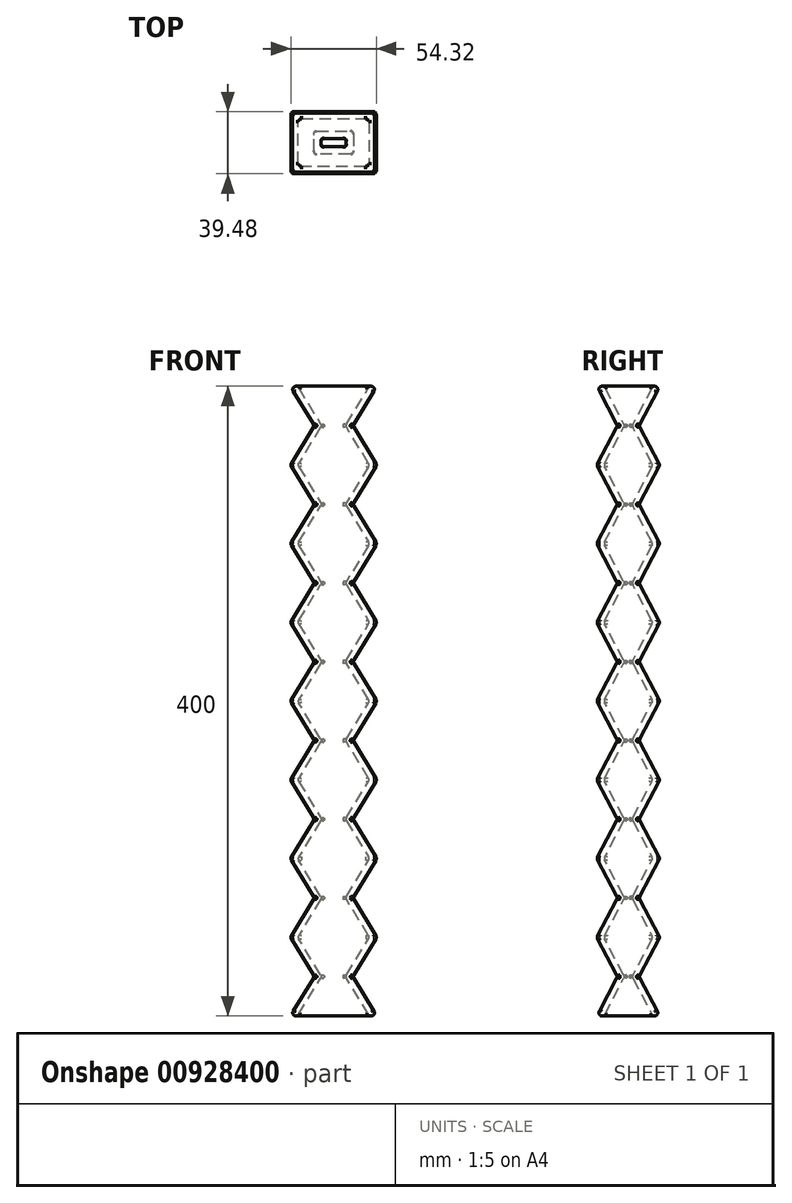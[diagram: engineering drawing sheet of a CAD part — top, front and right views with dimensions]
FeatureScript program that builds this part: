
annotation { "Feature Type Name" : "Feature", "Feature Type Description" : "" }
export const myFeature = defineFeature(function(context is Context, id is Id, definition is map)
    precondition{}
    {
        {
            var Q0;
            Q0=qCreatedBy(makeId("Top.planeOp"),FACE);
            var sketch = newSketch(context, id + "F0", { "sketchPlane" : qUnion([Q0])});
            skLineSegment(sketch, "E0.bottom", {"start": v(0, 0) * mm, "end": v(55, 0) * mm});
            skLineSegment(sketch, "E0.top", {"start": v(0, 40) * mm, "end": v(55, 40) * mm});
            skLineSegment(sketch, "E0.left", {"start": v(0, 0) * mm, "end": v(0, 40) * mm});
            skLineSegment(sketch, "E0.right", {"start": v(55, 0) * mm, "end": v(55, 40) * mm});
            skSolve(sketch);
        }
        {
            var Q0;
            Q0=qCreatedBy(makeId("Top.planeOp"),FACE);
            var sketch = newSketch(context, id + "F1", { "sketchPlane" : qUnion([Q0])});
            skSolve(sketch);
        }
        {
            var Q0;
            Q0 = qBodyType(qCreatedBy(id + "F1" ,EDGE), BodyType.WIRE);
            var Q1;
            Q1=qCreatedBy(makeId("Top.planeOp"),FACE);
            cPlane(context, id + "F2", {"entities" : qUnion([Q0, Q1]), "cplaneType" : CPlaneType.OFFSET, "offset" : 25 * mm, "width" : 150 * mm, "height" : 150 * mm});
        }
        {
            var Q0;
            Q0=qCreatedBy(id+"F2.planeOp",FACE);
            var sketch = newSketch(context, id + "F3", { "sketchPlane" : qUnion([Q0])});
            skLineSegment(sketch, "E1.bottom", {"start": v(39.73, 13.08) * mm, "end": v(15.27, 13.08) * mm});
            skLineSegment(sketch, "E1.top", {"start": v(39.73, 26.92) * mm, "end": v(15.27, 26.92) * mm});
            skLineSegment(sketch, "E1.left", {"start": v(39.73, 13.08) * mm, "end": v(39.73, 26.92) * mm});
            skLineSegment(sketch, "E1.right", {"start": v(15.27, 13.08) * mm, "end": v(15.27, 26.92) * mm});
            skLineSegment(sketch, "E2", {"start": v(27.5, 13.08) * mm, "end": v(27.5, 43.83) * mm, "construction": true});
            skPoint(sketch, "E2.endSnap0", {"position": v(27.5, 26.92) * mm});
            skLineSegment(sketch, "E3", {"start": v(27.5, 13.08) * mm, "end": v(27.5, -11.38) * mm, "construction": true});
            skLineSegment(sketch, "E4", {"start": v(39.73, 20) * mm, "end": v(-10.64, 20) * mm, "construction": true});
            skLineSegment(sketch, "E5", {"start": v(39.73, 20) * mm, "end": v(57.7, 20) * mm, "construction": true});
            skSolve(sketch);
        }
        {
            var Q0;
            Q0=makeQuery(id+"F0.imprint","IMPRINT",FACE,{"disambiguationData":[TD([[makeQuery(id+"F0.imprint","IMPRINT",EDGE,{"derivedFrom":sQuery(id+"F0.wireOp",EDGE,"E0.bottom")}),1.0]])]});
            var Q1;
            Q1=makeQuery(id+"F3.imprint","IMPRINT",FACE,{"disambiguationData":[TD([[makeQuery(id+"F3.imprint","IMPRINT",EDGE,{"derivedFrom":sQuery(id+"F3.wireOp",EDGE,"E1.bottom")}),-1.0]])]});
            loft(context, id + "F4", {"sheetProfilesArray" : [{ "sheetProfileEntities" : qUnion([Q0]) }, { "sheetProfileEntities" : qUnion([Q1]) }]});
        }
        {
            var Q0;
            Q0=makeQuery(id+"F4.opLoft","SWEPT_BODY",BODY,{"disambiguationData":[OSD([makeQuery(id+"F0.imprint","IMPRINT",FACE,{"disambiguationData":[TD([[makeQuery(id+"F0.imprint","IMPRINT",EDGE,{"derivedFrom":sQuery(id+"F0.wireOp",EDGE,"E0.bottom")}),1.0]])]}),makeQuery(id+"F3.imprint","IMPRINT",FACE,{"disambiguationData":[TD([[makeQuery(id+"F3.imprint","IMPRINT",EDGE,{"derivedFrom":sQuery(id+"F3.wireOp",EDGE,"E1.bottom")}),-1.0]])]})])]});
            var Q1;
            Q1=makeQuery(id+"F4.opLoft","CAP_FACE",FACE,{"disambiguationData":[OSD([makeQuery(id+"F3.imprint","IMPRINT",FACE,{"disambiguationData":[TD([[makeQuery(id+"F3.imprint","IMPRINT",EDGE,{"derivedFrom":sQuery(id+"F3.wireOp",EDGE,"E1.bottom")}),-1.0]])]})])],"isStart":true});
            mirror(context, id + "F5", {"operationType" : NewBodyOperationType.ADD, "entities" : qUnion([Q0]), "mirrorPlane" : qUnion([Q1])});
        }
        {
            var Q0;
            Q0=makeQuery(id+"F4.opLoft","SWEPT_BODY",BODY,{"disambiguationData":[OSD([makeQuery(id+"F0.imprint","IMPRINT",FACE,{"disambiguationData":[TD([[makeQuery(id+"F0.imprint","IMPRINT",EDGE,{"derivedFrom":sQuery(id+"F0.wireOp",EDGE,"E0.bottom")}),1.0]])]}),makeQuery(id+"F3.imprint","IMPRINT",FACE,{"disambiguationData":[TD([[makeQuery(id+"F3.imprint","IMPRINT",EDGE,{"derivedFrom":sQuery(id+"F3.wireOp",EDGE,"E1.bottom")}),-1.0]])]})])]});
            var Q1;
            Q1=makeQuery(id+"F5.opPattern","COPY",FACE,{"derivedFrom":makeQuery(id+"F4.opLoft","CAP_FACE",FACE,{"disambiguationData":[OSD([makeQuery(id+"F0.imprint","IMPRINT",FACE,{"disambiguationData":[TD([[makeQuery(id+"F0.imprint","IMPRINT",EDGE,{"derivedFrom":sQuery(id+"F0.wireOp",EDGE,"E0.bottom")}),1.0]])]})])],"isStart":true}),"instanceName":"1"});
            mirror(context, id + "F6", {"operationType" : NewBodyOperationType.ADD, "entities" : qUnion([Q0]), "mirrorPlane" : qUnion([Q1])});
        }
        {
            var Q0;
            Q0=makeQuery(id+"F4.opLoft","SWEPT_BODY",BODY,{"disambiguationData":[OSD([makeQuery(id+"F0.imprint","IMPRINT",FACE,{"disambiguationData":[TD([[makeQuery(id+"F0.imprint","IMPRINT",EDGE,{"derivedFrom":sQuery(id+"F0.wireOp",EDGE,"E0.bottom")}),1.0]])]}),makeQuery(id+"F3.imprint","IMPRINT",FACE,{"disambiguationData":[TD([[makeQuery(id+"F3.imprint","IMPRINT",EDGE,{"derivedFrom":sQuery(id+"F3.wireOp",EDGE,"E1.bottom")}),-1.0]])]})])]});
            var Q1;
            Q1=makeQuery(id+"F4.opLoft","CAP_FACE",FACE,{"disambiguationData":[OSD([makeQuery(id+"F0.imprint","IMPRINT",FACE,{"disambiguationData":[TD([[makeQuery(id+"F0.imprint","IMPRINT",EDGE,{"derivedFrom":sQuery(id+"F0.wireOp",EDGE,"E0.bottom")}),1.0]])]})])],"isStart":true});
            mirror(context, id + "F7", {"operationType" : NewBodyOperationType.ADD, "entities" : qUnion([Q0]), "mirrorPlane" : qUnion([Q1])});
        }
        {
            var Q0;
            Q0=makeQuery(id+"F4.opLoft","SWEPT_BODY",BODY,{"disambiguationData":[OSD([makeQuery(id+"F0.imprint","IMPRINT",FACE,{"disambiguationData":[TD([[makeQuery(id+"F0.imprint","IMPRINT",EDGE,{"derivedFrom":sQuery(id+"F0.wireOp",EDGE,"E0.bottom")}),1.0]])]}),makeQuery(id+"F3.imprint","IMPRINT",FACE,{"disambiguationData":[TD([[makeQuery(id+"F3.imprint","IMPRINT",EDGE,{"derivedFrom":sQuery(id+"F3.wireOp",EDGE,"E1.bottom")}),-1.0]])]})])]});
            var Q1;
            Q1=makeQuery(id+"F7.opPattern","COPY",FACE,{"derivedFrom":makeQuery(id+"F6.opPattern","COPY",FACE,{"derivedFrom":makeQuery(id+"F4.opLoft","CAP_FACE",FACE,{"disambiguationData":[OSD([makeQuery(id+"F0.imprint","IMPRINT",FACE,{"disambiguationData":[TD([[makeQuery(id+"F0.imprint","IMPRINT",EDGE,{"derivedFrom":sQuery(id+"F0.wireOp",EDGE,"E0.bottom")}),1.0]])]})])],"isStart":true}),"instanceName":"1"}),"instanceName":"1"});
            mirror(context, id + "F8", {"operationType" : NewBodyOperationType.ADD, "entities" : qUnion([Q0]), "mirrorPlane" : qUnion([Q1])});
        }
        {
            var Q0;
            Q0=makeQuery(id+"F6.opPattern","COPY",FACE,{"derivedFrom":makeQuery(id+"F4.opLoft","CAP_FACE",FACE,{"disambiguationData":[OSD([makeQuery(id+"F0.imprint","IMPRINT",FACE,{"disambiguationData":[TD([[makeQuery(id+"F0.imprint","IMPRINT",EDGE,{"derivedFrom":sQuery(id+"F0.wireOp",EDGE,"E0.bottom")}),1.0]])]})])],"isStart":true}),"instanceName":"1"});
            var Q1;
            Q1=makeQuery(id+"F8.opPattern","COPY",FACE,{"derivedFrom":makeQuery(id+"F6.opPattern","COPY",FACE,{"derivedFrom":makeQuery(id+"F4.opLoft","CAP_FACE",FACE,{"disambiguationData":[OSD([makeQuery(id+"F0.imprint","IMPRINT",FACE,{"disambiguationData":[TD([[makeQuery(id+"F0.imprint","IMPRINT",EDGE,{"derivedFrom":sQuery(id+"F0.wireOp",EDGE,"E0.bottom")}),1.0]])]})])],"isStart":true}),"instanceName":"1"}),"instanceName":"1"});
            shell(context, id + "F9", {"entities" : qUnion([Q0, Q1]), "thickness" : 4 * mm});
        }
        {
            var Q0;
            Q0=makeQuery(id+"F4.opLoft","SWEPT_BODY",BODY,{"disambiguationData":[OSD([makeQuery(id+"F0.imprint","IMPRINT",FACE,{"disambiguationData":[TD([[makeQuery(id+"F0.imprint","IMPRINT",EDGE,{"derivedFrom":sQuery(id+"F0.wireOp",EDGE,"E0.bottom")}),1.0]])]}),makeQuery(id+"F3.imprint","IMPRINT",FACE,{"disambiguationData":[TD([[makeQuery(id+"F3.imprint","IMPRINT",EDGE,{"derivedFrom":sQuery(id+"F3.wireOp",EDGE,"E1.bottom")}),-1.0]])]})])]});
            var Q1;
            {var subQ0=makeQuery(id+"F5.opPattern","COPY",EDGE,{"derivedFrom":makeQuery(id+"F4.opLoft","MID_CAP_EDGE",EDGE,{"disambiguationData":[OSD([sQuery(id+"F0.wireOp",EDGE,"E0.bottom"),sQuery(id+"F0.wireOp",EDGE,"E0.top"),sQuery(id+"F0.wireOp",EDGE,"E0.left")])],"capPos":0.0}),"instanceName":"1"});Q1=makeQuery(id+"F8.opPattern","COPY",EDGE,{"derivedFrom":makeQuery(id+"F6.boolean.opBoolean","MERGE",EDGE,{"derivedFrom":[subQ0,makeQuery(id+"F6.opPattern","COPY",EDGE,{"derivedFrom":subQ0,"instanceName":"1"})]}),"instanceName":"1"});}
            transform(context, id + "F10", {"entities" : qUnion([Q0]), "transformType" : TransformType.TRANSLATION_ENTITY, "oppositeDirectionEntity" : false, "transformLine" : qUnion([Q1]), "makeCopy" : false});
        }
        {
            var Q0;
            Q0=makeQuery(id+"F5.opPattern","COPY",EDGE,{"derivedFrom":makeQuery(id+"F4.opLoft","SWEPT_EDGE",EDGE,{"disambiguationData":[OSD([sQuery(id+"F0.wireOp",EDGE,"E0.bottom"),sQuery(id+"F0.wireOp",EDGE,"E0.left"),sQuery(id+"F3.wireOp",EDGE,"E1.bottom"),sQuery(id+"F3.wireOp",EDGE,"E1.right")])]}),"instanceName":"1"});
            var Q1;
            {var subQ0=makeQuery(id+"F4.opLoft","MID_CAP_EDGE",EDGE,{"disambiguationData":[OSD([sQuery(id+"F3.wireOp",EDGE,"E1.bottom"),sQuery(id+"F3.wireOp",EDGE,"E1.left"),sQuery(id+"F3.wireOp",EDGE,"E1.right")])],"capPos":1.0});Q1=makeQuery(id+"F5.boolean.opBoolean","MERGE",EDGE,{"derivedFrom":[subQ0,makeQuery(id+"F5.opPattern","COPY",EDGE,{"derivedFrom":subQ0,"instanceName":"1"})]});}
            var Q2;
            Q2=makeQuery(id+"F6.opPattern","COPY",EDGE,{"derivedFrom":makeQuery(id+"F4.opLoft","SWEPT_EDGE",EDGE,{"disambiguationData":[OSD([sQuery(id+"F0.wireOp",EDGE,"E0.bottom"),sQuery(id+"F0.wireOp",EDGE,"E0.left"),sQuery(id+"F3.wireOp",EDGE,"E1.bottom"),sQuery(id+"F3.wireOp",EDGE,"E1.right")])]}),"instanceName":"1"});
            var Q3;
            Q3=makeQuery(id+"F6.opPattern","COPY",EDGE,{"derivedFrom":makeQuery(id+"F5.opPattern","COPY",EDGE,{"derivedFrom":makeQuery(id+"F4.opLoft","SWEPT_EDGE",EDGE,{"disambiguationData":[OSD([sQuery(id+"F0.wireOp",EDGE,"E0.bottom"),sQuery(id+"F0.wireOp",EDGE,"E0.left"),sQuery(id+"F3.wireOp",EDGE,"E1.bottom"),sQuery(id+"F3.wireOp",EDGE,"E1.right")])]}),"instanceName":"1"}),"instanceName":"1"});
            var Q4;
            Q4=makeQuery(id+"F8.opPattern","COPY",EDGE,{"derivedFrom":makeQuery(id+"F6.opPattern","COPY",EDGE,{"derivedFrom":makeQuery(id+"F4.opLoft","MID_CAP_EDGE",EDGE,{"disambiguationData":[OSD([sQuery(id+"F0.wireOp",EDGE,"E0.bottom"),sQuery(id+"F0.wireOp",EDGE,"E0.top"),sQuery(id+"F0.wireOp",EDGE,"E0.right")])],"capPos":0.0}),"instanceName":"1"}),"instanceName":"1"});
            var Q5;
            {var subQ0=sQuery(id+"F3.wireOp",EDGE,"E1.right");var subQ1=sQuery(id+"F3.wireOp",EDGE,"E1.left");var subQ2=sQuery(id+"F3.wireOp",EDGE,"E1.bottom");var subQ3=makeQuery(id+"F4.opLoft","MID_CAP_EDGE",EDGE,{"disambiguationData":[OSD([subQ2,subQ1,subQ0])],"capPos":1.0});Q5=makeQuery(id+"F9.opShell","OFFSET_EDGE",EDGE,{"disambiguationData":[OSD([subQ2,subQ1,subQ0]),TDD([makeQuery(id+"F8.opPattern","COPY",EDGE,{"derivedFrom":makeQuery(id+"F7.opPattern","COPY",EDGE,{"derivedFrom":makeQuery(id+"F6.opPattern","COPY",EDGE,{"derivedFrom":makeQuery(id+"F5.boolean.opBoolean","MERGE",EDGE,{"derivedFrom":[subQ3,makeQuery(id+"F5.opPattern","COPY",EDGE,{"derivedFrom":subQ3,"instanceName":"1"})]}),"instanceName":"1"}),"instanceName":"1"}),"instanceName":"1"})])]});}
            var Q6;
            {var subQ0=sQuery(id+"F0.wireOp",EDGE,"E0.right");var subQ1=sQuery(id+"F0.wireOp",EDGE,"E0.top");var subQ2=sQuery(id+"F0.wireOp",EDGE,"E0.bottom");Q6=makeQuery(id+"F9.opShell","OFFSET_EDGE",EDGE,{"disambiguationData":[OSD([subQ2,subQ1,subQ0]),TDD([makeQuery(id+"F8.opPattern","COPY",EDGE,{"derivedFrom":makeQuery(id+"F6.opPattern","COPY",EDGE,{"derivedFrom":makeQuery(id+"F4.opLoft","MID_CAP_EDGE",EDGE,{"disambiguationData":[OSD([subQ2,subQ1,subQ0])],"capPos":0.0}),"instanceName":"1"}),"instanceName":"1"})])]});}
            var Q7;
            {var subQ0=sQuery(id+"F3.wireOp",EDGE,"E1.left");var subQ1=sQuery(id+"F3.wireOp",EDGE,"E1.top");var subQ2=sQuery(id+"F0.wireOp",EDGE,"E0.right");var subQ3=sQuery(id+"F0.wireOp",EDGE,"E0.top");Q7=makeQuery(id+"F9.opShell","OFFSET_EDGE",EDGE,{"disambiguationData":[OSD([subQ3,subQ2,subQ1,subQ0]),TDD([makeQuery(id+"F8.opPattern","COPY",EDGE,{"derivedFrom":makeQuery(id+"F6.opPattern","COPY",EDGE,{"derivedFrom":makeQuery(id+"F4.opLoft","SWEPT_EDGE",EDGE,{"disambiguationData":[OSD([subQ3,subQ2,subQ1,subQ0])]}),"instanceName":"1"}),"instanceName":"1"})])]});}
            var Q8;
            {var subQ0=sQuery(id+"F0.wireOp",EDGE,"E0.right");var subQ1=sQuery(id+"F0.wireOp",EDGE,"E0.top");var subQ2=sQuery(id+"F0.wireOp",EDGE,"E0.bottom");var subQ3=makeQuery(id+"F7.opPattern","COPY",EDGE,{"derivedFrom":makeQuery(id+"F6.opPattern","COPY",EDGE,{"derivedFrom":makeQuery(id+"F4.opLoft","MID_CAP_EDGE",EDGE,{"disambiguationData":[OSD([subQ2,subQ1,subQ0])],"capPos":0.0}),"instanceName":"1"}),"instanceName":"1"});Q8=makeQuery(id+"F9.opShell","OFFSET_EDGE",EDGE,{"disambiguationData":[OSD([subQ2,subQ1,subQ0]),TDD([makeQuery(id+"F8.boolean.opBoolean","MERGE",EDGE,{"derivedFrom":[subQ3,makeQuery(id+"F8.opPattern","COPY",EDGE,{"derivedFrom":subQ3,"instanceName":"1"})]})])]});}
            var Q9;
            {var subQ0=makeQuery(id+"F5.opPattern","COPY",EDGE,{"derivedFrom":makeQuery(id+"F4.opLoft","MID_CAP_EDGE",EDGE,{"disambiguationData":[OSD([sQuery(id+"F0.wireOp",EDGE,"E0.bottom"),sQuery(id+"F0.wireOp",EDGE,"E0.top"),sQuery(id+"F0.wireOp",EDGE,"E0.right")])],"capPos":0.0}),"instanceName":"1"});Q9=makeQuery(id+"F8.opPattern","COPY",EDGE,{"derivedFrom":makeQuery(id+"F6.boolean.opBoolean","MERGE",EDGE,{"derivedFrom":[subQ0,makeQuery(id+"F6.opPattern","COPY",EDGE,{"derivedFrom":subQ0,"instanceName":"1"})]}),"instanceName":"1"});}
            var Q10;
            {var subQ0=makeQuery(id+"F4.opLoft","MID_CAP_EDGE",EDGE,{"disambiguationData":[OSD([sQuery(id+"F3.wireOp",EDGE,"E1.bottom"),sQuery(id+"F3.wireOp",EDGE,"E1.left"),sQuery(id+"F3.wireOp",EDGE,"E1.right")])],"capPos":1.0});Q10=makeQuery(id+"F7.opPattern","COPY",EDGE,{"derivedFrom":makeQuery(id+"F5.boolean.opBoolean","MERGE",EDGE,{"derivedFrom":[subQ0,makeQuery(id+"F5.opPattern","COPY",EDGE,{"derivedFrom":subQ0,"instanceName":"1"})]}),"instanceName":"1"});}
            var Q11;
            {var subQ0=makeQuery(id+"F4.opLoft","MID_CAP_EDGE",EDGE,{"disambiguationData":[OSD([sQuery(id+"F3.wireOp",EDGE,"E1.bottom"),sQuery(id+"F3.wireOp",EDGE,"E1.top"),sQuery(id+"F3.wireOp",EDGE,"E1.left")])],"capPos":1.0});Q11=makeQuery(id+"F7.opPattern","COPY",EDGE,{"derivedFrom":makeQuery(id+"F6.opPattern","COPY",EDGE,{"derivedFrom":makeQuery(id+"F5.boolean.opBoolean","MERGE",EDGE,{"derivedFrom":[subQ0,makeQuery(id+"F5.opPattern","COPY",EDGE,{"derivedFrom":subQ0,"instanceName":"1"})]}),"instanceName":"1"}),"instanceName":"1"});}
            var Q12;
            {var subQ0=makeQuery(id+"F4.opLoft","MID_CAP_EDGE",EDGE,{"disambiguationData":[OSD([sQuery(id+"F3.wireOp",EDGE,"E1.top"),sQuery(id+"F3.wireOp",EDGE,"E1.left"),sQuery(id+"F3.wireOp",EDGE,"E1.right")])],"capPos":1.0});Q12=makeQuery(id+"F7.opPattern","COPY",EDGE,{"derivedFrom":makeQuery(id+"F6.opPattern","COPY",EDGE,{"derivedFrom":makeQuery(id+"F5.boolean.opBoolean","MERGE",EDGE,{"derivedFrom":[subQ0,makeQuery(id+"F5.opPattern","COPY",EDGE,{"derivedFrom":subQ0,"instanceName":"1"})]}),"instanceName":"1"}),"instanceName":"1"});}
            var Q13;
            {var subQ0=sQuery(id+"F0.wireOp",EDGE,"E0.left");var subQ1=sQuery(id+"F0.wireOp",EDGE,"E0.top");var subQ2=sQuery(id+"F0.wireOp",EDGE,"E0.bottom");var subQ3=makeQuery(id+"F5.opPattern","COPY",EDGE,{"derivedFrom":makeQuery(id+"F4.opLoft","MID_CAP_EDGE",EDGE,{"disambiguationData":[OSD([subQ2,subQ1,subQ0])],"capPos":0.0}),"instanceName":"1"});Q13=makeQuery(id+"F9.opShell","OFFSET_EDGE",EDGE,{"disambiguationData":[OSD([subQ2,subQ1,subQ0]),TDD([makeQuery(id+"F6.boolean.opBoolean","MERGE",EDGE,{"derivedFrom":[subQ3,makeQuery(id+"F6.opPattern","COPY",EDGE,{"derivedFrom":subQ3,"instanceName":"1"})]})])]});}
            var Q14;
            Q14=makeQuery(id+"F8.opPattern","COPY",EDGE,{"derivedFrom":makeQuery(id+"F7.opPattern","COPY",EDGE,{"derivedFrom":makeQuery(id+"F5.opPattern","COPY",EDGE,{"derivedFrom":makeQuery(id+"F4.opLoft","SWEPT_EDGE",EDGE,{"disambiguationData":[OSD([sQuery(id+"F0.wireOp",EDGE,"E0.bottom"),sQuery(id+"F0.wireOp",EDGE,"E0.right"),sQuery(id+"F3.wireOp",EDGE,"E1.bottom"),sQuery(id+"F3.wireOp",EDGE,"E1.left")])]}),"instanceName":"1"}),"instanceName":"1"}),"instanceName":"1"});
            var Q15;
            {var subQ0=sQuery(id+"F3.wireOp",EDGE,"E1.right");var subQ1=sQuery(id+"F3.wireOp",EDGE,"E1.top");var subQ2=sQuery(id+"F0.wireOp",EDGE,"E0.left");var subQ3=sQuery(id+"F0.wireOp",EDGE,"E0.top");Q15=makeQuery(id+"F9.opShell","OFFSET_EDGE",EDGE,{"disambiguationData":[OSD([subQ3,subQ2,subQ1,subQ0]),TDD([makeQuery(id+"F4.opLoft","SWEPT_EDGE",EDGE,{"disambiguationData":[OSD([subQ3,subQ2,subQ1,subQ0])]})])]});}
            var Q16;
            {var subQ0=makeQuery(id+"F4.opLoft","MID_CAP_EDGE",EDGE,{"disambiguationData":[OSD([sQuery(id+"F0.wireOp",EDGE,"E0.bottom"),sQuery(id+"F0.wireOp",EDGE,"E0.top"),sQuery(id+"F0.wireOp",EDGE,"E0.right")])],"capPos":0.0});Q16=makeQuery(id+"F8.opPattern","COPY",EDGE,{"derivedFrom":makeQuery(id+"F7.boolean.opBoolean","MERGE",EDGE,{"derivedFrom":[subQ0,makeQuery(id+"F7.opPattern","COPY",EDGE,{"derivedFrom":subQ0,"instanceName":"1"})]}),"instanceName":"1"});}
            var Q17;
            {var subQ0=makeQuery(id+"F4.opLoft","MID_CAP_EDGE",EDGE,{"disambiguationData":[OSD([sQuery(id+"F3.wireOp",EDGE,"E1.bottom"),sQuery(id+"F3.wireOp",EDGE,"E1.top"),sQuery(id+"F3.wireOp",EDGE,"E1.left")])],"capPos":1.0});Q17=makeQuery(id+"F7.opPattern","COPY",EDGE,{"derivedFrom":makeQuery(id+"F5.boolean.opBoolean","MERGE",EDGE,{"derivedFrom":[subQ0,makeQuery(id+"F5.opPattern","COPY",EDGE,{"derivedFrom":subQ0,"instanceName":"1"})]}),"instanceName":"1"});}
            var Q18;
            {var subQ0=sQuery(id+"F3.wireOp",EDGE,"E1.left");var subQ1=sQuery(id+"F3.wireOp",EDGE,"E1.bottom");var subQ2=sQuery(id+"F0.wireOp",EDGE,"E0.right");var subQ3=sQuery(id+"F0.wireOp",EDGE,"E0.bottom");Q18=makeQuery(id+"F9.opShell","OFFSET_EDGE",EDGE,{"disambiguationData":[OSD([subQ3,subQ2,subQ1,subQ0]),TDD([makeQuery(id+"F8.opPattern","COPY",EDGE,{"derivedFrom":makeQuery(id+"F7.opPattern","COPY",EDGE,{"derivedFrom":makeQuery(id+"F4.opLoft","SWEPT_EDGE",EDGE,{"disambiguationData":[OSD([subQ3,subQ2,subQ1,subQ0])]}),"instanceName":"1"}),"instanceName":"1"})])]});}
            var Q19;
            {var subQ0=sQuery(id+"F3.wireOp",EDGE,"E1.right");var subQ1=sQuery(id+"F3.wireOp",EDGE,"E1.top");var subQ2=sQuery(id+"F0.wireOp",EDGE,"E0.left");var subQ3=sQuery(id+"F0.wireOp",EDGE,"E0.top");Q19=makeQuery(id+"F9.opShell","OFFSET_EDGE",EDGE,{"disambiguationData":[OSD([subQ3,subQ2,subQ1,subQ0]),TDD([makeQuery(id+"F6.opPattern","COPY",EDGE,{"derivedFrom":makeQuery(id+"F4.opLoft","SWEPT_EDGE",EDGE,{"disambiguationData":[OSD([subQ3,subQ2,subQ1,subQ0])]}),"instanceName":"1"})])]});}
            var Q20;
            {var subQ0=sQuery(id+"F3.wireOp",EDGE,"E1.left");var subQ1=sQuery(id+"F3.wireOp",EDGE,"E1.bottom");var subQ2=sQuery(id+"F0.wireOp",EDGE,"E0.right");var subQ3=sQuery(id+"F0.wireOp",EDGE,"E0.bottom");Q20=makeQuery(id+"F9.opShell","OFFSET_EDGE",EDGE,{"disambiguationData":[OSD([subQ3,subQ2,subQ1,subQ0]),TDD([makeQuery(id+"F7.opPattern","COPY",EDGE,{"derivedFrom":makeQuery(id+"F6.opPattern","COPY",EDGE,{"derivedFrom":makeQuery(id+"F5.opPattern","COPY",EDGE,{"derivedFrom":makeQuery(id+"F4.opLoft","SWEPT_EDGE",EDGE,{"disambiguationData":[OSD([subQ3,subQ2,subQ1,subQ0])]}),"instanceName":"1"}),"instanceName":"1"}),"instanceName":"1"})])]});}
            var Q21;
            {var subQ0=sQuery(id+"F3.wireOp",EDGE,"E1.left");var subQ1=sQuery(id+"F3.wireOp",EDGE,"E1.top");var subQ2=sQuery(id+"F0.wireOp",EDGE,"E0.right");var subQ3=sQuery(id+"F0.wireOp",EDGE,"E0.top");Q21=makeQuery(id+"F9.opShell","OFFSET_EDGE",EDGE,{"disambiguationData":[OSD([subQ3,subQ2,subQ1,subQ0]),TDD([makeQuery(id+"F8.opPattern","COPY",EDGE,{"derivedFrom":makeQuery(id+"F7.opPattern","COPY",EDGE,{"derivedFrom":makeQuery(id+"F6.opPattern","COPY",EDGE,{"derivedFrom":makeQuery(id+"F4.opLoft","SWEPT_EDGE",EDGE,{"disambiguationData":[OSD([subQ3,subQ2,subQ1,subQ0])]}),"instanceName":"1"}),"instanceName":"1"}),"instanceName":"1"})])]});}
            var Q22;
            Q22=makeQuery(id+"F8.opPattern","COPY",EDGE,{"derivedFrom":makeQuery(id+"F6.opPattern","COPY",EDGE,{"derivedFrom":makeQuery(id+"F5.opPattern","COPY",EDGE,{"derivedFrom":makeQuery(id+"F4.opLoft","SWEPT_EDGE",EDGE,{"disambiguationData":[OSD([sQuery(id+"F0.wireOp",EDGE,"E0.top"),sQuery(id+"F0.wireOp",EDGE,"E0.right"),sQuery(id+"F3.wireOp",EDGE,"E1.top"),sQuery(id+"F3.wireOp",EDGE,"E1.left")])]}),"instanceName":"1"}),"instanceName":"1"}),"instanceName":"1"});
            var Q23;
            Q23=makeQuery(id+"F8.opPattern","COPY",EDGE,{"derivedFrom":makeQuery(id+"F7.opPattern","COPY",EDGE,{"derivedFrom":makeQuery(id+"F5.opPattern","COPY",EDGE,{"derivedFrom":makeQuery(id+"F4.opLoft","SWEPT_EDGE",EDGE,{"disambiguationData":[OSD([sQuery(id+"F0.wireOp",EDGE,"E0.top"),sQuery(id+"F0.wireOp",EDGE,"E0.right"),sQuery(id+"F3.wireOp",EDGE,"E1.top"),sQuery(id+"F3.wireOp",EDGE,"E1.left")])]}),"instanceName":"1"}),"instanceName":"1"}),"instanceName":"1"});
            var Q24;
            {var subQ0=sQuery(id+"F3.wireOp",EDGE,"E1.right");var subQ1=sQuery(id+"F3.wireOp",EDGE,"E1.top");var subQ2=sQuery(id+"F0.wireOp",EDGE,"E0.left");var subQ3=sQuery(id+"F0.wireOp",EDGE,"E0.top");Q24=makeQuery(id+"F9.opShell","OFFSET_EDGE",EDGE,{"disambiguationData":[OSD([subQ3,subQ2,subQ1,subQ0]),TDD([makeQuery(id+"F6.opPattern","COPY",EDGE,{"derivedFrom":makeQuery(id+"F5.opPattern","COPY",EDGE,{"derivedFrom":makeQuery(id+"F4.opLoft","SWEPT_EDGE",EDGE,{"disambiguationData":[OSD([subQ3,subQ2,subQ1,subQ0])]}),"instanceName":"1"}),"instanceName":"1"})])]});}
            var Q25;
            {var subQ0=sQuery(id+"F3.wireOp",EDGE,"E1.right");var subQ1=sQuery(id+"F3.wireOp",EDGE,"E1.bottom");var subQ2=sQuery(id+"F0.wireOp",EDGE,"E0.left");var subQ3=sQuery(id+"F0.wireOp",EDGE,"E0.bottom");Q25=makeQuery(id+"F9.opShell","OFFSET_EDGE",EDGE,{"disambiguationData":[OSD([subQ3,subQ2,subQ1,subQ0]),TDD([makeQuery(id+"F6.opPattern","COPY",EDGE,{"derivedFrom":makeQuery(id+"F5.opPattern","COPY",EDGE,{"derivedFrom":makeQuery(id+"F4.opLoft","SWEPT_EDGE",EDGE,{"disambiguationData":[OSD([subQ3,subQ2,subQ1,subQ0])]}),"instanceName":"1"}),"instanceName":"1"})])]});}
            var Q26;
            {var subQ0=sQuery(id+"F3.wireOp",EDGE,"E1.right");var subQ1=sQuery(id+"F3.wireOp",EDGE,"E1.left");var subQ2=sQuery(id+"F3.wireOp",EDGE,"E1.bottom");var subQ3=makeQuery(id+"F4.opLoft","MID_CAP_EDGE",EDGE,{"disambiguationData":[OSD([subQ2,subQ1,subQ0])],"capPos":1.0});Q26=makeQuery(id+"F9.opShell","OFFSET_EDGE",EDGE,{"disambiguationData":[OSD([subQ2,subQ1,subQ0]),TDD([makeQuery(id+"F5.boolean.opBoolean","MERGE",EDGE,{"derivedFrom":[subQ3,makeQuery(id+"F5.opPattern","COPY",EDGE,{"derivedFrom":subQ3,"instanceName":"1"})]})])]});}
            var Q27;
            {var subQ0=sQuery(id+"F3.wireOp",EDGE,"E1.right");var subQ1=sQuery(id+"F3.wireOp",EDGE,"E1.top");var subQ2=sQuery(id+"F0.wireOp",EDGE,"E0.left");var subQ3=sQuery(id+"F0.wireOp",EDGE,"E0.top");Q27=makeQuery(id+"F9.opShell","OFFSET_EDGE",EDGE,{"disambiguationData":[OSD([subQ3,subQ2,subQ1,subQ0]),TDD([makeQuery(id+"F7.opPattern","COPY",EDGE,{"derivedFrom":makeQuery(id+"F5.opPattern","COPY",EDGE,{"derivedFrom":makeQuery(id+"F4.opLoft","SWEPT_EDGE",EDGE,{"disambiguationData":[OSD([subQ3,subQ2,subQ1,subQ0])]}),"instanceName":"1"}),"instanceName":"1"})])]});}
            var Q28;
            {var subQ0=sQuery(id+"F3.wireOp",EDGE,"E1.right");var subQ1=sQuery(id+"F3.wireOp",EDGE,"E1.left");var subQ2=sQuery(id+"F3.wireOp",EDGE,"E1.bottom");var subQ3=makeQuery(id+"F4.opLoft","MID_CAP_EDGE",EDGE,{"disambiguationData":[OSD([subQ2,subQ1,subQ0])],"capPos":1.0});Q28=makeQuery(id+"F9.opShell","OFFSET_EDGE",EDGE,{"disambiguationData":[OSD([subQ2,subQ1,subQ0]),TDD([makeQuery(id+"F7.opPattern","COPY",EDGE,{"derivedFrom":makeQuery(id+"F6.opPattern","COPY",EDGE,{"derivedFrom":makeQuery(id+"F5.boolean.opBoolean","MERGE",EDGE,{"derivedFrom":[subQ3,makeQuery(id+"F5.opPattern","COPY",EDGE,{"derivedFrom":subQ3,"instanceName":"1"})]}),"instanceName":"1"}),"instanceName":"1"})])]});}
            var Q29;
            Q29=makeQuery(id+"F8.opPattern","COPY",EDGE,{"derivedFrom":makeQuery(id+"F7.opPattern","COPY",EDGE,{"derivedFrom":makeQuery(id+"F6.opPattern","COPY",EDGE,{"derivedFrom":makeQuery(id+"F4.opLoft","SWEPT_EDGE",EDGE,{"disambiguationData":[OSD([sQuery(id+"F0.wireOp",EDGE,"E0.bottom"),sQuery(id+"F0.wireOp",EDGE,"E0.right"),sQuery(id+"F3.wireOp",EDGE,"E1.bottom"),sQuery(id+"F3.wireOp",EDGE,"E1.left")])]}),"instanceName":"1"}),"instanceName":"1"}),"instanceName":"1"});
            var Q30;
            {var subQ0=makeQuery(id+"F4.opLoft","MID_CAP_EDGE",EDGE,{"disambiguationData":[OSD([sQuery(id+"F3.wireOp",EDGE,"E1.bottom"),sQuery(id+"F3.wireOp",EDGE,"E1.left"),sQuery(id+"F3.wireOp",EDGE,"E1.right")])],"capPos":1.0});Q30=makeQuery(id+"F7.opPattern","COPY",EDGE,{"derivedFrom":makeQuery(id+"F6.opPattern","COPY",EDGE,{"derivedFrom":makeQuery(id+"F5.boolean.opBoolean","MERGE",EDGE,{"derivedFrom":[subQ0,makeQuery(id+"F5.opPattern","COPY",EDGE,{"derivedFrom":subQ0,"instanceName":"1"})]}),"instanceName":"1"}),"instanceName":"1"});}
            var Q31;
            Q31=makeQuery(id+"F7.opPattern","COPY",EDGE,{"derivedFrom":makeQuery(id+"F5.opPattern","COPY",EDGE,{"derivedFrom":makeQuery(id+"F4.opLoft","SWEPT_EDGE",EDGE,{"disambiguationData":[OSD([sQuery(id+"F0.wireOp",EDGE,"E0.top"),sQuery(id+"F0.wireOp",EDGE,"E0.left"),sQuery(id+"F3.wireOp",EDGE,"E1.top"),sQuery(id+"F3.wireOp",EDGE,"E1.right")])]}),"instanceName":"1"}),"instanceName":"1"});
            var Q32;
            {var subQ0=makeQuery(id+"F4.opLoft","MID_CAP_EDGE",EDGE,{"disambiguationData":[OSD([sQuery(id+"F3.wireOp",EDGE,"E1.bottom"),sQuery(id+"F3.wireOp",EDGE,"E1.top"),sQuery(id+"F3.wireOp",EDGE,"E1.right")])],"capPos":1.0});Q32=makeQuery(id+"F7.opPattern","COPY",EDGE,{"derivedFrom":makeQuery(id+"F6.opPattern","COPY",EDGE,{"derivedFrom":makeQuery(id+"F5.boolean.opBoolean","MERGE",EDGE,{"derivedFrom":[subQ0,makeQuery(id+"F5.opPattern","COPY",EDGE,{"derivedFrom":subQ0,"instanceName":"1"})]}),"instanceName":"1"}),"instanceName":"1"});}
            var Q33;
            {var subQ0=makeQuery(id+"F4.opLoft","MID_CAP_EDGE",EDGE,{"disambiguationData":[OSD([sQuery(id+"F3.wireOp",EDGE,"E1.bottom"),sQuery(id+"F3.wireOp",EDGE,"E1.top"),sQuery(id+"F3.wireOp",EDGE,"E1.right")])],"capPos":1.0});Q33=makeQuery(id+"F7.opPattern","COPY",EDGE,{"derivedFrom":makeQuery(id+"F5.boolean.opBoolean","MERGE",EDGE,{"derivedFrom":[subQ0,makeQuery(id+"F5.opPattern","COPY",EDGE,{"derivedFrom":subQ0,"instanceName":"1"})]}),"instanceName":"1"});}
            var Q34;
            {var subQ0=sQuery(id+"F3.wireOp",EDGE,"E1.left");var subQ1=sQuery(id+"F3.wireOp",EDGE,"E1.bottom");var subQ2=sQuery(id+"F0.wireOp",EDGE,"E0.right");var subQ3=sQuery(id+"F0.wireOp",EDGE,"E0.bottom");Q34=makeQuery(id+"F9.opShell","OFFSET_EDGE",EDGE,{"disambiguationData":[OSD([subQ3,subQ2,subQ1,subQ0]),TDD([makeQuery(id+"F8.opPattern","COPY",EDGE,{"derivedFrom":makeQuery(id+"F7.opPattern","COPY",EDGE,{"derivedFrom":makeQuery(id+"F5.opPattern","COPY",EDGE,{"derivedFrom":makeQuery(id+"F4.opLoft","SWEPT_EDGE",EDGE,{"disambiguationData":[OSD([subQ3,subQ2,subQ1,subQ0])]}),"instanceName":"1"}),"instanceName":"1"}),"instanceName":"1"})])]});}
            var Q35;
            Q35=makeQuery(id+"F8.opPattern","COPY",EDGE,{"derivedFrom":makeQuery(id+"F7.opPattern","COPY",EDGE,{"derivedFrom":makeQuery(id+"F4.opLoft","SWEPT_EDGE",EDGE,{"disambiguationData":[OSD([sQuery(id+"F0.wireOp",EDGE,"E0.top"),sQuery(id+"F0.wireOp",EDGE,"E0.right"),sQuery(id+"F3.wireOp",EDGE,"E1.top"),sQuery(id+"F3.wireOp",EDGE,"E1.left")])]}),"instanceName":"1"}),"instanceName":"1"});
            var Q36;
            Q36=makeQuery(id+"F8.opPattern","COPY",EDGE,{"derivedFrom":makeQuery(id+"F6.opPattern","COPY",EDGE,{"derivedFrom":makeQuery(id+"F5.opPattern","COPY",EDGE,{"derivedFrom":makeQuery(id+"F4.opLoft","SWEPT_EDGE",EDGE,{"disambiguationData":[OSD([sQuery(id+"F0.wireOp",EDGE,"E0.bottom"),sQuery(id+"F0.wireOp",EDGE,"E0.right"),sQuery(id+"F3.wireOp",EDGE,"E1.bottom"),sQuery(id+"F3.wireOp",EDGE,"E1.left")])]}),"instanceName":"1"}),"instanceName":"1"}),"instanceName":"1"});
            var Q37;
            {var subQ0=sQuery(id+"F3.wireOp",EDGE,"E1.right");var subQ1=sQuery(id+"F3.wireOp",EDGE,"E1.left");var subQ2=sQuery(id+"F3.wireOp",EDGE,"E1.bottom");var subQ3=makeQuery(id+"F4.opLoft","MID_CAP_EDGE",EDGE,{"disambiguationData":[OSD([subQ2,subQ1,subQ0])],"capPos":1.0});Q37=makeQuery(id+"F9.opShell","OFFSET_EDGE",EDGE,{"disambiguationData":[OSD([subQ2,subQ1,subQ0]),TDD([makeQuery(id+"F7.opPattern","COPY",EDGE,{"derivedFrom":makeQuery(id+"F5.boolean.opBoolean","MERGE",EDGE,{"derivedFrom":[subQ3,makeQuery(id+"F5.opPattern","COPY",EDGE,{"derivedFrom":subQ3,"instanceName":"1"})]}),"instanceName":"1"})])]});}
            var Q38;
            {var subQ0=makeQuery(id+"F5.opPattern","COPY",EDGE,{"derivedFrom":makeQuery(id+"F4.opLoft","MID_CAP_EDGE",EDGE,{"disambiguationData":[OSD([sQuery(id+"F0.wireOp",EDGE,"E0.bottom"),sQuery(id+"F0.wireOp",EDGE,"E0.top"),sQuery(id+"F0.wireOp",EDGE,"E0.right")])],"capPos":0.0}),"instanceName":"1"});Q38=makeQuery(id+"F8.opPattern","COPY",EDGE,{"derivedFrom":makeQuery(id+"F7.opPattern","COPY",EDGE,{"derivedFrom":makeQuery(id+"F6.boolean.opBoolean","MERGE",EDGE,{"derivedFrom":[subQ0,makeQuery(id+"F6.opPattern","COPY",EDGE,{"derivedFrom":subQ0,"instanceName":"1"})]}),"instanceName":"1"}),"instanceName":"1"});}
            var Q39;
            Q39=makeQuery(id+"F7.opPattern","COPY",EDGE,{"derivedFrom":makeQuery(id+"F6.opPattern","COPY",EDGE,{"derivedFrom":makeQuery(id+"F4.opLoft","SWEPT_EDGE",EDGE,{"disambiguationData":[OSD([sQuery(id+"F0.wireOp",EDGE,"E0.bottom"),sQuery(id+"F0.wireOp",EDGE,"E0.right"),sQuery(id+"F3.wireOp",EDGE,"E1.bottom"),sQuery(id+"F3.wireOp",EDGE,"E1.left")])]}),"instanceName":"1"}),"instanceName":"1"});
            var Q40;
            Q40=makeQuery(id+"F7.opPattern","COPY",EDGE,{"derivedFrom":makeQuery(id+"F6.opPattern","COPY",EDGE,{"derivedFrom":makeQuery(id+"F5.opPattern","COPY",EDGE,{"derivedFrom":makeQuery(id+"F4.opLoft","SWEPT_EDGE",EDGE,{"disambiguationData":[OSD([sQuery(id+"F0.wireOp",EDGE,"E0.top"),sQuery(id+"F0.wireOp",EDGE,"E0.left"),sQuery(id+"F3.wireOp",EDGE,"E1.top"),sQuery(id+"F3.wireOp",EDGE,"E1.right")])]}),"instanceName":"1"}),"instanceName":"1"}),"instanceName":"1"});
            var Q41;
            Q41=makeQuery(id+"F8.opPattern","COPY",EDGE,{"derivedFrom":makeQuery(id+"F4.opLoft","SWEPT_EDGE",EDGE,{"disambiguationData":[OSD([sQuery(id+"F0.wireOp",EDGE,"E0.bottom"),sQuery(id+"F0.wireOp",EDGE,"E0.right"),sQuery(id+"F3.wireOp",EDGE,"E1.bottom"),sQuery(id+"F3.wireOp",EDGE,"E1.left")])]}),"instanceName":"1"});
            var Q42;
            Q42=makeQuery(id+"F8.opPattern","COPY",EDGE,{"derivedFrom":makeQuery(id+"F4.opLoft","SWEPT_EDGE",EDGE,{"disambiguationData":[OSD([sQuery(id+"F0.wireOp",EDGE,"E0.top"),sQuery(id+"F0.wireOp",EDGE,"E0.right"),sQuery(id+"F3.wireOp",EDGE,"E1.top"),sQuery(id+"F3.wireOp",EDGE,"E1.left")])]}),"instanceName":"1"});
            var Q43;
            {var subQ0=makeQuery(id+"F4.opLoft","MID_CAP_EDGE",EDGE,{"disambiguationData":[OSD([sQuery(id+"F3.wireOp",EDGE,"E1.top"),sQuery(id+"F3.wireOp",EDGE,"E1.left"),sQuery(id+"F3.wireOp",EDGE,"E1.right")])],"capPos":1.0});Q43=makeQuery(id+"F7.opPattern","COPY",EDGE,{"derivedFrom":makeQuery(id+"F5.boolean.opBoolean","MERGE",EDGE,{"derivedFrom":[subQ0,makeQuery(id+"F5.opPattern","COPY",EDGE,{"derivedFrom":subQ0,"instanceName":"1"})]}),"instanceName":"1"});}
            var Q44;
            {var subQ0=sQuery(id+"F3.wireOp",EDGE,"E1.right");var subQ1=sQuery(id+"F3.wireOp",EDGE,"E1.top");var subQ2=sQuery(id+"F0.wireOp",EDGE,"E0.left");var subQ3=sQuery(id+"F0.wireOp",EDGE,"E0.top");Q44=makeQuery(id+"F9.opShell","OFFSET_EDGE",EDGE,{"disambiguationData":[OSD([subQ3,subQ2,subQ1,subQ0]),TDD([makeQuery(id+"F5.opPattern","COPY",EDGE,{"derivedFrom":makeQuery(id+"F4.opLoft","SWEPT_EDGE",EDGE,{"disambiguationData":[OSD([subQ3,subQ2,subQ1,subQ0])]}),"instanceName":"1"})])]});}
            var Q45;
            {var subQ0=sQuery(id+"F3.wireOp",EDGE,"E1.right");var subQ1=sQuery(id+"F3.wireOp",EDGE,"E1.bottom");var subQ2=sQuery(id+"F0.wireOp",EDGE,"E0.left");var subQ3=sQuery(id+"F0.wireOp",EDGE,"E0.bottom");Q45=makeQuery(id+"F9.opShell","OFFSET_EDGE",EDGE,{"disambiguationData":[OSD([subQ3,subQ2,subQ1,subQ0]),TDD([makeQuery(id+"F5.opPattern","COPY",EDGE,{"derivedFrom":makeQuery(id+"F4.opLoft","SWEPT_EDGE",EDGE,{"disambiguationData":[OSD([subQ3,subQ2,subQ1,subQ0])]}),"instanceName":"1"})])]});}
            var Q46;
            {var subQ0=sQuery(id+"F3.wireOp",EDGE,"E1.right");var subQ1=sQuery(id+"F3.wireOp",EDGE,"E1.bottom");var subQ2=sQuery(id+"F0.wireOp",EDGE,"E0.left");var subQ3=sQuery(id+"F0.wireOp",EDGE,"E0.bottom");Q46=makeQuery(id+"F9.opShell","OFFSET_EDGE",EDGE,{"disambiguationData":[OSD([subQ3,subQ2,subQ1,subQ0]),TDD([makeQuery(id+"F6.opPattern","COPY",EDGE,{"derivedFrom":makeQuery(id+"F4.opLoft","SWEPT_EDGE",EDGE,{"disambiguationData":[OSD([subQ3,subQ2,subQ1,subQ0])]}),"instanceName":"1"})])]});}
            var Q47;
            {var subQ0=sQuery(id+"F3.wireOp",EDGE,"E1.right");var subQ1=sQuery(id+"F3.wireOp",EDGE,"E1.bottom");var subQ2=sQuery(id+"F0.wireOp",EDGE,"E0.left");var subQ3=sQuery(id+"F0.wireOp",EDGE,"E0.bottom");Q47=makeQuery(id+"F9.opShell","OFFSET_EDGE",EDGE,{"disambiguationData":[OSD([subQ3,subQ2,subQ1,subQ0]),TDD([makeQuery(id+"F4.opLoft","SWEPT_EDGE",EDGE,{"disambiguationData":[OSD([subQ3,subQ2,subQ1,subQ0])]})])]});}
            var Q48;
            {var subQ0=sQuery(id+"F3.wireOp",EDGE,"E1.left");var subQ1=sQuery(id+"F3.wireOp",EDGE,"E1.bottom");var subQ2=sQuery(id+"F0.wireOp",EDGE,"E0.right");var subQ3=sQuery(id+"F0.wireOp",EDGE,"E0.bottom");Q48=makeQuery(id+"F9.opShell","OFFSET_EDGE",EDGE,{"disambiguationData":[OSD([subQ3,subQ2,subQ1,subQ0]),TDD([makeQuery(id+"F7.opPattern","COPY",EDGE,{"derivedFrom":makeQuery(id+"F5.opPattern","COPY",EDGE,{"derivedFrom":makeQuery(id+"F4.opLoft","SWEPT_EDGE",EDGE,{"disambiguationData":[OSD([subQ3,subQ2,subQ1,subQ0])]}),"instanceName":"1"}),"instanceName":"1"})])]});}
            var Q49;
            {var subQ0=sQuery(id+"F3.wireOp",EDGE,"E1.right");var subQ1=sQuery(id+"F3.wireOp",EDGE,"E1.top");var subQ2=sQuery(id+"F0.wireOp",EDGE,"E0.left");var subQ3=sQuery(id+"F0.wireOp",EDGE,"E0.top");Q49=makeQuery(id+"F9.opShell","OFFSET_EDGE",EDGE,{"disambiguationData":[OSD([subQ3,subQ2,subQ1,subQ0]),TDD([makeQuery(id+"F7.opPattern","COPY",EDGE,{"derivedFrom":makeQuery(id+"F6.opPattern","COPY",EDGE,{"derivedFrom":makeQuery(id+"F5.opPattern","COPY",EDGE,{"derivedFrom":makeQuery(id+"F4.opLoft","SWEPT_EDGE",EDGE,{"disambiguationData":[OSD([subQ3,subQ2,subQ1,subQ0])]}),"instanceName":"1"}),"instanceName":"1"}),"instanceName":"1"})])]});}
            var Q50;
            Q50=makeQuery(id+"F7.opPattern","COPY",EDGE,{"derivedFrom":makeQuery(id+"F4.opLoft","SWEPT_EDGE",EDGE,{"disambiguationData":[OSD([sQuery(id+"F0.wireOp",EDGE,"E0.top"),sQuery(id+"F0.wireOp",EDGE,"E0.left"),sQuery(id+"F3.wireOp",EDGE,"E1.top"),sQuery(id+"F3.wireOp",EDGE,"E1.right")])]}),"instanceName":"1"});
            var Q51;
            Q51=makeQuery(id+"F4.opLoft","SWEPT_EDGE",EDGE,{"disambiguationData":[OSD([sQuery(id+"F0.wireOp",EDGE,"E0.top"),sQuery(id+"F0.wireOp",EDGE,"E0.left"),sQuery(id+"F3.wireOp",EDGE,"E1.top"),sQuery(id+"F3.wireOp",EDGE,"E1.right")])]});
            var Q52;
            Q52=makeQuery(id+"F6.opPattern","COPY",EDGE,{"derivedFrom":makeQuery(id+"F4.opLoft","MID_CAP_EDGE",EDGE,{"disambiguationData":[OSD([sQuery(id+"F0.wireOp",EDGE,"E0.bottom"),sQuery(id+"F0.wireOp",EDGE,"E0.top"),sQuery(id+"F0.wireOp",EDGE,"E0.left")])],"capPos":0.0}),"instanceName":"1"});
            var Q53;
            Q53=makeQuery(id+"F6.opPattern","COPY",EDGE,{"derivedFrom":makeQuery(id+"F5.opPattern","COPY",EDGE,{"derivedFrom":makeQuery(id+"F4.opLoft","SWEPT_EDGE",EDGE,{"disambiguationData":[OSD([sQuery(id+"F0.wireOp",EDGE,"E0.top"),sQuery(id+"F0.wireOp",EDGE,"E0.left"),sQuery(id+"F3.wireOp",EDGE,"E1.top"),sQuery(id+"F3.wireOp",EDGE,"E1.right")])]}),"instanceName":"1"}),"instanceName":"1"});
            var Q54;
            Q54=makeQuery(id+"F5.opPattern","COPY",EDGE,{"derivedFrom":makeQuery(id+"F4.opLoft","SWEPT_EDGE",EDGE,{"disambiguationData":[OSD([sQuery(id+"F0.wireOp",EDGE,"E0.top"),sQuery(id+"F0.wireOp",EDGE,"E0.left"),sQuery(id+"F3.wireOp",EDGE,"E1.top"),sQuery(id+"F3.wireOp",EDGE,"E1.right")])]}),"instanceName":"1"});
            var Q55;
            {var subQ0=makeQuery(id+"F4.opLoft","MID_CAP_EDGE",EDGE,{"disambiguationData":[OSD([sQuery(id+"F3.wireOp",EDGE,"E1.bottom"),sQuery(id+"F3.wireOp",EDGE,"E1.top"),sQuery(id+"F3.wireOp",EDGE,"E1.right")])],"capPos":1.0});Q55=makeQuery(id+"F5.boolean.opBoolean","MERGE",EDGE,{"derivedFrom":[subQ0,makeQuery(id+"F5.opPattern","COPY",EDGE,{"derivedFrom":subQ0,"instanceName":"1"})]});}
            var Q56;
            Q56=makeQuery(id+"F6.opPattern","COPY",EDGE,{"derivedFrom":makeQuery(id+"F4.opLoft","SWEPT_EDGE",EDGE,{"disambiguationData":[OSD([sQuery(id+"F0.wireOp",EDGE,"E0.top"),sQuery(id+"F0.wireOp",EDGE,"E0.left"),sQuery(id+"F3.wireOp",EDGE,"E1.top"),sQuery(id+"F3.wireOp",EDGE,"E1.right")])]}),"instanceName":"1"});
            var Q57;
            {var subQ0=makeQuery(id+"F5.opPattern","COPY",EDGE,{"derivedFrom":makeQuery(id+"F4.opLoft","MID_CAP_EDGE",EDGE,{"disambiguationData":[OSD([sQuery(id+"F0.wireOp",EDGE,"E0.bottom"),sQuery(id+"F0.wireOp",EDGE,"E0.top"),sQuery(id+"F0.wireOp",EDGE,"E0.left")])],"capPos":0.0}),"instanceName":"1"});Q57=makeQuery(id+"F6.boolean.opBoolean","MERGE",EDGE,{"derivedFrom":[subQ0,makeQuery(id+"F6.opPattern","COPY",EDGE,{"derivedFrom":subQ0,"instanceName":"1"})]});}
            var Q58;
            {var subQ0=makeQuery(id+"F4.opLoft","MID_CAP_EDGE",EDGE,{"disambiguationData":[OSD([sQuery(id+"F3.wireOp",EDGE,"E1.bottom"),sQuery(id+"F3.wireOp",EDGE,"E1.top"),sQuery(id+"F3.wireOp",EDGE,"E1.right")])],"capPos":1.0});Q58=makeQuery(id+"F6.opPattern","COPY",EDGE,{"derivedFrom":makeQuery(id+"F5.boolean.opBoolean","MERGE",EDGE,{"derivedFrom":[subQ0,makeQuery(id+"F5.opPattern","COPY",EDGE,{"derivedFrom":subQ0,"instanceName":"1"})]}),"instanceName":"1"});}
            var Q59;
            Q59=makeQuery(id+"F8.opPattern","COPY",EDGE,{"derivedFrom":makeQuery(id+"F5.opPattern","COPY",EDGE,{"derivedFrom":makeQuery(id+"F4.opLoft","SWEPT_EDGE",EDGE,{"disambiguationData":[OSD([sQuery(id+"F0.wireOp",EDGE,"E0.bottom"),sQuery(id+"F0.wireOp",EDGE,"E0.right"),sQuery(id+"F3.wireOp",EDGE,"E1.bottom"),sQuery(id+"F3.wireOp",EDGE,"E1.left")])]}),"instanceName":"1"}),"instanceName":"1"});
            var Q60;
            {var subQ0=sQuery(id+"F3.wireOp",EDGE,"E1.left");var subQ1=sQuery(id+"F3.wireOp",EDGE,"E1.top");var subQ2=sQuery(id+"F3.wireOp",EDGE,"E1.bottom");var subQ3=makeQuery(id+"F4.opLoft","MID_CAP_EDGE",EDGE,{"disambiguationData":[OSD([subQ2,subQ1,subQ0])],"capPos":1.0});Q60=makeQuery(id+"F9.opShell","OFFSET_EDGE",EDGE,{"disambiguationData":[OSD([subQ2,subQ1,subQ0]),TDD([makeQuery(id+"F8.opPattern","COPY",EDGE,{"derivedFrom":makeQuery(id+"F7.opPattern","COPY",EDGE,{"derivedFrom":makeQuery(id+"F5.boolean.opBoolean","MERGE",EDGE,{"derivedFrom":[subQ3,makeQuery(id+"F5.opPattern","COPY",EDGE,{"derivedFrom":subQ3,"instanceName":"1"})]}),"instanceName":"1"}),"instanceName":"1"})])]});}
            var Q61;
            {var subQ0=sQuery(id+"F0.wireOp",EDGE,"E0.right");var subQ1=sQuery(id+"F0.wireOp",EDGE,"E0.top");var subQ2=sQuery(id+"F0.wireOp",EDGE,"E0.bottom");var subQ3=makeQuery(id+"F5.opPattern","COPY",EDGE,{"derivedFrom":makeQuery(id+"F4.opLoft","MID_CAP_EDGE",EDGE,{"disambiguationData":[OSD([subQ2,subQ1,subQ0])],"capPos":0.0}),"instanceName":"1"});Q61=makeQuery(id+"F9.opShell","OFFSET_EDGE",EDGE,{"disambiguationData":[OSD([subQ2,subQ1,subQ0]),TDD([makeQuery(id+"F8.opPattern","COPY",EDGE,{"derivedFrom":makeQuery(id+"F7.opPattern","COPY",EDGE,{"derivedFrom":makeQuery(id+"F6.boolean.opBoolean","MERGE",EDGE,{"derivedFrom":[subQ3,makeQuery(id+"F6.opPattern","COPY",EDGE,{"derivedFrom":subQ3,"instanceName":"1"})]}),"instanceName":"1"}),"instanceName":"1"})])]});}
            var Q62;
            Q62=makeQuery(id+"F8.opPattern","COPY",EDGE,{"derivedFrom":makeQuery(id+"F7.opPattern","COPY",EDGE,{"derivedFrom":makeQuery(id+"F6.opPattern","COPY",EDGE,{"derivedFrom":makeQuery(id+"F5.opPattern","COPY",EDGE,{"derivedFrom":makeQuery(id+"F4.opLoft","SWEPT_EDGE",EDGE,{"disambiguationData":[OSD([sQuery(id+"F0.wireOp",EDGE,"E0.bottom"),sQuery(id+"F0.wireOp",EDGE,"E0.right"),sQuery(id+"F3.wireOp",EDGE,"E1.bottom"),sQuery(id+"F3.wireOp",EDGE,"E1.left")])]}),"instanceName":"1"}),"instanceName":"1"}),"instanceName":"1"}),"instanceName":"1"});
            var Q63;
            {var subQ0=sQuery(id+"F3.wireOp",EDGE,"E1.left");var subQ1=sQuery(id+"F3.wireOp",EDGE,"E1.top");var subQ2=sQuery(id+"F0.wireOp",EDGE,"E0.right");var subQ3=sQuery(id+"F0.wireOp",EDGE,"E0.top");Q63=makeQuery(id+"F9.opShell","OFFSET_EDGE",EDGE,{"disambiguationData":[OSD([subQ3,subQ2,subQ1,subQ0]),TDD([makeQuery(id+"F8.opPattern","COPY",EDGE,{"derivedFrom":makeQuery(id+"F7.opPattern","COPY",EDGE,{"derivedFrom":makeQuery(id+"F5.opPattern","COPY",EDGE,{"derivedFrom":makeQuery(id+"F4.opLoft","SWEPT_EDGE",EDGE,{"disambiguationData":[OSD([subQ3,subQ2,subQ1,subQ0])]}),"instanceName":"1"}),"instanceName":"1"}),"instanceName":"1"})])]});}
            var Q64;
            {var subQ0=sQuery(id+"F3.wireOp",EDGE,"E1.right");var subQ1=sQuery(id+"F3.wireOp",EDGE,"E1.left");var subQ2=sQuery(id+"F3.wireOp",EDGE,"E1.top");var subQ3=makeQuery(id+"F4.opLoft","MID_CAP_EDGE",EDGE,{"disambiguationData":[OSD([subQ2,subQ1,subQ0])],"capPos":1.0});Q64=makeQuery(id+"F9.opShell","OFFSET_EDGE",EDGE,{"disambiguationData":[OSD([subQ2,subQ1,subQ0]),TDD([makeQuery(id+"F8.opPattern","COPY",EDGE,{"derivedFrom":makeQuery(id+"F7.opPattern","COPY",EDGE,{"derivedFrom":makeQuery(id+"F6.opPattern","COPY",EDGE,{"derivedFrom":makeQuery(id+"F5.boolean.opBoolean","MERGE",EDGE,{"derivedFrom":[subQ3,makeQuery(id+"F5.opPattern","COPY",EDGE,{"derivedFrom":subQ3,"instanceName":"1"})]}),"instanceName":"1"}),"instanceName":"1"}),"instanceName":"1"})])]});}
            var Q65;
            {var subQ0=sQuery(id+"F3.wireOp",EDGE,"E1.left");var subQ1=sQuery(id+"F3.wireOp",EDGE,"E1.top");var subQ2=sQuery(id+"F0.wireOp",EDGE,"E0.right");var subQ3=sQuery(id+"F0.wireOp",EDGE,"E0.top");Q65=makeQuery(id+"F9.opShell","OFFSET_EDGE",EDGE,{"disambiguationData":[OSD([subQ3,subQ2,subQ1,subQ0]),TDD([makeQuery(id+"F8.opPattern","COPY",EDGE,{"derivedFrom":makeQuery(id+"F6.opPattern","COPY",EDGE,{"derivedFrom":makeQuery(id+"F5.opPattern","COPY",EDGE,{"derivedFrom":makeQuery(id+"F4.opLoft","SWEPT_EDGE",EDGE,{"disambiguationData":[OSD([subQ3,subQ2,subQ1,subQ0])]}),"instanceName":"1"}),"instanceName":"1"}),"instanceName":"1"})])]});}
            var Q66;
            {var subQ0=sQuery(id+"F3.wireOp",EDGE,"E1.right");var subQ1=sQuery(id+"F3.wireOp",EDGE,"E1.top");var subQ2=sQuery(id+"F3.wireOp",EDGE,"E1.bottom");var subQ3=makeQuery(id+"F4.opLoft","MID_CAP_EDGE",EDGE,{"disambiguationData":[OSD([subQ2,subQ1,subQ0])],"capPos":1.0});Q66=makeQuery(id+"F9.opShell","OFFSET_EDGE",EDGE,{"disambiguationData":[OSD([subQ2,subQ1,subQ0]),TDD([makeQuery(id+"F8.opPattern","COPY",EDGE,{"derivedFrom":makeQuery(id+"F7.opPattern","COPY",EDGE,{"derivedFrom":makeQuery(id+"F6.opPattern","COPY",EDGE,{"derivedFrom":makeQuery(id+"F5.boolean.opBoolean","MERGE",EDGE,{"derivedFrom":[subQ3,makeQuery(id+"F5.opPattern","COPY",EDGE,{"derivedFrom":subQ3,"instanceName":"1"})]}),"instanceName":"1"}),"instanceName":"1"}),"instanceName":"1"})])]});}
            var Q67;
            {var subQ0=sQuery(id+"F3.wireOp",EDGE,"E1.left");var subQ1=sQuery(id+"F3.wireOp",EDGE,"E1.top");var subQ2=sQuery(id+"F0.wireOp",EDGE,"E0.right");var subQ3=sQuery(id+"F0.wireOp",EDGE,"E0.top");Q67=makeQuery(id+"F9.opShell","OFFSET_EDGE",EDGE,{"disambiguationData":[OSD([subQ3,subQ2,subQ1,subQ0]),TDD([makeQuery(id+"F8.opPattern","COPY",EDGE,{"derivedFrom":makeQuery(id+"F7.opPattern","COPY",EDGE,{"derivedFrom":makeQuery(id+"F6.opPattern","COPY",EDGE,{"derivedFrom":makeQuery(id+"F5.opPattern","COPY",EDGE,{"derivedFrom":makeQuery(id+"F4.opLoft","SWEPT_EDGE",EDGE,{"disambiguationData":[OSD([subQ3,subQ2,subQ1,subQ0])]}),"instanceName":"1"}),"instanceName":"1"}),"instanceName":"1"}),"instanceName":"1"})])]});}
            var Q68;
            {var subQ0=sQuery(id+"F0.wireOp",EDGE,"E0.right");var subQ1=sQuery(id+"F0.wireOp",EDGE,"E0.top");var subQ2=sQuery(id+"F0.wireOp",EDGE,"E0.bottom");var subQ3=makeQuery(id+"F4.opLoft","MID_CAP_EDGE",EDGE,{"disambiguationData":[OSD([subQ2,subQ1,subQ0])],"capPos":0.0});Q68=makeQuery(id+"F9.opShell","OFFSET_EDGE",EDGE,{"disambiguationData":[OSD([subQ2,subQ1,subQ0]),TDD([makeQuery(id+"F8.opPattern","COPY",EDGE,{"derivedFrom":makeQuery(id+"F7.boolean.opBoolean","MERGE",EDGE,{"derivedFrom":[subQ3,makeQuery(id+"F7.opPattern","COPY",EDGE,{"derivedFrom":subQ3,"instanceName":"1"})]}),"instanceName":"1"})])]});}
            var Q69;
            {var subQ0=sQuery(id+"F0.wireOp",EDGE,"E0.right");var subQ1=sQuery(id+"F0.wireOp",EDGE,"E0.top");var subQ2=sQuery(id+"F0.wireOp",EDGE,"E0.bottom");var subQ3=makeQuery(id+"F5.opPattern","COPY",EDGE,{"derivedFrom":makeQuery(id+"F4.opLoft","MID_CAP_EDGE",EDGE,{"disambiguationData":[OSD([subQ2,subQ1,subQ0])],"capPos":0.0}),"instanceName":"1"});Q69=makeQuery(id+"F9.opShell","OFFSET_EDGE",EDGE,{"disambiguationData":[OSD([subQ2,subQ1,subQ0]),TDD([makeQuery(id+"F8.opPattern","COPY",EDGE,{"derivedFrom":makeQuery(id+"F6.boolean.opBoolean","MERGE",EDGE,{"derivedFrom":[subQ3,makeQuery(id+"F6.opPattern","COPY",EDGE,{"derivedFrom":subQ3,"instanceName":"1"})]}),"instanceName":"1"})])]});}
            var Q70;
            {var subQ0=sQuery(id+"F3.wireOp",EDGE,"E1.left");var subQ1=sQuery(id+"F3.wireOp",EDGE,"E1.top");var subQ2=sQuery(id+"F0.wireOp",EDGE,"E0.right");var subQ3=sQuery(id+"F0.wireOp",EDGE,"E0.top");Q70=makeQuery(id+"F9.opShell","OFFSET_EDGE",EDGE,{"disambiguationData":[OSD([subQ3,subQ2,subQ1,subQ0]),TDD([makeQuery(id+"F8.opPattern","COPY",EDGE,{"derivedFrom":makeQuery(id+"F7.opPattern","COPY",EDGE,{"derivedFrom":makeQuery(id+"F4.opLoft","SWEPT_EDGE",EDGE,{"disambiguationData":[OSD([subQ3,subQ2,subQ1,subQ0])]}),"instanceName":"1"}),"instanceName":"1"})])]});}
            var Q71;
            {var subQ0=sQuery(id+"F3.wireOp",EDGE,"E1.right");var subQ1=sQuery(id+"F3.wireOp",EDGE,"E1.top");var subQ2=sQuery(id+"F3.wireOp",EDGE,"E1.bottom");var subQ3=makeQuery(id+"F4.opLoft","MID_CAP_EDGE",EDGE,{"disambiguationData":[OSD([subQ2,subQ1,subQ0])],"capPos":1.0});Q71=makeQuery(id+"F9.opShell","OFFSET_EDGE",EDGE,{"disambiguationData":[OSD([subQ2,subQ1,subQ0]),TDD([makeQuery(id+"F7.opPattern","COPY",EDGE,{"derivedFrom":makeQuery(id+"F6.opPattern","COPY",EDGE,{"derivedFrom":makeQuery(id+"F5.boolean.opBoolean","MERGE",EDGE,{"derivedFrom":[subQ3,makeQuery(id+"F5.opPattern","COPY",EDGE,{"derivedFrom":subQ3,"instanceName":"1"})]}),"instanceName":"1"}),"instanceName":"1"})])]});}
            var Q72;
            {var subQ0=sQuery(id+"F0.wireOp",EDGE,"E0.left");var subQ1=sQuery(id+"F0.wireOp",EDGE,"E0.top");var subQ2=sQuery(id+"F0.wireOp",EDGE,"E0.bottom");var subQ3=makeQuery(id+"F4.opLoft","MID_CAP_EDGE",EDGE,{"disambiguationData":[OSD([subQ2,subQ1,subQ0])],"capPos":0.0});Q72=makeQuery(id+"F9.opShell","OFFSET_EDGE",EDGE,{"disambiguationData":[OSD([subQ2,subQ1,subQ0]),TDD([makeQuery(id+"F7.boolean.opBoolean","MERGE",EDGE,{"derivedFrom":[subQ3,makeQuery(id+"F7.opPattern","COPY",EDGE,{"derivedFrom":subQ3,"instanceName":"1"})]})])]});}
            var Q73;
            {var subQ0=sQuery(id+"F3.wireOp",EDGE,"E1.left");var subQ1=sQuery(id+"F3.wireOp",EDGE,"E1.top");var subQ2=sQuery(id+"F0.wireOp",EDGE,"E0.right");var subQ3=sQuery(id+"F0.wireOp",EDGE,"E0.top");Q73=makeQuery(id+"F9.opShell","OFFSET_EDGE",EDGE,{"disambiguationData":[OSD([subQ3,subQ2,subQ1,subQ0]),TDD([makeQuery(id+"F7.opPattern","COPY",EDGE,{"derivedFrom":makeQuery(id+"F6.opPattern","COPY",EDGE,{"derivedFrom":makeQuery(id+"F4.opLoft","SWEPT_EDGE",EDGE,{"disambiguationData":[OSD([subQ3,subQ2,subQ1,subQ0])]}),"instanceName":"1"}),"instanceName":"1"})])]});}
            var Q74;
            Q74=makeQuery(id+"F8.opPattern","COPY",EDGE,{"derivedFrom":makeQuery(id+"F6.opPattern","COPY",EDGE,{"derivedFrom":makeQuery(id+"F4.opLoft","SWEPT_EDGE",EDGE,{"disambiguationData":[OSD([sQuery(id+"F0.wireOp",EDGE,"E0.bottom"),sQuery(id+"F0.wireOp",EDGE,"E0.right"),sQuery(id+"F3.wireOp",EDGE,"E1.bottom"),sQuery(id+"F3.wireOp",EDGE,"E1.left")])]}),"instanceName":"1"}),"instanceName":"1"});
            var Q75;
            {var subQ0=sQuery(id+"F3.wireOp",EDGE,"E1.left");var subQ1=sQuery(id+"F3.wireOp",EDGE,"E1.top");var subQ2=sQuery(id+"F3.wireOp",EDGE,"E1.bottom");var subQ3=makeQuery(id+"F4.opLoft","MID_CAP_EDGE",EDGE,{"disambiguationData":[OSD([subQ2,subQ1,subQ0])],"capPos":1.0});Q75=makeQuery(id+"F9.opShell","OFFSET_EDGE",EDGE,{"disambiguationData":[OSD([subQ2,subQ1,subQ0]),TDD([makeQuery(id+"F5.boolean.opBoolean","MERGE",EDGE,{"derivedFrom":[subQ3,makeQuery(id+"F5.opPattern","COPY",EDGE,{"derivedFrom":subQ3,"instanceName":"1"})]})])]});}
            var Q76;
            {var subQ0=sQuery(id+"F3.wireOp",EDGE,"E1.left");var subQ1=sQuery(id+"F3.wireOp",EDGE,"E1.top");var subQ2=sQuery(id+"F0.wireOp",EDGE,"E0.right");var subQ3=sQuery(id+"F0.wireOp",EDGE,"E0.top");Q76=makeQuery(id+"F9.opShell","OFFSET_EDGE",EDGE,{"disambiguationData":[OSD([subQ3,subQ2,subQ1,subQ0]),TDD([makeQuery(id+"F8.opPattern","COPY",EDGE,{"derivedFrom":makeQuery(id+"F5.opPattern","COPY",EDGE,{"derivedFrom":makeQuery(id+"F4.opLoft","SWEPT_EDGE",EDGE,{"disambiguationData":[OSD([subQ3,subQ2,subQ1,subQ0])]}),"instanceName":"1"}),"instanceName":"1"})])]});}
            var Q77;
            {var subQ0=sQuery(id+"F3.wireOp",EDGE,"E1.left");var subQ1=sQuery(id+"F3.wireOp",EDGE,"E1.bottom");var subQ2=sQuery(id+"F0.wireOp",EDGE,"E0.right");var subQ3=sQuery(id+"F0.wireOp",EDGE,"E0.bottom");Q77=makeQuery(id+"F9.opShell","OFFSET_EDGE",EDGE,{"disambiguationData":[OSD([subQ3,subQ2,subQ1,subQ0]),TDD([makeQuery(id+"F7.opPattern","COPY",EDGE,{"derivedFrom":makeQuery(id+"F6.opPattern","COPY",EDGE,{"derivedFrom":makeQuery(id+"F4.opLoft","SWEPT_EDGE",EDGE,{"disambiguationData":[OSD([subQ3,subQ2,subQ1,subQ0])]}),"instanceName":"1"}),"instanceName":"1"})])]});}
            var Q78;
            {var subQ0=makeQuery(id+"F4.opLoft","MID_CAP_EDGE",EDGE,{"disambiguationData":[OSD([sQuery(id+"F3.wireOp",EDGE,"E1.bottom"),sQuery(id+"F3.wireOp",EDGE,"E1.top"),sQuery(id+"F3.wireOp",EDGE,"E1.left")])],"capPos":1.0});Q78=makeQuery(id+"F8.opPattern","COPY",EDGE,{"derivedFrom":makeQuery(id+"F7.opPattern","COPY",EDGE,{"derivedFrom":makeQuery(id+"F6.opPattern","COPY",EDGE,{"derivedFrom":makeQuery(id+"F5.boolean.opBoolean","MERGE",EDGE,{"derivedFrom":[subQ0,makeQuery(id+"F5.opPattern","COPY",EDGE,{"derivedFrom":subQ0,"instanceName":"1"})]}),"instanceName":"1"}),"instanceName":"1"}),"instanceName":"1"});}
            var Q79;
            Q79=makeQuery(id+"F8.opPattern","COPY",EDGE,{"derivedFrom":makeQuery(id+"F7.opPattern","COPY",EDGE,{"derivedFrom":makeQuery(id+"F4.opLoft","SWEPT_EDGE",EDGE,{"disambiguationData":[OSD([sQuery(id+"F0.wireOp",EDGE,"E0.bottom"),sQuery(id+"F0.wireOp",EDGE,"E0.right"),sQuery(id+"F3.wireOp",EDGE,"E1.bottom"),sQuery(id+"F3.wireOp",EDGE,"E1.left")])]}),"instanceName":"1"}),"instanceName":"1"});
            var Q80;
            {var subQ0=sQuery(id+"F3.wireOp",EDGE,"E1.left");var subQ1=sQuery(id+"F3.wireOp",EDGE,"E1.bottom");var subQ2=sQuery(id+"F0.wireOp",EDGE,"E0.right");var subQ3=sQuery(id+"F0.wireOp",EDGE,"E0.bottom");Q80=makeQuery(id+"F9.opShell","OFFSET_EDGE",EDGE,{"disambiguationData":[OSD([subQ3,subQ2,subQ1,subQ0]),TDD([makeQuery(id+"F8.opPattern","COPY",EDGE,{"derivedFrom":makeQuery(id+"F7.opPattern","COPY",EDGE,{"derivedFrom":makeQuery(id+"F6.opPattern","COPY",EDGE,{"derivedFrom":makeQuery(id+"F4.opLoft","SWEPT_EDGE",EDGE,{"disambiguationData":[OSD([subQ3,subQ2,subQ1,subQ0])]}),"instanceName":"1"}),"instanceName":"1"}),"instanceName":"1"})])]});}
            var Q81;
            {var subQ0=makeQuery(id+"F4.opLoft","MID_CAP_EDGE",EDGE,{"disambiguationData":[OSD([sQuery(id+"F3.wireOp",EDGE,"E1.top"),sQuery(id+"F3.wireOp",EDGE,"E1.left"),sQuery(id+"F3.wireOp",EDGE,"E1.right")])],"capPos":1.0});Q81=makeQuery(id+"F8.opPattern","COPY",EDGE,{"derivedFrom":makeQuery(id+"F7.opPattern","COPY",EDGE,{"derivedFrom":makeQuery(id+"F6.opPattern","COPY",EDGE,{"derivedFrom":makeQuery(id+"F5.boolean.opBoolean","MERGE",EDGE,{"derivedFrom":[subQ0,makeQuery(id+"F5.opPattern","COPY",EDGE,{"derivedFrom":subQ0,"instanceName":"1"})]}),"instanceName":"1"}),"instanceName":"1"}),"instanceName":"1"});}
            var Q82;
            Q82=makeQuery(id+"F8.opPattern","COPY",EDGE,{"derivedFrom":makeQuery(id+"F7.opPattern","COPY",EDGE,{"derivedFrom":makeQuery(id+"F6.opPattern","COPY",EDGE,{"derivedFrom":makeQuery(id+"F5.opPattern","COPY",EDGE,{"derivedFrom":makeQuery(id+"F4.opLoft","SWEPT_EDGE",EDGE,{"disambiguationData":[OSD([sQuery(id+"F0.wireOp",EDGE,"E0.top"),sQuery(id+"F0.wireOp",EDGE,"E0.right"),sQuery(id+"F3.wireOp",EDGE,"E1.top"),sQuery(id+"F3.wireOp",EDGE,"E1.left")])]}),"instanceName":"1"}),"instanceName":"1"}),"instanceName":"1"}),"instanceName":"1"});
            var Q83;
            {var subQ0=sQuery(id+"F3.wireOp",EDGE,"E1.right");var subQ1=sQuery(id+"F3.wireOp",EDGE,"E1.top");var subQ2=sQuery(id+"F3.wireOp",EDGE,"E1.bottom");var subQ3=makeQuery(id+"F4.opLoft","MID_CAP_EDGE",EDGE,{"disambiguationData":[OSD([subQ2,subQ1,subQ0])],"capPos":1.0});Q83=makeQuery(id+"F9.opShell","OFFSET_EDGE",EDGE,{"disambiguationData":[OSD([subQ2,subQ1,subQ0]),TDD([makeQuery(id+"F6.opPattern","COPY",EDGE,{"derivedFrom":makeQuery(id+"F5.boolean.opBoolean","MERGE",EDGE,{"derivedFrom":[subQ3,makeQuery(id+"F5.opPattern","COPY",EDGE,{"derivedFrom":subQ3,"instanceName":"1"})]}),"instanceName":"1"})])]});}
            var Q84;
            {var subQ0=sQuery(id+"F3.wireOp",EDGE,"E1.right");var subQ1=sQuery(id+"F3.wireOp",EDGE,"E1.left");var subQ2=sQuery(id+"F3.wireOp",EDGE,"E1.top");var subQ3=makeQuery(id+"F4.opLoft","MID_CAP_EDGE",EDGE,{"disambiguationData":[OSD([subQ2,subQ1,subQ0])],"capPos":1.0});Q84=makeQuery(id+"F9.opShell","OFFSET_EDGE",EDGE,{"disambiguationData":[OSD([subQ2,subQ1,subQ0]),TDD([makeQuery(id+"F7.opPattern","COPY",EDGE,{"derivedFrom":makeQuery(id+"F5.boolean.opBoolean","MERGE",EDGE,{"derivedFrom":[subQ3,makeQuery(id+"F5.opPattern","COPY",EDGE,{"derivedFrom":subQ3,"instanceName":"1"})]}),"instanceName":"1"})])]});}
            var Q85;
            {var subQ0=sQuery(id+"F3.wireOp",EDGE,"E1.right");var subQ1=sQuery(id+"F3.wireOp",EDGE,"E1.left");var subQ2=sQuery(id+"F3.wireOp",EDGE,"E1.top");var subQ3=makeQuery(id+"F4.opLoft","MID_CAP_EDGE",EDGE,{"disambiguationData":[OSD([subQ2,subQ1,subQ0])],"capPos":1.0});Q85=makeQuery(id+"F9.opShell","OFFSET_EDGE",EDGE,{"disambiguationData":[OSD([subQ2,subQ1,subQ0]),TDD([makeQuery(id+"F7.opPattern","COPY",EDGE,{"derivedFrom":makeQuery(id+"F6.opPattern","COPY",EDGE,{"derivedFrom":makeQuery(id+"F5.boolean.opBoolean","MERGE",EDGE,{"derivedFrom":[subQ3,makeQuery(id+"F5.opPattern","COPY",EDGE,{"derivedFrom":subQ3,"instanceName":"1"})]}),"instanceName":"1"}),"instanceName":"1"})])]});}
            var Q86;
            {var subQ0=sQuery(id+"F3.wireOp",EDGE,"E1.left");var subQ1=sQuery(id+"F3.wireOp",EDGE,"E1.top");var subQ2=sQuery(id+"F3.wireOp",EDGE,"E1.bottom");var subQ3=makeQuery(id+"F4.opLoft","MID_CAP_EDGE",EDGE,{"disambiguationData":[OSD([subQ2,subQ1,subQ0])],"capPos":1.0});Q86=makeQuery(id+"F9.opShell","OFFSET_EDGE",EDGE,{"disambiguationData":[OSD([subQ2,subQ1,subQ0]),TDD([makeQuery(id+"F7.opPattern","COPY",EDGE,{"derivedFrom":makeQuery(id+"F5.boolean.opBoolean","MERGE",EDGE,{"derivedFrom":[subQ3,makeQuery(id+"F5.opPattern","COPY",EDGE,{"derivedFrom":subQ3,"instanceName":"1"})]}),"instanceName":"1"})])]});}
            var Q87;
            {var subQ0=sQuery(id+"F3.wireOp",EDGE,"E1.left");var subQ1=sQuery(id+"F3.wireOp",EDGE,"E1.bottom");var subQ2=sQuery(id+"F0.wireOp",EDGE,"E0.right");var subQ3=sQuery(id+"F0.wireOp",EDGE,"E0.bottom");Q87=makeQuery(id+"F9.opShell","OFFSET_EDGE",EDGE,{"disambiguationData":[OSD([subQ3,subQ2,subQ1,subQ0]),TDD([makeQuery(id+"F8.opPattern","COPY",EDGE,{"derivedFrom":makeQuery(id+"F5.opPattern","COPY",EDGE,{"derivedFrom":makeQuery(id+"F4.opLoft","SWEPT_EDGE",EDGE,{"disambiguationData":[OSD([subQ3,subQ2,subQ1,subQ0])]}),"instanceName":"1"}),"instanceName":"1"})])]});}
            var Q88;
            Q88=makeQuery(id+"F8.opPattern","COPY",EDGE,{"derivedFrom":makeQuery(id+"F5.opPattern","COPY",EDGE,{"derivedFrom":makeQuery(id+"F4.opLoft","SWEPT_EDGE",EDGE,{"disambiguationData":[OSD([sQuery(id+"F0.wireOp",EDGE,"E0.top"),sQuery(id+"F0.wireOp",EDGE,"E0.right"),sQuery(id+"F3.wireOp",EDGE,"E1.top"),sQuery(id+"F3.wireOp",EDGE,"E1.left")])]}),"instanceName":"1"}),"instanceName":"1"});
            var Q89;
            {var subQ0=sQuery(id+"F3.wireOp",EDGE,"E1.right");var subQ1=sQuery(id+"F3.wireOp",EDGE,"E1.top");var subQ2=sQuery(id+"F0.wireOp",EDGE,"E0.left");var subQ3=sQuery(id+"F0.wireOp",EDGE,"E0.top");Q89=makeQuery(id+"F9.opShell","OFFSET_EDGE",EDGE,{"disambiguationData":[OSD([subQ3,subQ2,subQ1,subQ0]),TDD([makeQuery(id+"F7.opPattern","COPY",EDGE,{"derivedFrom":makeQuery(id+"F4.opLoft","SWEPT_EDGE",EDGE,{"disambiguationData":[OSD([subQ3,subQ2,subQ1,subQ0])]}),"instanceName":"1"})])]});}
            var Q90;
            Q90=makeQuery(id+"F8.opPattern","COPY",EDGE,{"derivedFrom":makeQuery(id+"F6.opPattern","COPY",EDGE,{"derivedFrom":makeQuery(id+"F4.opLoft","SWEPT_EDGE",EDGE,{"disambiguationData":[OSD([sQuery(id+"F0.wireOp",EDGE,"E0.top"),sQuery(id+"F0.wireOp",EDGE,"E0.right"),sQuery(id+"F3.wireOp",EDGE,"E1.top"),sQuery(id+"F3.wireOp",EDGE,"E1.left")])]}),"instanceName":"1"}),"instanceName":"1"});
            var Q91;
            {var subQ0=sQuery(id+"F3.wireOp",EDGE,"E1.left");var subQ1=sQuery(id+"F3.wireOp",EDGE,"E1.bottom");var subQ2=sQuery(id+"F0.wireOp",EDGE,"E0.right");var subQ3=sQuery(id+"F0.wireOp",EDGE,"E0.bottom");Q91=makeQuery(id+"F9.opShell","OFFSET_EDGE",EDGE,{"disambiguationData":[OSD([subQ3,subQ2,subQ1,subQ0]),TDD([makeQuery(id+"F8.opPattern","COPY",EDGE,{"derivedFrom":makeQuery(id+"F7.opPattern","COPY",EDGE,{"derivedFrom":makeQuery(id+"F6.opPattern","COPY",EDGE,{"derivedFrom":makeQuery(id+"F5.opPattern","COPY",EDGE,{"derivedFrom":makeQuery(id+"F4.opLoft","SWEPT_EDGE",EDGE,{"disambiguationData":[OSD([subQ3,subQ2,subQ1,subQ0])]}),"instanceName":"1"}),"instanceName":"1"}),"instanceName":"1"}),"instanceName":"1"})])]});}
            var Q92;
            {var subQ0=sQuery(id+"F3.wireOp",EDGE,"E1.right");var subQ1=sQuery(id+"F3.wireOp",EDGE,"E1.left");var subQ2=sQuery(id+"F3.wireOp",EDGE,"E1.top");var subQ3=makeQuery(id+"F4.opLoft","MID_CAP_EDGE",EDGE,{"disambiguationData":[OSD([subQ2,subQ1,subQ0])],"capPos":1.0});Q92=makeQuery(id+"F9.opShell","OFFSET_EDGE",EDGE,{"disambiguationData":[OSD([subQ2,subQ1,subQ0]),TDD([makeQuery(id+"F5.boolean.opBoolean","MERGE",EDGE,{"derivedFrom":[subQ3,makeQuery(id+"F5.opPattern","COPY",EDGE,{"derivedFrom":subQ3,"instanceName":"1"})]})])]});}
            var Q93;
            {var subQ0=sQuery(id+"F3.wireOp",EDGE,"E1.right");var subQ1=sQuery(id+"F3.wireOp",EDGE,"E1.bottom");var subQ2=sQuery(id+"F0.wireOp",EDGE,"E0.left");var subQ3=sQuery(id+"F0.wireOp",EDGE,"E0.bottom");Q93=makeQuery(id+"F9.opShell","OFFSET_EDGE",EDGE,{"disambiguationData":[OSD([subQ3,subQ2,subQ1,subQ0]),TDD([makeQuery(id+"F7.opPattern","COPY",EDGE,{"derivedFrom":makeQuery(id+"F4.opLoft","SWEPT_EDGE",EDGE,{"disambiguationData":[OSD([subQ3,subQ2,subQ1,subQ0])]}),"instanceName":"1"})])]});}
            var Q94;
            {var subQ0=sQuery(id+"F0.wireOp",EDGE,"E0.left");var subQ1=sQuery(id+"F0.wireOp",EDGE,"E0.top");var subQ2=sQuery(id+"F0.wireOp",EDGE,"E0.bottom");Q94=makeQuery(id+"F9.opShell","OFFSET_EDGE",EDGE,{"disambiguationData":[OSD([subQ2,subQ1,subQ0]),TDD([makeQuery(id+"F6.opPattern","COPY",EDGE,{"derivedFrom":makeQuery(id+"F4.opLoft","MID_CAP_EDGE",EDGE,{"disambiguationData":[OSD([subQ2,subQ1,subQ0])],"capPos":0.0}),"instanceName":"1"})])]});}
            var Q95;
            {var subQ0=sQuery(id+"F3.wireOp",EDGE,"E1.left");var subQ1=sQuery(id+"F3.wireOp",EDGE,"E1.top");var subQ2=sQuery(id+"F0.wireOp",EDGE,"E0.right");var subQ3=sQuery(id+"F0.wireOp",EDGE,"E0.top");Q95=makeQuery(id+"F9.opShell","OFFSET_EDGE",EDGE,{"disambiguationData":[OSD([subQ3,subQ2,subQ1,subQ0]),TDD([makeQuery(id+"F8.opPattern","COPY",EDGE,{"derivedFrom":makeQuery(id+"F4.opLoft","SWEPT_EDGE",EDGE,{"disambiguationData":[OSD([subQ3,subQ2,subQ1,subQ0])]}),"instanceName":"1"})])]});}
            var Q96;
            {var subQ0=sQuery(id+"F3.wireOp",EDGE,"E1.left");var subQ1=sQuery(id+"F3.wireOp",EDGE,"E1.bottom");var subQ2=sQuery(id+"F0.wireOp",EDGE,"E0.right");var subQ3=sQuery(id+"F0.wireOp",EDGE,"E0.bottom");Q96=makeQuery(id+"F9.opShell","OFFSET_EDGE",EDGE,{"disambiguationData":[OSD([subQ3,subQ2,subQ1,subQ0]),TDD([makeQuery(id+"F8.opPattern","COPY",EDGE,{"derivedFrom":makeQuery(id+"F4.opLoft","SWEPT_EDGE",EDGE,{"disambiguationData":[OSD([subQ3,subQ2,subQ1,subQ0])]}),"instanceName":"1"})])]});}
            var Q97;
            {var subQ0=sQuery(id+"F3.wireOp",EDGE,"E1.left");var subQ1=sQuery(id+"F3.wireOp",EDGE,"E1.top");var subQ2=sQuery(id+"F3.wireOp",EDGE,"E1.bottom");var subQ3=makeQuery(id+"F4.opLoft","MID_CAP_EDGE",EDGE,{"disambiguationData":[OSD([subQ2,subQ1,subQ0])],"capPos":1.0});Q97=makeQuery(id+"F9.opShell","OFFSET_EDGE",EDGE,{"disambiguationData":[OSD([subQ2,subQ1,subQ0]),TDD([makeQuery(id+"F8.opPattern","COPY",EDGE,{"derivedFrom":makeQuery(id+"F5.boolean.opBoolean","MERGE",EDGE,{"derivedFrom":[subQ3,makeQuery(id+"F5.opPattern","COPY",EDGE,{"derivedFrom":subQ3,"instanceName":"1"})]}),"instanceName":"1"})])]});}
            var Q98;
            {var subQ0=sQuery(id+"F3.wireOp",EDGE,"E1.left");var subQ1=sQuery(id+"F3.wireOp",EDGE,"E1.top");var subQ2=sQuery(id+"F3.wireOp",EDGE,"E1.bottom");var subQ3=makeQuery(id+"F4.opLoft","MID_CAP_EDGE",EDGE,{"disambiguationData":[OSD([subQ2,subQ1,subQ0])],"capPos":1.0});Q98=makeQuery(id+"F9.opShell","OFFSET_EDGE",EDGE,{"disambiguationData":[OSD([subQ2,subQ1,subQ0]),TDD([makeQuery(id+"F8.opPattern","COPY",EDGE,{"derivedFrom":makeQuery(id+"F7.opPattern","COPY",EDGE,{"derivedFrom":makeQuery(id+"F6.opPattern","COPY",EDGE,{"derivedFrom":makeQuery(id+"F5.boolean.opBoolean","MERGE",EDGE,{"derivedFrom":[subQ3,makeQuery(id+"F5.opPattern","COPY",EDGE,{"derivedFrom":subQ3,"instanceName":"1"})]}),"instanceName":"1"}),"instanceName":"1"}),"instanceName":"1"})])]});}
            var Q99;
            {var subQ0=makeQuery(id+"F4.opLoft","MID_CAP_EDGE",EDGE,{"disambiguationData":[OSD([sQuery(id+"F3.wireOp",EDGE,"E1.bottom"),sQuery(id+"F3.wireOp",EDGE,"E1.top"),sQuery(id+"F3.wireOp",EDGE,"E1.left")])],"capPos":1.0});Q99=makeQuery(id+"F8.opPattern","COPY",EDGE,{"derivedFrom":makeQuery(id+"F7.opPattern","COPY",EDGE,{"derivedFrom":makeQuery(id+"F5.boolean.opBoolean","MERGE",EDGE,{"derivedFrom":[subQ0,makeQuery(id+"F5.opPattern","COPY",EDGE,{"derivedFrom":subQ0,"instanceName":"1"})]}),"instanceName":"1"}),"instanceName":"1"});}
            var Q100;
            {var subQ0=makeQuery(id+"F4.opLoft","MID_CAP_EDGE",EDGE,{"disambiguationData":[OSD([sQuery(id+"F3.wireOp",EDGE,"E1.bottom"),sQuery(id+"F3.wireOp",EDGE,"E1.top"),sQuery(id+"F3.wireOp",EDGE,"E1.left")])],"capPos":1.0});Q100=makeQuery(id+"F8.opPattern","COPY",EDGE,{"derivedFrom":makeQuery(id+"F5.boolean.opBoolean","MERGE",EDGE,{"derivedFrom":[subQ0,makeQuery(id+"F5.opPattern","COPY",EDGE,{"derivedFrom":subQ0,"instanceName":"1"})]}),"instanceName":"1"});}
            var Q101;
            {var subQ0=makeQuery(id+"F4.opLoft","MID_CAP_EDGE",EDGE,{"disambiguationData":[OSD([sQuery(id+"F3.wireOp",EDGE,"E1.bottom"),sQuery(id+"F3.wireOp",EDGE,"E1.top"),sQuery(id+"F3.wireOp",EDGE,"E1.left")])],"capPos":1.0});Q101=makeQuery(id+"F8.opPattern","COPY",EDGE,{"derivedFrom":makeQuery(id+"F6.opPattern","COPY",EDGE,{"derivedFrom":makeQuery(id+"F5.boolean.opBoolean","MERGE",EDGE,{"derivedFrom":[subQ0,makeQuery(id+"F5.opPattern","COPY",EDGE,{"derivedFrom":subQ0,"instanceName":"1"})]}),"instanceName":"1"}),"instanceName":"1"});}
            var Q102;
            {var subQ0=sQuery(id+"F3.wireOp",EDGE,"E1.right");var subQ1=sQuery(id+"F3.wireOp",EDGE,"E1.top");var subQ2=sQuery(id+"F3.wireOp",EDGE,"E1.bottom");var subQ3=makeQuery(id+"F4.opLoft","MID_CAP_EDGE",EDGE,{"disambiguationData":[OSD([subQ2,subQ1,subQ0])],"capPos":1.0});Q102=makeQuery(id+"F9.opShell","OFFSET_EDGE",EDGE,{"disambiguationData":[OSD([subQ2,subQ1,subQ0]),TDD([makeQuery(id+"F5.boolean.opBoolean","MERGE",EDGE,{"derivedFrom":[subQ3,makeQuery(id+"F5.opPattern","COPY",EDGE,{"derivedFrom":subQ3,"instanceName":"1"})]})])]});}
            var Q103;
            {var subQ0=sQuery(id+"F3.wireOp",EDGE,"E1.right");var subQ1=sQuery(id+"F3.wireOp",EDGE,"E1.top");var subQ2=sQuery(id+"F3.wireOp",EDGE,"E1.bottom");var subQ3=makeQuery(id+"F4.opLoft","MID_CAP_EDGE",EDGE,{"disambiguationData":[OSD([subQ2,subQ1,subQ0])],"capPos":1.0});Q103=makeQuery(id+"F9.opShell","OFFSET_EDGE",EDGE,{"disambiguationData":[OSD([subQ2,subQ1,subQ0]),TDD([makeQuery(id+"F7.opPattern","COPY",EDGE,{"derivedFrom":makeQuery(id+"F5.boolean.opBoolean","MERGE",EDGE,{"derivedFrom":[subQ3,makeQuery(id+"F5.opPattern","COPY",EDGE,{"derivedFrom":subQ3,"instanceName":"1"})]}),"instanceName":"1"})])]});}
            var Q104;
            {var subQ0=sQuery(id+"F3.wireOp",EDGE,"E1.left");var subQ1=sQuery(id+"F3.wireOp",EDGE,"E1.top");var subQ2=sQuery(id+"F3.wireOp",EDGE,"E1.bottom");var subQ3=makeQuery(id+"F4.opLoft","MID_CAP_EDGE",EDGE,{"disambiguationData":[OSD([subQ2,subQ1,subQ0])],"capPos":1.0});Q104=makeQuery(id+"F9.opShell","OFFSET_EDGE",EDGE,{"disambiguationData":[OSD([subQ2,subQ1,subQ0]),TDD([makeQuery(id+"F7.opPattern","COPY",EDGE,{"derivedFrom":makeQuery(id+"F6.opPattern","COPY",EDGE,{"derivedFrom":makeQuery(id+"F5.boolean.opBoolean","MERGE",EDGE,{"derivedFrom":[subQ3,makeQuery(id+"F5.opPattern","COPY",EDGE,{"derivedFrom":subQ3,"instanceName":"1"})]}),"instanceName":"1"}),"instanceName":"1"})])]});}
            var Q105;
            Q105=makeQuery(id+"F4.opLoft","SWEPT_EDGE",EDGE,{"disambiguationData":[OSD([sQuery(id+"F0.wireOp",EDGE,"E0.bottom"),sQuery(id+"F0.wireOp",EDGE,"E0.left"),sQuery(id+"F3.wireOp",EDGE,"E1.bottom"),sQuery(id+"F3.wireOp",EDGE,"E1.right")])]});
            var Q106;
            Q106=makeQuery(id+"F7.opPattern","COPY",EDGE,{"derivedFrom":makeQuery(id+"F4.opLoft","SWEPT_EDGE",EDGE,{"disambiguationData":[OSD([sQuery(id+"F0.wireOp",EDGE,"E0.top"),sQuery(id+"F0.wireOp",EDGE,"E0.right"),sQuery(id+"F3.wireOp",EDGE,"E1.top"),sQuery(id+"F3.wireOp",EDGE,"E1.left")])]}),"instanceName":"1"});
            var Q107;
            Q107=makeQuery(id+"F6.opPattern","COPY",EDGE,{"derivedFrom":makeQuery(id+"F4.opLoft","MID_CAP_EDGE",EDGE,{"disambiguationData":[OSD([sQuery(id+"F0.wireOp",EDGE,"E0.bottom"),sQuery(id+"F0.wireOp",EDGE,"E0.left"),sQuery(id+"F0.wireOp",EDGE,"E0.right")])],"capPos":0.0}),"instanceName":"1"});
            var Q108;
            Q108=makeQuery(id+"F5.opPattern","COPY",EDGE,{"derivedFrom":makeQuery(id+"F4.opLoft","SWEPT_EDGE",EDGE,{"disambiguationData":[OSD([sQuery(id+"F0.wireOp",EDGE,"E0.top"),sQuery(id+"F0.wireOp",EDGE,"E0.right"),sQuery(id+"F3.wireOp",EDGE,"E1.top"),sQuery(id+"F3.wireOp",EDGE,"E1.left")])]}),"instanceName":"1"});
            var Q109;
            Q109=makeQuery(id+"F6.opPattern","COPY",EDGE,{"derivedFrom":makeQuery(id+"F4.opLoft","MID_CAP_EDGE",EDGE,{"disambiguationData":[OSD([sQuery(id+"F0.wireOp",EDGE,"E0.bottom"),sQuery(id+"F0.wireOp",EDGE,"E0.top"),sQuery(id+"F0.wireOp",EDGE,"E0.right")])],"capPos":0.0}),"instanceName":"1"});
            var Q110;
            Q110=makeQuery(id+"F6.opPattern","COPY",EDGE,{"derivedFrom":makeQuery(id+"F4.opLoft","SWEPT_EDGE",EDGE,{"disambiguationData":[OSD([sQuery(id+"F0.wireOp",EDGE,"E0.bottom"),sQuery(id+"F0.wireOp",EDGE,"E0.right"),sQuery(id+"F3.wireOp",EDGE,"E1.bottom"),sQuery(id+"F3.wireOp",EDGE,"E1.left")])]}),"instanceName":"1"});
            var Q111;
            Q111=makeQuery(id+"F6.opPattern","COPY",EDGE,{"derivedFrom":makeQuery(id+"F4.opLoft","SWEPT_EDGE",EDGE,{"disambiguationData":[OSD([sQuery(id+"F0.wireOp",EDGE,"E0.top"),sQuery(id+"F0.wireOp",EDGE,"E0.right"),sQuery(id+"F3.wireOp",EDGE,"E1.top"),sQuery(id+"F3.wireOp",EDGE,"E1.left")])]}),"instanceName":"1"});
            var Q112;
            Q112=makeQuery(id+"F6.opPattern","COPY",EDGE,{"derivedFrom":makeQuery(id+"F5.opPattern","COPY",EDGE,{"derivedFrom":makeQuery(id+"F4.opLoft","SWEPT_EDGE",EDGE,{"disambiguationData":[OSD([sQuery(id+"F0.wireOp",EDGE,"E0.bottom"),sQuery(id+"F0.wireOp",EDGE,"E0.right"),sQuery(id+"F3.wireOp",EDGE,"E1.bottom"),sQuery(id+"F3.wireOp",EDGE,"E1.left")])]}),"instanceName":"1"}),"instanceName":"1"});
            var Q113;
            {var subQ0=makeQuery(id+"F5.opPattern","COPY",EDGE,{"derivedFrom":makeQuery(id+"F4.opLoft","MID_CAP_EDGE",EDGE,{"disambiguationData":[OSD([sQuery(id+"F0.wireOp",EDGE,"E0.bottom"),sQuery(id+"F0.wireOp",EDGE,"E0.left"),sQuery(id+"F0.wireOp",EDGE,"E0.right")])],"capPos":0.0}),"instanceName":"1"});Q113=makeQuery(id+"F6.boolean.opBoolean","MERGE",EDGE,{"derivedFrom":[subQ0,makeQuery(id+"F6.opPattern","COPY",EDGE,{"derivedFrom":subQ0,"instanceName":"1"})]});}
            var Q114;
            {var subQ0=makeQuery(id+"F5.opPattern","COPY",EDGE,{"derivedFrom":makeQuery(id+"F4.opLoft","MID_CAP_EDGE",EDGE,{"disambiguationData":[OSD([sQuery(id+"F0.wireOp",EDGE,"E0.bottom"),sQuery(id+"F0.wireOp",EDGE,"E0.top"),sQuery(id+"F0.wireOp",EDGE,"E0.right")])],"capPos":0.0}),"instanceName":"1"});Q114=makeQuery(id+"F6.boolean.opBoolean","MERGE",EDGE,{"derivedFrom":[subQ0,makeQuery(id+"F6.opPattern","COPY",EDGE,{"derivedFrom":subQ0,"instanceName":"1"})]});}
            var Q115;
            {var subQ0=makeQuery(id+"F4.opLoft","MID_CAP_EDGE",EDGE,{"disambiguationData":[OSD([sQuery(id+"F3.wireOp",EDGE,"E1.bottom"),sQuery(id+"F3.wireOp",EDGE,"E1.left"),sQuery(id+"F3.wireOp",EDGE,"E1.right")])],"capPos":1.0});Q115=makeQuery(id+"F6.opPattern","COPY",EDGE,{"derivedFrom":makeQuery(id+"F5.boolean.opBoolean","MERGE",EDGE,{"derivedFrom":[subQ0,makeQuery(id+"F5.opPattern","COPY",EDGE,{"derivedFrom":subQ0,"instanceName":"1"})]}),"instanceName":"1"});}
            var Q116;
            Q116=makeQuery(id+"F7.opPattern","COPY",EDGE,{"derivedFrom":makeQuery(id+"F4.opLoft","SWEPT_EDGE",EDGE,{"disambiguationData":[OSD([sQuery(id+"F0.wireOp",EDGE,"E0.bottom"),sQuery(id+"F0.wireOp",EDGE,"E0.right"),sQuery(id+"F3.wireOp",EDGE,"E1.bottom"),sQuery(id+"F3.wireOp",EDGE,"E1.left")])]}),"instanceName":"1"});
            var Q117;
            Q117=makeQuery(id+"F8.opPattern","COPY",EDGE,{"derivedFrom":makeQuery(id+"F5.opPattern","COPY",EDGE,{"derivedFrom":makeQuery(id+"F4.opLoft","SWEPT_EDGE",EDGE,{"disambiguationData":[OSD([sQuery(id+"F0.wireOp",EDGE,"E0.bottom"),sQuery(id+"F0.wireOp",EDGE,"E0.left"),sQuery(id+"F3.wireOp",EDGE,"E1.bottom"),sQuery(id+"F3.wireOp",EDGE,"E1.right")])]}),"instanceName":"1"}),"instanceName":"1"});
            var Q118;
            {var subQ0=sQuery(id+"F0.wireOp",EDGE,"E0.right");var subQ1=sQuery(id+"F0.wireOp",EDGE,"E0.left");var subQ2=sQuery(id+"F0.wireOp",EDGE,"E0.top");Q118=makeQuery(id+"F9.opShell","OFFSET_EDGE",EDGE,{"disambiguationData":[OSD([subQ2,subQ1,subQ0]),TDD([makeQuery(id+"F8.opPattern","COPY",EDGE,{"derivedFrom":makeQuery(id+"F6.opPattern","COPY",EDGE,{"derivedFrom":makeQuery(id+"F4.opLoft","MID_CAP_EDGE",EDGE,{"disambiguationData":[OSD([subQ2,subQ1,subQ0])],"capPos":0.0}),"instanceName":"1"}),"instanceName":"1"})])]});}
            var Q119;
            {var subQ0=makeQuery(id+"F4.opLoft","MID_CAP_EDGE",EDGE,{"disambiguationData":[OSD([sQuery(id+"F0.wireOp",EDGE,"E0.bottom"),sQuery(id+"F0.wireOp",EDGE,"E0.left"),sQuery(id+"F0.wireOp",EDGE,"E0.right")])],"capPos":0.0});Q119=makeQuery(id+"F8.opPattern","COPY",EDGE,{"derivedFrom":makeQuery(id+"F7.boolean.opBoolean","MERGE",EDGE,{"derivedFrom":[subQ0,makeQuery(id+"F7.opPattern","COPY",EDGE,{"derivedFrom":subQ0,"instanceName":"1"})]}),"instanceName":"1"});}
            var Q120;
            Q120=makeQuery(id+"F7.opPattern","COPY",EDGE,{"derivedFrom":makeQuery(id+"F5.opPattern","COPY",EDGE,{"derivedFrom":makeQuery(id+"F4.opLoft","SWEPT_EDGE",EDGE,{"disambiguationData":[OSD([sQuery(id+"F0.wireOp",EDGE,"E0.bottom"),sQuery(id+"F0.wireOp",EDGE,"E0.left"),sQuery(id+"F3.wireOp",EDGE,"E1.bottom"),sQuery(id+"F3.wireOp",EDGE,"E1.right")])]}),"instanceName":"1"}),"instanceName":"1"});
            var Q121;
            {var subQ0=makeQuery(id+"F5.opPattern","COPY",EDGE,{"derivedFrom":makeQuery(id+"F4.opLoft","MID_CAP_EDGE",EDGE,{"disambiguationData":[OSD([sQuery(id+"F0.wireOp",EDGE,"E0.bottom"),sQuery(id+"F0.wireOp",EDGE,"E0.left"),sQuery(id+"F0.wireOp",EDGE,"E0.right")])],"capPos":0.0}),"instanceName":"1"});Q121=makeQuery(id+"F8.opPattern","COPY",EDGE,{"derivedFrom":makeQuery(id+"F6.boolean.opBoolean","MERGE",EDGE,{"derivedFrom":[subQ0,makeQuery(id+"F6.opPattern","COPY",EDGE,{"derivedFrom":subQ0,"instanceName":"1"})]}),"instanceName":"1"});}
            var Q122;
            {var subQ0=makeQuery(id+"F5.opPattern","COPY",EDGE,{"derivedFrom":makeQuery(id+"F4.opLoft","MID_CAP_EDGE",EDGE,{"disambiguationData":[OSD([sQuery(id+"F0.wireOp",EDGE,"E0.bottom"),sQuery(id+"F0.wireOp",EDGE,"E0.left"),sQuery(id+"F0.wireOp",EDGE,"E0.right")])],"capPos":0.0}),"instanceName":"1"});Q122=makeQuery(id+"F8.opPattern","COPY",EDGE,{"derivedFrom":makeQuery(id+"F7.opPattern","COPY",EDGE,{"derivedFrom":makeQuery(id+"F6.boolean.opBoolean","MERGE",EDGE,{"derivedFrom":[subQ0,makeQuery(id+"F6.opPattern","COPY",EDGE,{"derivedFrom":subQ0,"instanceName":"1"})]}),"instanceName":"1"}),"instanceName":"1"});}
            var Q123;
            {var subQ0=makeQuery(id+"F4.opLoft","MID_CAP_EDGE",EDGE,{"disambiguationData":[OSD([sQuery(id+"F3.wireOp",EDGE,"E1.bottom"),sQuery(id+"F3.wireOp",EDGE,"E1.left"),sQuery(id+"F3.wireOp",EDGE,"E1.right")])],"capPos":1.0});Q123=makeQuery(id+"F8.opPattern","COPY",EDGE,{"derivedFrom":makeQuery(id+"F7.opPattern","COPY",EDGE,{"derivedFrom":makeQuery(id+"F5.boolean.opBoolean","MERGE",EDGE,{"derivedFrom":[subQ0,makeQuery(id+"F5.opPattern","COPY",EDGE,{"derivedFrom":subQ0,"instanceName":"1"})]}),"instanceName":"1"}),"instanceName":"1"});}
            var Q124;
            {var subQ0=makeQuery(id+"F4.opLoft","MID_CAP_EDGE",EDGE,{"disambiguationData":[OSD([sQuery(id+"F3.wireOp",EDGE,"E1.bottom"),sQuery(id+"F3.wireOp",EDGE,"E1.left"),sQuery(id+"F3.wireOp",EDGE,"E1.right")])],"capPos":1.0});Q124=makeQuery(id+"F8.opPattern","COPY",EDGE,{"derivedFrom":makeQuery(id+"F7.opPattern","COPY",EDGE,{"derivedFrom":makeQuery(id+"F6.opPattern","COPY",EDGE,{"derivedFrom":makeQuery(id+"F5.boolean.opBoolean","MERGE",EDGE,{"derivedFrom":[subQ0,makeQuery(id+"F5.opPattern","COPY",EDGE,{"derivedFrom":subQ0,"instanceName":"1"})]}),"instanceName":"1"}),"instanceName":"1"}),"instanceName":"1"});}
            var Q125;
            {var subQ0=makeQuery(id+"F4.opLoft","MID_CAP_EDGE",EDGE,{"disambiguationData":[OSD([sQuery(id+"F3.wireOp",EDGE,"E1.bottom"),sQuery(id+"F3.wireOp",EDGE,"E1.left"),sQuery(id+"F3.wireOp",EDGE,"E1.right")])],"capPos":1.0});Q125=makeQuery(id+"F8.opPattern","COPY",EDGE,{"derivedFrom":makeQuery(id+"F6.opPattern","COPY",EDGE,{"derivedFrom":makeQuery(id+"F5.boolean.opBoolean","MERGE",EDGE,{"derivedFrom":[subQ0,makeQuery(id+"F5.opPattern","COPY",EDGE,{"derivedFrom":subQ0,"instanceName":"1"})]}),"instanceName":"1"}),"instanceName":"1"});}
            var Q126;
            Q126=makeQuery(id+"F8.opPattern","COPY",EDGE,{"derivedFrom":makeQuery(id+"F7.opPattern","COPY",EDGE,{"derivedFrom":makeQuery(id+"F6.opPattern","COPY",EDGE,{"derivedFrom":makeQuery(id+"F5.opPattern","COPY",EDGE,{"derivedFrom":makeQuery(id+"F4.opLoft","SWEPT_EDGE",EDGE,{"disambiguationData":[OSD([sQuery(id+"F0.wireOp",EDGE,"E0.bottom"),sQuery(id+"F0.wireOp",EDGE,"E0.left"),sQuery(id+"F3.wireOp",EDGE,"E1.bottom"),sQuery(id+"F3.wireOp",EDGE,"E1.right")])]}),"instanceName":"1"}),"instanceName":"1"}),"instanceName":"1"}),"instanceName":"1"});
            var Q127;
            {var subQ0=makeQuery(id+"F4.opLoft","MID_CAP_EDGE",EDGE,{"disambiguationData":[OSD([sQuery(id+"F3.wireOp",EDGE,"E1.bottom"),sQuery(id+"F3.wireOp",EDGE,"E1.left"),sQuery(id+"F3.wireOp",EDGE,"E1.right")])],"capPos":1.0});Q127=makeQuery(id+"F8.opPattern","COPY",EDGE,{"derivedFrom":makeQuery(id+"F5.boolean.opBoolean","MERGE",EDGE,{"derivedFrom":[subQ0,makeQuery(id+"F5.opPattern","COPY",EDGE,{"derivedFrom":subQ0,"instanceName":"1"})]}),"instanceName":"1"});}
            var Q128;
            {var subQ0=makeQuery(id+"F7.opPattern","COPY",EDGE,{"derivedFrom":makeQuery(id+"F6.opPattern","COPY",EDGE,{"derivedFrom":makeQuery(id+"F4.opLoft","MID_CAP_EDGE",EDGE,{"disambiguationData":[OSD([sQuery(id+"F0.wireOp",EDGE,"E0.bottom"),sQuery(id+"F0.wireOp",EDGE,"E0.left"),sQuery(id+"F0.wireOp",EDGE,"E0.right")])],"capPos":0.0}),"instanceName":"1"}),"instanceName":"1"});Q128=makeQuery(id+"F8.boolean.opBoolean","MERGE",EDGE,{"derivedFrom":[subQ0,makeQuery(id+"F8.opPattern","COPY",EDGE,{"derivedFrom":subQ0,"instanceName":"1"})]});}
            var Q129;
            Q129=makeQuery(id+"F8.opPattern","COPY",EDGE,{"derivedFrom":makeQuery(id+"F7.opPattern","COPY",EDGE,{"derivedFrom":makeQuery(id+"F4.opLoft","SWEPT_EDGE",EDGE,{"disambiguationData":[OSD([sQuery(id+"F0.wireOp",EDGE,"E0.bottom"),sQuery(id+"F0.wireOp",EDGE,"E0.left"),sQuery(id+"F3.wireOp",EDGE,"E1.bottom"),sQuery(id+"F3.wireOp",EDGE,"E1.right")])]}),"instanceName":"1"}),"instanceName":"1"});
            var Q130;
            Q130=makeQuery(id+"F8.opPattern","COPY",EDGE,{"derivedFrom":makeQuery(id+"F6.opPattern","COPY",EDGE,{"derivedFrom":makeQuery(id+"F4.opLoft","SWEPT_EDGE",EDGE,{"disambiguationData":[OSD([sQuery(id+"F0.wireOp",EDGE,"E0.bottom"),sQuery(id+"F0.wireOp",EDGE,"E0.left"),sQuery(id+"F3.wireOp",EDGE,"E1.bottom"),sQuery(id+"F3.wireOp",EDGE,"E1.right")])]}),"instanceName":"1"}),"instanceName":"1"});
            var Q131;
            {var subQ0=makeQuery(id+"F4.opLoft","MID_CAP_EDGE",EDGE,{"disambiguationData":[OSD([sQuery(id+"F0.wireOp",EDGE,"E0.bottom"),sQuery(id+"F0.wireOp",EDGE,"E0.left"),sQuery(id+"F0.wireOp",EDGE,"E0.right")])],"capPos":0.0});Q131=makeQuery(id+"F7.boolean.opBoolean","MERGE",EDGE,{"derivedFrom":[subQ0,makeQuery(id+"F7.opPattern","COPY",EDGE,{"derivedFrom":subQ0,"instanceName":"1"})]});}
            var Q132;
            Q132=makeQuery(id+"F8.opPattern","COPY",EDGE,{"derivedFrom":makeQuery(id+"F6.opPattern","COPY",EDGE,{"derivedFrom":makeQuery(id+"F4.opLoft","MID_CAP_EDGE",EDGE,{"disambiguationData":[OSD([sQuery(id+"F0.wireOp",EDGE,"E0.bottom"),sQuery(id+"F0.wireOp",EDGE,"E0.top"),sQuery(id+"F0.wireOp",EDGE,"E0.left")])],"capPos":0.0}),"instanceName":"1"}),"instanceName":"1"});
            var Q133;
            Q133=makeQuery(id+"F8.opPattern","COPY",EDGE,{"derivedFrom":makeQuery(id+"F7.opPattern","COPY",EDGE,{"derivedFrom":makeQuery(id+"F5.opPattern","COPY",EDGE,{"derivedFrom":makeQuery(id+"F4.opLoft","SWEPT_EDGE",EDGE,{"disambiguationData":[OSD([sQuery(id+"F0.wireOp",EDGE,"E0.bottom"),sQuery(id+"F0.wireOp",EDGE,"E0.left"),sQuery(id+"F3.wireOp",EDGE,"E1.bottom"),sQuery(id+"F3.wireOp",EDGE,"E1.right")])]}),"instanceName":"1"}),"instanceName":"1"}),"instanceName":"1"});
            var Q134;
            {var subQ0=makeQuery(id+"F4.opLoft","MID_CAP_EDGE",EDGE,{"disambiguationData":[OSD([sQuery(id+"F0.wireOp",EDGE,"E0.bottom"),sQuery(id+"F0.wireOp",EDGE,"E0.top"),sQuery(id+"F0.wireOp",EDGE,"E0.right")])],"capPos":0.0});Q134=makeQuery(id+"F7.boolean.opBoolean","MERGE",EDGE,{"derivedFrom":[subQ0,makeQuery(id+"F7.opPattern","COPY",EDGE,{"derivedFrom":subQ0,"instanceName":"1"})]});}
            var Q135;
            Q135=makeQuery(id+"F7.opPattern","COPY",EDGE,{"derivedFrom":makeQuery(id+"F6.opPattern","COPY",EDGE,{"derivedFrom":makeQuery(id+"F4.opLoft","SWEPT_EDGE",EDGE,{"disambiguationData":[OSD([sQuery(id+"F0.wireOp",EDGE,"E0.bottom"),sQuery(id+"F0.wireOp",EDGE,"E0.left"),sQuery(id+"F3.wireOp",EDGE,"E1.bottom"),sQuery(id+"F3.wireOp",EDGE,"E1.right")])]}),"instanceName":"1"}),"instanceName":"1"});
            var Q136;
            {var subQ0=makeQuery(id+"F5.opPattern","COPY",EDGE,{"derivedFrom":makeQuery(id+"F4.opLoft","MID_CAP_EDGE",EDGE,{"disambiguationData":[OSD([sQuery(id+"F0.wireOp",EDGE,"E0.bottom"),sQuery(id+"F0.wireOp",EDGE,"E0.top"),sQuery(id+"F0.wireOp",EDGE,"E0.right")])],"capPos":0.0}),"instanceName":"1"});Q136=makeQuery(id+"F7.opPattern","COPY",EDGE,{"derivedFrom":makeQuery(id+"F6.boolean.opBoolean","MERGE",EDGE,{"derivedFrom":[subQ0,makeQuery(id+"F6.opPattern","COPY",EDGE,{"derivedFrom":subQ0,"instanceName":"1"})]}),"instanceName":"1"});}
            var Q137;
            Q137=makeQuery(id+"F7.opPattern","COPY",EDGE,{"derivedFrom":makeQuery(id+"F6.opPattern","COPY",EDGE,{"derivedFrom":makeQuery(id+"F5.opPattern","COPY",EDGE,{"derivedFrom":makeQuery(id+"F4.opLoft","SWEPT_EDGE",EDGE,{"disambiguationData":[OSD([sQuery(id+"F0.wireOp",EDGE,"E0.top"),sQuery(id+"F0.wireOp",EDGE,"E0.right"),sQuery(id+"F3.wireOp",EDGE,"E1.top"),sQuery(id+"F3.wireOp",EDGE,"E1.left")])]}),"instanceName":"1"}),"instanceName":"1"}),"instanceName":"1"});
            var Q138;
            {var subQ0=makeQuery(id+"F5.opPattern","COPY",EDGE,{"derivedFrom":makeQuery(id+"F4.opLoft","MID_CAP_EDGE",EDGE,{"disambiguationData":[OSD([sQuery(id+"F0.wireOp",EDGE,"E0.bottom"),sQuery(id+"F0.wireOp",EDGE,"E0.left"),sQuery(id+"F0.wireOp",EDGE,"E0.right")])],"capPos":0.0}),"instanceName":"1"});Q138=makeQuery(id+"F7.opPattern","COPY",EDGE,{"derivedFrom":makeQuery(id+"F6.boolean.opBoolean","MERGE",EDGE,{"derivedFrom":[subQ0,makeQuery(id+"F6.opPattern","COPY",EDGE,{"derivedFrom":subQ0,"instanceName":"1"})]}),"instanceName":"1"});}
            var Q139;
            {var subQ0=makeQuery(id+"F7.opPattern","COPY",EDGE,{"derivedFrom":makeQuery(id+"F6.opPattern","COPY",EDGE,{"derivedFrom":makeQuery(id+"F4.opLoft","MID_CAP_EDGE",EDGE,{"disambiguationData":[OSD([sQuery(id+"F0.wireOp",EDGE,"E0.bottom"),sQuery(id+"F0.wireOp",EDGE,"E0.top"),sQuery(id+"F0.wireOp",EDGE,"E0.right")])],"capPos":0.0}),"instanceName":"1"}),"instanceName":"1"});Q139=makeQuery(id+"F8.boolean.opBoolean","MERGE",EDGE,{"derivedFrom":[subQ0,makeQuery(id+"F8.opPattern","COPY",EDGE,{"derivedFrom":subQ0,"instanceName":"1"})]});}
            var Q140;
            Q140=makeQuery(id+"F8.opPattern","COPY",EDGE,{"derivedFrom":makeQuery(id+"F6.opPattern","COPY",EDGE,{"derivedFrom":makeQuery(id+"F4.opLoft","MID_CAP_EDGE",EDGE,{"disambiguationData":[OSD([sQuery(id+"F0.wireOp",EDGE,"E0.bottom"),sQuery(id+"F0.wireOp",EDGE,"E0.left"),sQuery(id+"F0.wireOp",EDGE,"E0.right")])],"capPos":0.0}),"instanceName":"1"}),"instanceName":"1"});
            var Q141;
            {var subQ0=sQuery(id+"F3.wireOp",EDGE,"E1.right");var subQ1=sQuery(id+"F3.wireOp",EDGE,"E1.bottom");var subQ2=sQuery(id+"F0.wireOp",EDGE,"E0.left");var subQ3=sQuery(id+"F0.wireOp",EDGE,"E0.bottom");Q141=makeQuery(id+"F9.opShell","OFFSET_EDGE",EDGE,{"disambiguationData":[OSD([subQ3,subQ2,subQ1,subQ0]),TDD([makeQuery(id+"F7.opPattern","COPY",EDGE,{"derivedFrom":makeQuery(id+"F6.opPattern","COPY",EDGE,{"derivedFrom":makeQuery(id+"F4.opLoft","SWEPT_EDGE",EDGE,{"disambiguationData":[OSD([subQ3,subQ2,subQ1,subQ0])]}),"instanceName":"1"}),"instanceName":"1"})])]});}
            var Q142;
            Q142=makeQuery(id+"F4.opLoft","SWEPT_EDGE",EDGE,{"disambiguationData":[OSD([sQuery(id+"F0.wireOp",EDGE,"E0.bottom"),sQuery(id+"F0.wireOp",EDGE,"E0.right"),sQuery(id+"F3.wireOp",EDGE,"E1.bottom"),sQuery(id+"F3.wireOp",EDGE,"E1.left")])]});
            var Q143;
            {var subQ0=sQuery(id+"F0.wireOp",EDGE,"E0.right");var subQ1=sQuery(id+"F0.wireOp",EDGE,"E0.left");var subQ2=sQuery(id+"F0.wireOp",EDGE,"E0.bottom");var subQ3=makeQuery(id+"F4.opLoft","MID_CAP_EDGE",EDGE,{"disambiguationData":[OSD([subQ2,subQ1,subQ0])],"capPos":0.0});Q143=makeQuery(id+"F9.opShell","OFFSET_EDGE",EDGE,{"disambiguationData":[OSD([subQ2,subQ1,subQ0]),TDD([makeQuery(id+"F7.boolean.opBoolean","MERGE",EDGE,{"derivedFrom":[subQ3,makeQuery(id+"F7.opPattern","COPY",EDGE,{"derivedFrom":subQ3,"instanceName":"1"})]})])]});}
            var Q144;
            Q144=makeQuery(id+"F4.opLoft","SWEPT_EDGE",EDGE,{"disambiguationData":[OSD([sQuery(id+"F0.wireOp",EDGE,"E0.top"),sQuery(id+"F0.wireOp",EDGE,"E0.right"),sQuery(id+"F3.wireOp",EDGE,"E1.top"),sQuery(id+"F3.wireOp",EDGE,"E1.left")])]});
            var Q145;
            Q145=makeQuery(id+"F6.opPattern","COPY",EDGE,{"derivedFrom":makeQuery(id+"F5.opPattern","COPY",EDGE,{"derivedFrom":makeQuery(id+"F4.opLoft","SWEPT_EDGE",EDGE,{"disambiguationData":[OSD([sQuery(id+"F0.wireOp",EDGE,"E0.top"),sQuery(id+"F0.wireOp",EDGE,"E0.right"),sQuery(id+"F3.wireOp",EDGE,"E1.top"),sQuery(id+"F3.wireOp",EDGE,"E1.left")])]}),"instanceName":"1"}),"instanceName":"1"});
            var Q146;
            Q146=makeQuery(id+"F5.opPattern","COPY",EDGE,{"derivedFrom":makeQuery(id+"F4.opLoft","SWEPT_EDGE",EDGE,{"disambiguationData":[OSD([sQuery(id+"F0.wireOp",EDGE,"E0.bottom"),sQuery(id+"F0.wireOp",EDGE,"E0.right"),sQuery(id+"F3.wireOp",EDGE,"E1.bottom"),sQuery(id+"F3.wireOp",EDGE,"E1.left")])]}),"instanceName":"1"});
            var Q147;
            Q147=makeQuery(id+"F6.opPattern","COPY",EDGE,{"derivedFrom":makeQuery(id+"F4.opLoft","MID_CAP_EDGE",EDGE,{"disambiguationData":[OSD([sQuery(id+"F0.wireOp",EDGE,"E0.top"),sQuery(id+"F0.wireOp",EDGE,"E0.left"),sQuery(id+"F0.wireOp",EDGE,"E0.right")])],"capPos":0.0}),"instanceName":"1"});
            var Q148;
            {var subQ0=makeQuery(id+"F5.opPattern","COPY",EDGE,{"derivedFrom":makeQuery(id+"F4.opLoft","MID_CAP_EDGE",EDGE,{"disambiguationData":[OSD([sQuery(id+"F0.wireOp",EDGE,"E0.top"),sQuery(id+"F0.wireOp",EDGE,"E0.left"),sQuery(id+"F0.wireOp",EDGE,"E0.right")])],"capPos":0.0}),"instanceName":"1"});Q148=makeQuery(id+"F6.boolean.opBoolean","MERGE",EDGE,{"derivedFrom":[subQ0,makeQuery(id+"F6.opPattern","COPY",EDGE,{"derivedFrom":subQ0,"instanceName":"1"})]});}
            var Q149;
            {var subQ0=makeQuery(id+"F4.opLoft","MID_CAP_EDGE",EDGE,{"disambiguationData":[OSD([sQuery(id+"F3.wireOp",EDGE,"E1.bottom"),sQuery(id+"F3.wireOp",EDGE,"E1.top"),sQuery(id+"F3.wireOp",EDGE,"E1.left")])],"capPos":1.0});Q149=makeQuery(id+"F6.opPattern","COPY",EDGE,{"derivedFrom":makeQuery(id+"F5.boolean.opBoolean","MERGE",EDGE,{"derivedFrom":[subQ0,makeQuery(id+"F5.opPattern","COPY",EDGE,{"derivedFrom":subQ0,"instanceName":"1"})]}),"instanceName":"1"});}
            var Q150;
            Q150=makeQuery(id+"F7.opPattern","COPY",EDGE,{"derivedFrom":makeQuery(id+"F4.opLoft","SWEPT_EDGE",EDGE,{"disambiguationData":[OSD([sQuery(id+"F0.wireOp",EDGE,"E0.bottom"),sQuery(id+"F0.wireOp",EDGE,"E0.left"),sQuery(id+"F3.wireOp",EDGE,"E1.bottom"),sQuery(id+"F3.wireOp",EDGE,"E1.right")])]}),"instanceName":"1"});
            var Q151;
            {var subQ0=sQuery(id+"F0.wireOp",EDGE,"E0.right");var subQ1=sQuery(id+"F0.wireOp",EDGE,"E0.left");var subQ2=sQuery(id+"F0.wireOp",EDGE,"E0.bottom");var subQ3=makeQuery(id+"F4.opLoft","MID_CAP_EDGE",EDGE,{"disambiguationData":[OSD([subQ2,subQ1,subQ0])],"capPos":0.0});Q151=makeQuery(id+"F9.opShell","OFFSET_EDGE",EDGE,{"disambiguationData":[OSD([subQ2,subQ1,subQ0]),TDD([makeQuery(id+"F8.opPattern","COPY",EDGE,{"derivedFrom":makeQuery(id+"F7.boolean.opBoolean","MERGE",EDGE,{"derivedFrom":[subQ3,makeQuery(id+"F7.opPattern","COPY",EDGE,{"derivedFrom":subQ3,"instanceName":"1"})]}),"instanceName":"1"})])]});}
            var Q152;
            {var subQ0=sQuery(id+"F3.wireOp",EDGE,"E1.right");var subQ1=sQuery(id+"F3.wireOp",EDGE,"E1.left");var subQ2=sQuery(id+"F3.wireOp",EDGE,"E1.bottom");var subQ3=makeQuery(id+"F4.opLoft","MID_CAP_EDGE",EDGE,{"disambiguationData":[OSD([subQ2,subQ1,subQ0])],"capPos":1.0});Q152=makeQuery(id+"F9.opShell","OFFSET_EDGE",EDGE,{"disambiguationData":[OSD([subQ2,subQ1,subQ0]),TDD([makeQuery(id+"F8.opPattern","COPY",EDGE,{"derivedFrom":makeQuery(id+"F7.opPattern","COPY",EDGE,{"derivedFrom":makeQuery(id+"F5.boolean.opBoolean","MERGE",EDGE,{"derivedFrom":[subQ3,makeQuery(id+"F5.opPattern","COPY",EDGE,{"derivedFrom":subQ3,"instanceName":"1"})]}),"instanceName":"1"}),"instanceName":"1"})])]});}
            var Q153;
            {var subQ0=sQuery(id+"F3.wireOp",EDGE,"E1.right");var subQ1=sQuery(id+"F3.wireOp",EDGE,"E1.left");var subQ2=sQuery(id+"F3.wireOp",EDGE,"E1.bottom");var subQ3=makeQuery(id+"F4.opLoft","MID_CAP_EDGE",EDGE,{"disambiguationData":[OSD([subQ2,subQ1,subQ0])],"capPos":1.0});Q153=makeQuery(id+"F9.opShell","OFFSET_EDGE",EDGE,{"disambiguationData":[OSD([subQ2,subQ1,subQ0]),TDD([makeQuery(id+"F8.opPattern","COPY",EDGE,{"derivedFrom":makeQuery(id+"F6.opPattern","COPY",EDGE,{"derivedFrom":makeQuery(id+"F5.boolean.opBoolean","MERGE",EDGE,{"derivedFrom":[subQ3,makeQuery(id+"F5.opPattern","COPY",EDGE,{"derivedFrom":subQ3,"instanceName":"1"})]}),"instanceName":"1"}),"instanceName":"1"})])]});}
            var Q154;
            Q154=makeQuery(id+"F8.opPattern","COPY",EDGE,{"derivedFrom":makeQuery(id+"F4.opLoft","SWEPT_EDGE",EDGE,{"disambiguationData":[OSD([sQuery(id+"F0.wireOp",EDGE,"E0.bottom"),sQuery(id+"F0.wireOp",EDGE,"E0.left"),sQuery(id+"F3.wireOp",EDGE,"E1.bottom"),sQuery(id+"F3.wireOp",EDGE,"E1.right")])]}),"instanceName":"1"});
            var Q155;
            {var subQ0=sQuery(id+"F0.wireOp",EDGE,"E0.right");var subQ1=sQuery(id+"F0.wireOp",EDGE,"E0.left");var subQ2=sQuery(id+"F0.wireOp",EDGE,"E0.bottom");var subQ3=makeQuery(id+"F5.opPattern","COPY",EDGE,{"derivedFrom":makeQuery(id+"F4.opLoft","MID_CAP_EDGE",EDGE,{"disambiguationData":[OSD([subQ2,subQ1,subQ0])],"capPos":0.0}),"instanceName":"1"});Q155=makeQuery(id+"F9.opShell","OFFSET_EDGE",EDGE,{"disambiguationData":[OSD([subQ2,subQ1,subQ0]),TDD([makeQuery(id+"F8.opPattern","COPY",EDGE,{"derivedFrom":makeQuery(id+"F7.opPattern","COPY",EDGE,{"derivedFrom":makeQuery(id+"F6.boolean.opBoolean","MERGE",EDGE,{"derivedFrom":[subQ3,makeQuery(id+"F6.opPattern","COPY",EDGE,{"derivedFrom":subQ3,"instanceName":"1"})]}),"instanceName":"1"}),"instanceName":"1"})])]});}
            var Q156;
            {var subQ0=sQuery(id+"F3.wireOp",EDGE,"E1.right");var subQ1=sQuery(id+"F3.wireOp",EDGE,"E1.left");var subQ2=sQuery(id+"F3.wireOp",EDGE,"E1.bottom");var subQ3=makeQuery(id+"F4.opLoft","MID_CAP_EDGE",EDGE,{"disambiguationData":[OSD([subQ2,subQ1,subQ0])],"capPos":1.0});Q156=makeQuery(id+"F9.opShell","OFFSET_EDGE",EDGE,{"disambiguationData":[OSD([subQ2,subQ1,subQ0]),TDD([makeQuery(id+"F8.opPattern","COPY",EDGE,{"derivedFrom":makeQuery(id+"F5.boolean.opBoolean","MERGE",EDGE,{"derivedFrom":[subQ3,makeQuery(id+"F5.opPattern","COPY",EDGE,{"derivedFrom":subQ3,"instanceName":"1"})]}),"instanceName":"1"})])]});}
            var Q157;
            {var subQ0=sQuery(id+"F3.wireOp",EDGE,"E1.right");var subQ1=sQuery(id+"F3.wireOp",EDGE,"E1.bottom");var subQ2=sQuery(id+"F0.wireOp",EDGE,"E0.left");var subQ3=sQuery(id+"F0.wireOp",EDGE,"E0.bottom");Q157=makeQuery(id+"F9.opShell","OFFSET_EDGE",EDGE,{"disambiguationData":[OSD([subQ3,subQ2,subQ1,subQ0]),TDD([makeQuery(id+"F8.opPattern","COPY",EDGE,{"derivedFrom":makeQuery(id+"F6.opPattern","COPY",EDGE,{"derivedFrom":makeQuery(id+"F5.opPattern","COPY",EDGE,{"derivedFrom":makeQuery(id+"F4.opLoft","SWEPT_EDGE",EDGE,{"disambiguationData":[OSD([subQ3,subQ2,subQ1,subQ0])]}),"instanceName":"1"}),"instanceName":"1"}),"instanceName":"1"})])]});}
            var Q158;
            {var subQ0=sQuery(id+"F3.wireOp",EDGE,"E1.right");var subQ1=sQuery(id+"F3.wireOp",EDGE,"E1.top");var subQ2=sQuery(id+"F0.wireOp",EDGE,"E0.left");var subQ3=sQuery(id+"F0.wireOp",EDGE,"E0.top");Q158=makeQuery(id+"F9.opShell","OFFSET_EDGE",EDGE,{"disambiguationData":[OSD([subQ3,subQ2,subQ1,subQ0]),TDD([makeQuery(id+"F8.opPattern","COPY",EDGE,{"derivedFrom":makeQuery(id+"F6.opPattern","COPY",EDGE,{"derivedFrom":makeQuery(id+"F4.opLoft","SWEPT_EDGE",EDGE,{"disambiguationData":[OSD([subQ3,subQ2,subQ1,subQ0])]}),"instanceName":"1"}),"instanceName":"1"})])]});}
            var Q159;
            {var subQ0=sQuery(id+"F3.wireOp",EDGE,"E1.right");var subQ1=sQuery(id+"F3.wireOp",EDGE,"E1.bottom");var subQ2=sQuery(id+"F0.wireOp",EDGE,"E0.left");var subQ3=sQuery(id+"F0.wireOp",EDGE,"E0.bottom");Q159=makeQuery(id+"F9.opShell","OFFSET_EDGE",EDGE,{"disambiguationData":[OSD([subQ3,subQ2,subQ1,subQ0]),TDD([makeQuery(id+"F8.opPattern","COPY",EDGE,{"derivedFrom":makeQuery(id+"F7.opPattern","COPY",EDGE,{"derivedFrom":makeQuery(id+"F6.opPattern","COPY",EDGE,{"derivedFrom":makeQuery(id+"F5.opPattern","COPY",EDGE,{"derivedFrom":makeQuery(id+"F4.opLoft","SWEPT_EDGE",EDGE,{"disambiguationData":[OSD([subQ3,subQ2,subQ1,subQ0])]}),"instanceName":"1"}),"instanceName":"1"}),"instanceName":"1"}),"instanceName":"1"})])]});}
            var Q160;
            {var subQ0=sQuery(id+"F3.wireOp",EDGE,"E1.right");var subQ1=sQuery(id+"F3.wireOp",EDGE,"E1.bottom");var subQ2=sQuery(id+"F0.wireOp",EDGE,"E0.left");var subQ3=sQuery(id+"F0.wireOp",EDGE,"E0.bottom");Q160=makeQuery(id+"F9.opShell","OFFSET_EDGE",EDGE,{"disambiguationData":[OSD([subQ3,subQ2,subQ1,subQ0]),TDD([makeQuery(id+"F8.opPattern","COPY",EDGE,{"derivedFrom":makeQuery(id+"F7.opPattern","COPY",EDGE,{"derivedFrom":makeQuery(id+"F4.opLoft","SWEPT_EDGE",EDGE,{"disambiguationData":[OSD([subQ3,subQ2,subQ1,subQ0])]}),"instanceName":"1"}),"instanceName":"1"})])]});}
            var Q161;
            Q161=makeQuery(id+"F8.opPattern","COPY",EDGE,{"derivedFrom":makeQuery(id+"F6.opPattern","COPY",EDGE,{"derivedFrom":makeQuery(id+"F4.opLoft","MID_CAP_EDGE",EDGE,{"disambiguationData":[OSD([sQuery(id+"F0.wireOp",EDGE,"E0.top"),sQuery(id+"F0.wireOp",EDGE,"E0.left"),sQuery(id+"F0.wireOp",EDGE,"E0.right")])],"capPos":0.0}),"instanceName":"1"}),"instanceName":"1"});
            var Q162;
            Q162=makeQuery(id+"F8.opPattern","COPY",EDGE,{"derivedFrom":makeQuery(id+"F7.opPattern","COPY",EDGE,{"derivedFrom":makeQuery(id+"F6.opPattern","COPY",EDGE,{"derivedFrom":makeQuery(id+"F4.opLoft","SWEPT_EDGE",EDGE,{"disambiguationData":[OSD([sQuery(id+"F0.wireOp",EDGE,"E0.top"),sQuery(id+"F0.wireOp",EDGE,"E0.right"),sQuery(id+"F3.wireOp",EDGE,"E1.top"),sQuery(id+"F3.wireOp",EDGE,"E1.left")])]}),"instanceName":"1"}),"instanceName":"1"}),"instanceName":"1"});
            var Q163;
            Q163=makeQuery(id+"F8.opPattern","COPY",EDGE,{"derivedFrom":makeQuery(id+"F6.opPattern","COPY",EDGE,{"derivedFrom":makeQuery(id+"F5.opPattern","COPY",EDGE,{"derivedFrom":makeQuery(id+"F4.opLoft","SWEPT_EDGE",EDGE,{"disambiguationData":[OSD([sQuery(id+"F0.wireOp",EDGE,"E0.bottom"),sQuery(id+"F0.wireOp",EDGE,"E0.left"),sQuery(id+"F3.wireOp",EDGE,"E1.bottom"),sQuery(id+"F3.wireOp",EDGE,"E1.right")])]}),"instanceName":"1"}),"instanceName":"1"}),"instanceName":"1"});
            var Q164;
            {var subQ0=sQuery(id+"F3.wireOp",EDGE,"E1.right");var subQ1=sQuery(id+"F3.wireOp",EDGE,"E1.bottom");var subQ2=sQuery(id+"F0.wireOp",EDGE,"E0.left");var subQ3=sQuery(id+"F0.wireOp",EDGE,"E0.bottom");Q164=makeQuery(id+"F9.opShell","OFFSET_EDGE",EDGE,{"disambiguationData":[OSD([subQ3,subQ2,subQ1,subQ0]),TDD([makeQuery(id+"F8.opPattern","COPY",EDGE,{"derivedFrom":makeQuery(id+"F5.opPattern","COPY",EDGE,{"derivedFrom":makeQuery(id+"F4.opLoft","SWEPT_EDGE",EDGE,{"disambiguationData":[OSD([subQ3,subQ2,subQ1,subQ0])]}),"instanceName":"1"}),"instanceName":"1"})])]});}
            var Q165;
            Q165=makeQuery(id+"F8.opPattern","COPY",EDGE,{"derivedFrom":makeQuery(id+"F7.opPattern","COPY",EDGE,{"derivedFrom":makeQuery(id+"F6.opPattern","COPY",EDGE,{"derivedFrom":makeQuery(id+"F4.opLoft","SWEPT_EDGE",EDGE,{"disambiguationData":[OSD([sQuery(id+"F0.wireOp",EDGE,"E0.bottom"),sQuery(id+"F0.wireOp",EDGE,"E0.left"),sQuery(id+"F3.wireOp",EDGE,"E1.bottom"),sQuery(id+"F3.wireOp",EDGE,"E1.right")])]}),"instanceName":"1"}),"instanceName":"1"}),"instanceName":"1"});
            var Q166;
            Q166=makeQuery(id+"F7.opPattern","COPY",EDGE,{"derivedFrom":makeQuery(id+"F6.opPattern","COPY",EDGE,{"derivedFrom":makeQuery(id+"F5.opPattern","COPY",EDGE,{"derivedFrom":makeQuery(id+"F4.opLoft","SWEPT_EDGE",EDGE,{"disambiguationData":[OSD([sQuery(id+"F0.wireOp",EDGE,"E0.bottom"),sQuery(id+"F0.wireOp",EDGE,"E0.right"),sQuery(id+"F3.wireOp",EDGE,"E1.bottom"),sQuery(id+"F3.wireOp",EDGE,"E1.left")])]}),"instanceName":"1"}),"instanceName":"1"}),"instanceName":"1"});
            var Q167;
            {var subQ0=sQuery(id+"F0.wireOp",EDGE,"E0.right");var subQ1=sQuery(id+"F0.wireOp",EDGE,"E0.left");var subQ2=sQuery(id+"F0.wireOp",EDGE,"E0.bottom");var subQ3=makeQuery(id+"F7.opPattern","COPY",EDGE,{"derivedFrom":makeQuery(id+"F6.opPattern","COPY",EDGE,{"derivedFrom":makeQuery(id+"F4.opLoft","MID_CAP_EDGE",EDGE,{"disambiguationData":[OSD([subQ2,subQ1,subQ0])],"capPos":0.0}),"instanceName":"1"}),"instanceName":"1"});Q167=makeQuery(id+"F9.opShell","OFFSET_EDGE",EDGE,{"disambiguationData":[OSD([subQ2,subQ1,subQ0]),TDD([makeQuery(id+"F8.boolean.opBoolean","MERGE",EDGE,{"derivedFrom":[subQ3,makeQuery(id+"F8.opPattern","COPY",EDGE,{"derivedFrom":subQ3,"instanceName":"1"})]})])]});}
            var Q168;
            {var subQ0=sQuery(id+"F3.wireOp",EDGE,"E1.right");var subQ1=sQuery(id+"F3.wireOp",EDGE,"E1.bottom");var subQ2=sQuery(id+"F0.wireOp",EDGE,"E0.left");var subQ3=sQuery(id+"F0.wireOp",EDGE,"E0.bottom");Q168=makeQuery(id+"F9.opShell","OFFSET_EDGE",EDGE,{"disambiguationData":[OSD([subQ3,subQ2,subQ1,subQ0]),TDD([makeQuery(id+"F8.opPattern","COPY",EDGE,{"derivedFrom":makeQuery(id+"F6.opPattern","COPY",EDGE,{"derivedFrom":makeQuery(id+"F4.opLoft","SWEPT_EDGE",EDGE,{"disambiguationData":[OSD([subQ3,subQ2,subQ1,subQ0])]}),"instanceName":"1"}),"instanceName":"1"})])]});}
            var Q169;
            {var subQ0=sQuery(id+"F0.wireOp",EDGE,"E0.left");var subQ1=sQuery(id+"F0.wireOp",EDGE,"E0.top");var subQ2=sQuery(id+"F0.wireOp",EDGE,"E0.bottom");Q169=makeQuery(id+"F9.opShell","OFFSET_EDGE",EDGE,{"disambiguationData":[OSD([subQ2,subQ1,subQ0]),TDD([makeQuery(id+"F8.opPattern","COPY",EDGE,{"derivedFrom":makeQuery(id+"F6.opPattern","COPY",EDGE,{"derivedFrom":makeQuery(id+"F4.opLoft","MID_CAP_EDGE",EDGE,{"disambiguationData":[OSD([subQ2,subQ1,subQ0])],"capPos":0.0}),"instanceName":"1"}),"instanceName":"1"})])]});}
            var Q170;
            {var subQ0=sQuery(id+"F0.wireOp",EDGE,"E0.right");var subQ1=sQuery(id+"F0.wireOp",EDGE,"E0.left");var subQ2=sQuery(id+"F0.wireOp",EDGE,"E0.bottom");var subQ3=makeQuery(id+"F5.opPattern","COPY",EDGE,{"derivedFrom":makeQuery(id+"F4.opLoft","MID_CAP_EDGE",EDGE,{"disambiguationData":[OSD([subQ2,subQ1,subQ0])],"capPos":0.0}),"instanceName":"1"});Q170=makeQuery(id+"F9.opShell","OFFSET_EDGE",EDGE,{"disambiguationData":[OSD([subQ2,subQ1,subQ0]),TDD([makeQuery(id+"F6.boolean.opBoolean","MERGE",EDGE,{"derivedFrom":[subQ3,makeQuery(id+"F6.opPattern","COPY",EDGE,{"derivedFrom":subQ3,"instanceName":"1"})]})])]});}
            var Q171;
            {var subQ0=sQuery(id+"F3.wireOp",EDGE,"E1.left");var subQ1=sQuery(id+"F3.wireOp",EDGE,"E1.top");var subQ2=sQuery(id+"F0.wireOp",EDGE,"E0.right");var subQ3=sQuery(id+"F0.wireOp",EDGE,"E0.top");Q171=makeQuery(id+"F9.opShell","OFFSET_EDGE",EDGE,{"disambiguationData":[OSD([subQ3,subQ2,subQ1,subQ0]),TDD([makeQuery(id+"F6.opPattern","COPY",EDGE,{"derivedFrom":makeQuery(id+"F5.opPattern","COPY",EDGE,{"derivedFrom":makeQuery(id+"F4.opLoft","SWEPT_EDGE",EDGE,{"disambiguationData":[OSD([subQ3,subQ2,subQ1,subQ0])]}),"instanceName":"1"}),"instanceName":"1"})])]});}
            var Q172;
            {var subQ0=sQuery(id+"F3.wireOp",EDGE,"E1.left");var subQ1=sQuery(id+"F3.wireOp",EDGE,"E1.bottom");var subQ2=sQuery(id+"F0.wireOp",EDGE,"E0.right");var subQ3=sQuery(id+"F0.wireOp",EDGE,"E0.bottom");Q172=makeQuery(id+"F9.opShell","OFFSET_EDGE",EDGE,{"disambiguationData":[OSD([subQ3,subQ2,subQ1,subQ0]),TDD([makeQuery(id+"F6.opPattern","COPY",EDGE,{"derivedFrom":makeQuery(id+"F5.opPattern","COPY",EDGE,{"derivedFrom":makeQuery(id+"F4.opLoft","SWEPT_EDGE",EDGE,{"disambiguationData":[OSD([subQ3,subQ2,subQ1,subQ0])]}),"instanceName":"1"}),"instanceName":"1"})])]});}
            var Q173;
            {var subQ0=sQuery(id+"F3.wireOp",EDGE,"E1.left");var subQ1=sQuery(id+"F3.wireOp",EDGE,"E1.top");var subQ2=sQuery(id+"F0.wireOp",EDGE,"E0.right");var subQ3=sQuery(id+"F0.wireOp",EDGE,"E0.top");Q173=makeQuery(id+"F9.opShell","OFFSET_EDGE",EDGE,{"disambiguationData":[OSD([subQ3,subQ2,subQ1,subQ0]),TDD([makeQuery(id+"F6.opPattern","COPY",EDGE,{"derivedFrom":makeQuery(id+"F4.opLoft","SWEPT_EDGE",EDGE,{"disambiguationData":[OSD([subQ3,subQ2,subQ1,subQ0])]}),"instanceName":"1"})])]});}
            var Q174;
            {var subQ0=sQuery(id+"F3.wireOp",EDGE,"E1.left");var subQ1=sQuery(id+"F3.wireOp",EDGE,"E1.top");var subQ2=sQuery(id+"F0.wireOp",EDGE,"E0.right");var subQ3=sQuery(id+"F0.wireOp",EDGE,"E0.top");Q174=makeQuery(id+"F9.opShell","OFFSET_EDGE",EDGE,{"disambiguationData":[OSD([subQ3,subQ2,subQ1,subQ0]),TDD([makeQuery(id+"F7.opPattern","COPY",EDGE,{"derivedFrom":makeQuery(id+"F4.opLoft","SWEPT_EDGE",EDGE,{"disambiguationData":[OSD([subQ3,subQ2,subQ1,subQ0])]}),"instanceName":"1"})])]});}
            var Q175;
            {var subQ0=sQuery(id+"F3.wireOp",EDGE,"E1.left");var subQ1=sQuery(id+"F3.wireOp",EDGE,"E1.top");var subQ2=sQuery(id+"F0.wireOp",EDGE,"E0.right");var subQ3=sQuery(id+"F0.wireOp",EDGE,"E0.top");Q175=makeQuery(id+"F9.opShell","OFFSET_EDGE",EDGE,{"disambiguationData":[OSD([subQ3,subQ2,subQ1,subQ0]),TDD([makeQuery(id+"F5.opPattern","COPY",EDGE,{"derivedFrom":makeQuery(id+"F4.opLoft","SWEPT_EDGE",EDGE,{"disambiguationData":[OSD([subQ3,subQ2,subQ1,subQ0])]}),"instanceName":"1"})])]});}
            var Q176;
            {var subQ0=sQuery(id+"F0.wireOp",EDGE,"E0.right");var subQ1=sQuery(id+"F0.wireOp",EDGE,"E0.left");var subQ2=sQuery(id+"F0.wireOp",EDGE,"E0.bottom");var subQ3=makeQuery(id+"F5.opPattern","COPY",EDGE,{"derivedFrom":makeQuery(id+"F4.opLoft","MID_CAP_EDGE",EDGE,{"disambiguationData":[OSD([subQ2,subQ1,subQ0])],"capPos":0.0}),"instanceName":"1"});Q176=makeQuery(id+"F9.opShell","OFFSET_EDGE",EDGE,{"disambiguationData":[OSD([subQ2,subQ1,subQ0]),TDD([makeQuery(id+"F7.opPattern","COPY",EDGE,{"derivedFrom":makeQuery(id+"F6.boolean.opBoolean","MERGE",EDGE,{"derivedFrom":[subQ3,makeQuery(id+"F6.opPattern","COPY",EDGE,{"derivedFrom":subQ3,"instanceName":"1"})]}),"instanceName":"1"})])]});}
            var Q177;
            {var subQ0=sQuery(id+"F0.wireOp",EDGE,"E0.right");var subQ1=sQuery(id+"F0.wireOp",EDGE,"E0.top");var subQ2=sQuery(id+"F0.wireOp",EDGE,"E0.bottom");var subQ3=makeQuery(id+"F4.opLoft","MID_CAP_EDGE",EDGE,{"disambiguationData":[OSD([subQ2,subQ1,subQ0])],"capPos":0.0});Q177=makeQuery(id+"F9.opShell","OFFSET_EDGE",EDGE,{"disambiguationData":[OSD([subQ2,subQ1,subQ0]),TDD([makeQuery(id+"F7.boolean.opBoolean","MERGE",EDGE,{"derivedFrom":[subQ3,makeQuery(id+"F7.opPattern","COPY",EDGE,{"derivedFrom":subQ3,"instanceName":"1"})]})])]});}
            var Q178;
            Q178=makeQuery(id+"F7.opPattern","COPY",EDGE,{"derivedFrom":makeQuery(id+"F5.opPattern","COPY",EDGE,{"derivedFrom":makeQuery(id+"F4.opLoft","SWEPT_EDGE",EDGE,{"disambiguationData":[OSD([sQuery(id+"F0.wireOp",EDGE,"E0.bottom"),sQuery(id+"F0.wireOp",EDGE,"E0.right"),sQuery(id+"F3.wireOp",EDGE,"E1.bottom"),sQuery(id+"F3.wireOp",EDGE,"E1.left")])]}),"instanceName":"1"}),"instanceName":"1"});
            var Q179;
            {var subQ0=sQuery(id+"F0.wireOp",EDGE,"E0.right");var subQ1=sQuery(id+"F0.wireOp",EDGE,"E0.left");var subQ2=sQuery(id+"F0.wireOp",EDGE,"E0.bottom");Q179=makeQuery(id+"F9.opShell","OFFSET_EDGE",EDGE,{"disambiguationData":[OSD([subQ2,subQ1,subQ0]),TDD([makeQuery(id+"F8.opPattern","COPY",EDGE,{"derivedFrom":makeQuery(id+"F6.opPattern","COPY",EDGE,{"derivedFrom":makeQuery(id+"F4.opLoft","MID_CAP_EDGE",EDGE,{"disambiguationData":[OSD([subQ2,subQ1,subQ0])],"capPos":0.0}),"instanceName":"1"}),"instanceName":"1"})])]});}
            var Q180;
            {var subQ0=sQuery(id+"F0.wireOp",EDGE,"E0.right");var subQ1=sQuery(id+"F0.wireOp",EDGE,"E0.left");var subQ2=sQuery(id+"F0.wireOp",EDGE,"E0.bottom");var subQ3=makeQuery(id+"F5.opPattern","COPY",EDGE,{"derivedFrom":makeQuery(id+"F4.opLoft","MID_CAP_EDGE",EDGE,{"disambiguationData":[OSD([subQ2,subQ1,subQ0])],"capPos":0.0}),"instanceName":"1"});Q180=makeQuery(id+"F9.opShell","OFFSET_EDGE",EDGE,{"disambiguationData":[OSD([subQ2,subQ1,subQ0]),TDD([makeQuery(id+"F8.opPattern","COPY",EDGE,{"derivedFrom":makeQuery(id+"F6.boolean.opBoolean","MERGE",EDGE,{"derivedFrom":[subQ3,makeQuery(id+"F6.opPattern","COPY",EDGE,{"derivedFrom":subQ3,"instanceName":"1"})]}),"instanceName":"1"})])]});}
            var Q181;
            {var subQ0=sQuery(id+"F0.wireOp",EDGE,"E0.right");var subQ1=sQuery(id+"F0.wireOp",EDGE,"E0.left");var subQ2=sQuery(id+"F0.wireOp",EDGE,"E0.bottom");Q181=makeQuery(id+"F9.opShell","OFFSET_EDGE",EDGE,{"disambiguationData":[OSD([subQ2,subQ1,subQ0]),TDD([makeQuery(id+"F6.opPattern","COPY",EDGE,{"derivedFrom":makeQuery(id+"F4.opLoft","MID_CAP_EDGE",EDGE,{"disambiguationData":[OSD([subQ2,subQ1,subQ0])],"capPos":0.0}),"instanceName":"1"})])]});}
            var Q182;
            {var subQ0=sQuery(id+"F0.wireOp",EDGE,"E0.right");var subQ1=sQuery(id+"F0.wireOp",EDGE,"E0.top");var subQ2=sQuery(id+"F0.wireOp",EDGE,"E0.bottom");var subQ3=makeQuery(id+"F5.opPattern","COPY",EDGE,{"derivedFrom":makeQuery(id+"F4.opLoft","MID_CAP_EDGE",EDGE,{"disambiguationData":[OSD([subQ2,subQ1,subQ0])],"capPos":0.0}),"instanceName":"1"});Q182=makeQuery(id+"F9.opShell","OFFSET_EDGE",EDGE,{"disambiguationData":[OSD([subQ2,subQ1,subQ0]),TDD([makeQuery(id+"F6.boolean.opBoolean","MERGE",EDGE,{"derivedFrom":[subQ3,makeQuery(id+"F6.opPattern","COPY",EDGE,{"derivedFrom":subQ3,"instanceName":"1"})]})])]});}
            var Q183;
            {var subQ0=sQuery(id+"F3.wireOp",EDGE,"E1.right");var subQ1=sQuery(id+"F3.wireOp",EDGE,"E1.left");var subQ2=sQuery(id+"F3.wireOp",EDGE,"E1.bottom");var subQ3=makeQuery(id+"F4.opLoft","MID_CAP_EDGE",EDGE,{"disambiguationData":[OSD([subQ2,subQ1,subQ0])],"capPos":1.0});Q183=makeQuery(id+"F9.opShell","OFFSET_EDGE",EDGE,{"disambiguationData":[OSD([subQ2,subQ1,subQ0]),TDD([makeQuery(id+"F6.opPattern","COPY",EDGE,{"derivedFrom":makeQuery(id+"F5.boolean.opBoolean","MERGE",EDGE,{"derivedFrom":[subQ3,makeQuery(id+"F5.opPattern","COPY",EDGE,{"derivedFrom":subQ3,"instanceName":"1"})]}),"instanceName":"1"})])]});}
            var Q184;
            {var subQ0=sQuery(id+"F3.wireOp",EDGE,"E1.left");var subQ1=sQuery(id+"F3.wireOp",EDGE,"E1.bottom");var subQ2=sQuery(id+"F0.wireOp",EDGE,"E0.right");var subQ3=sQuery(id+"F0.wireOp",EDGE,"E0.bottom");Q184=makeQuery(id+"F9.opShell","OFFSET_EDGE",EDGE,{"disambiguationData":[OSD([subQ3,subQ2,subQ1,subQ0]),TDD([makeQuery(id+"F7.opPattern","COPY",EDGE,{"derivedFrom":makeQuery(id+"F4.opLoft","SWEPT_EDGE",EDGE,{"disambiguationData":[OSD([subQ3,subQ2,subQ1,subQ0])]}),"instanceName":"1"})])]});}
            var Q185;
            {var subQ0=sQuery(id+"F0.wireOp",EDGE,"E0.right");var subQ1=sQuery(id+"F0.wireOp",EDGE,"E0.top");var subQ2=sQuery(id+"F0.wireOp",EDGE,"E0.bottom");var subQ3=makeQuery(id+"F5.opPattern","COPY",EDGE,{"derivedFrom":makeQuery(id+"F4.opLoft","MID_CAP_EDGE",EDGE,{"disambiguationData":[OSD([subQ2,subQ1,subQ0])],"capPos":0.0}),"instanceName":"1"});Q185=makeQuery(id+"F9.opShell","OFFSET_EDGE",EDGE,{"disambiguationData":[OSD([subQ2,subQ1,subQ0]),TDD([makeQuery(id+"F7.opPattern","COPY",EDGE,{"derivedFrom":makeQuery(id+"F6.boolean.opBoolean","MERGE",EDGE,{"derivedFrom":[subQ3,makeQuery(id+"F6.opPattern","COPY",EDGE,{"derivedFrom":subQ3,"instanceName":"1"})]}),"instanceName":"1"})])]});}
            var Q186;
            {var subQ0=sQuery(id+"F0.wireOp",EDGE,"E0.right");var subQ1=sQuery(id+"F0.wireOp",EDGE,"E0.top");var subQ2=sQuery(id+"F0.wireOp",EDGE,"E0.bottom");Q186=makeQuery(id+"F9.opShell","OFFSET_EDGE",EDGE,{"disambiguationData":[OSD([subQ2,subQ1,subQ0]),TDD([makeQuery(id+"F6.opPattern","COPY",EDGE,{"derivedFrom":makeQuery(id+"F4.opLoft","MID_CAP_EDGE",EDGE,{"disambiguationData":[OSD([subQ2,subQ1,subQ0])],"capPos":0.0}),"instanceName":"1"})])]});}
            var Q187;
            {var subQ0=makeQuery(id+"F5.opPattern","COPY",EDGE,{"derivedFrom":makeQuery(id+"F4.opLoft","MID_CAP_EDGE",EDGE,{"disambiguationData":[OSD([sQuery(id+"F0.wireOp",EDGE,"E0.top"),sQuery(id+"F0.wireOp",EDGE,"E0.left"),sQuery(id+"F0.wireOp",EDGE,"E0.right")])],"capPos":0.0}),"instanceName":"1"});Q187=makeQuery(id+"F8.opPattern","COPY",EDGE,{"derivedFrom":makeQuery(id+"F6.boolean.opBoolean","MERGE",EDGE,{"derivedFrom":[subQ0,makeQuery(id+"F6.opPattern","COPY",EDGE,{"derivedFrom":subQ0,"instanceName":"1"})]}),"instanceName":"1"});}
            var Q188;
            {var subQ0=sQuery(id+"F3.wireOp",EDGE,"E1.right");var subQ1=sQuery(id+"F3.wireOp",EDGE,"E1.bottom");var subQ2=sQuery(id+"F0.wireOp",EDGE,"E0.left");var subQ3=sQuery(id+"F0.wireOp",EDGE,"E0.bottom");Q188=makeQuery(id+"F9.opShell","OFFSET_EDGE",EDGE,{"disambiguationData":[OSD([subQ3,subQ2,subQ1,subQ0]),TDD([makeQuery(id+"F7.opPattern","COPY",EDGE,{"derivedFrom":makeQuery(id+"F5.opPattern","COPY",EDGE,{"derivedFrom":makeQuery(id+"F4.opLoft","SWEPT_EDGE",EDGE,{"disambiguationData":[OSD([subQ3,subQ2,subQ1,subQ0])]}),"instanceName":"1"}),"instanceName":"1"})])]});}
            var Q189;
            {var subQ0=makeQuery(id+"F4.opLoft","MID_CAP_EDGE",EDGE,{"disambiguationData":[OSD([sQuery(id+"F0.wireOp",EDGE,"E0.top"),sQuery(id+"F0.wireOp",EDGE,"E0.left"),sQuery(id+"F0.wireOp",EDGE,"E0.right")])],"capPos":0.0});Q189=makeQuery(id+"F7.boolean.opBoolean","MERGE",EDGE,{"derivedFrom":[subQ0,makeQuery(id+"F7.opPattern","COPY",EDGE,{"derivedFrom":subQ0,"instanceName":"1"})]});}
            var Q190;
            Q190=makeQuery(id+"F7.opPattern","COPY",EDGE,{"derivedFrom":makeQuery(id+"F6.opPattern","COPY",EDGE,{"derivedFrom":makeQuery(id+"F5.opPattern","COPY",EDGE,{"derivedFrom":makeQuery(id+"F4.opLoft","SWEPT_EDGE",EDGE,{"disambiguationData":[OSD([sQuery(id+"F0.wireOp",EDGE,"E0.bottom"),sQuery(id+"F0.wireOp",EDGE,"E0.left"),sQuery(id+"F3.wireOp",EDGE,"E1.bottom"),sQuery(id+"F3.wireOp",EDGE,"E1.right")])]}),"instanceName":"1"}),"instanceName":"1"}),"instanceName":"1"});
            var Q191;
            {var subQ0=sQuery(id+"F3.wireOp",EDGE,"E1.right");var subQ1=sQuery(id+"F3.wireOp",EDGE,"E1.bottom");var subQ2=sQuery(id+"F0.wireOp",EDGE,"E0.left");var subQ3=sQuery(id+"F0.wireOp",EDGE,"E0.bottom");Q191=makeQuery(id+"F9.opShell","OFFSET_EDGE",EDGE,{"disambiguationData":[OSD([subQ3,subQ2,subQ1,subQ0]),TDD([makeQuery(id+"F8.opPattern","COPY",EDGE,{"derivedFrom":makeQuery(id+"F7.opPattern","COPY",EDGE,{"derivedFrom":makeQuery(id+"F6.opPattern","COPY",EDGE,{"derivedFrom":makeQuery(id+"F4.opLoft","SWEPT_EDGE",EDGE,{"disambiguationData":[OSD([subQ3,subQ2,subQ1,subQ0])]}),"instanceName":"1"}),"instanceName":"1"}),"instanceName":"1"})])]});}
            var Q192;
            {var subQ0=sQuery(id+"F3.wireOp",EDGE,"E1.left");var subQ1=sQuery(id+"F3.wireOp",EDGE,"E1.bottom");var subQ2=sQuery(id+"F0.wireOp",EDGE,"E0.right");var subQ3=sQuery(id+"F0.wireOp",EDGE,"E0.bottom");Q192=makeQuery(id+"F9.opShell","OFFSET_EDGE",EDGE,{"disambiguationData":[OSD([subQ3,subQ2,subQ1,subQ0]),TDD([makeQuery(id+"F6.opPattern","COPY",EDGE,{"derivedFrom":makeQuery(id+"F4.opLoft","SWEPT_EDGE",EDGE,{"disambiguationData":[OSD([subQ3,subQ2,subQ1,subQ0])]}),"instanceName":"1"})])]});}
            var Q193;
            {var subQ0=sQuery(id+"F3.wireOp",EDGE,"E1.left");var subQ1=sQuery(id+"F3.wireOp",EDGE,"E1.bottom");var subQ2=sQuery(id+"F0.wireOp",EDGE,"E0.right");var subQ3=sQuery(id+"F0.wireOp",EDGE,"E0.bottom");Q193=makeQuery(id+"F9.opShell","OFFSET_EDGE",EDGE,{"disambiguationData":[OSD([subQ3,subQ2,subQ1,subQ0]),TDD([makeQuery(id+"F5.opPattern","COPY",EDGE,{"derivedFrom":makeQuery(id+"F4.opLoft","SWEPT_EDGE",EDGE,{"disambiguationData":[OSD([subQ3,subQ2,subQ1,subQ0])]}),"instanceName":"1"})])]});}
            var Q194;
            {var subQ0=sQuery(id+"F3.wireOp",EDGE,"E1.left");var subQ1=sQuery(id+"F3.wireOp",EDGE,"E1.top");var subQ2=sQuery(id+"F0.wireOp",EDGE,"E0.right");var subQ3=sQuery(id+"F0.wireOp",EDGE,"E0.top");Q194=makeQuery(id+"F9.opShell","OFFSET_EDGE",EDGE,{"disambiguationData":[OSD([subQ3,subQ2,subQ1,subQ0]),TDD([makeQuery(id+"F7.opPattern","COPY",EDGE,{"derivedFrom":makeQuery(id+"F6.opPattern","COPY",EDGE,{"derivedFrom":makeQuery(id+"F5.opPattern","COPY",EDGE,{"derivedFrom":makeQuery(id+"F4.opLoft","SWEPT_EDGE",EDGE,{"disambiguationData":[OSD([subQ3,subQ2,subQ1,subQ0])]}),"instanceName":"1"}),"instanceName":"1"}),"instanceName":"1"})])]});}
            var Q195;
            {var subQ0=makeQuery(id+"F7.opPattern","COPY",EDGE,{"derivedFrom":makeQuery(id+"F6.opPattern","COPY",EDGE,{"derivedFrom":makeQuery(id+"F4.opLoft","MID_CAP_EDGE",EDGE,{"disambiguationData":[OSD([sQuery(id+"F0.wireOp",EDGE,"E0.top"),sQuery(id+"F0.wireOp",EDGE,"E0.left"),sQuery(id+"F0.wireOp",EDGE,"E0.right")])],"capPos":0.0}),"instanceName":"1"}),"instanceName":"1"});Q195=makeQuery(id+"F8.boolean.opBoolean","MERGE",EDGE,{"derivedFrom":[subQ0,makeQuery(id+"F8.opPattern","COPY",EDGE,{"derivedFrom":subQ0,"instanceName":"1"})]});}
            var Q196;
            {var subQ0=makeQuery(id+"F4.opLoft","MID_CAP_EDGE",EDGE,{"disambiguationData":[OSD([sQuery(id+"F3.wireOp",EDGE,"E1.bottom"),sQuery(id+"F3.wireOp",EDGE,"E1.top"),sQuery(id+"F3.wireOp",EDGE,"E1.left")])],"capPos":1.0});Q196=makeQuery(id+"F5.boolean.opBoolean","MERGE",EDGE,{"derivedFrom":[subQ0,makeQuery(id+"F5.opPattern","COPY",EDGE,{"derivedFrom":subQ0,"instanceName":"1"})]});}
            var Q197;
            {var subQ0=makeQuery(id+"F4.opLoft","MID_CAP_EDGE",EDGE,{"disambiguationData":[OSD([sQuery(id+"F3.wireOp",EDGE,"E1.top"),sQuery(id+"F3.wireOp",EDGE,"E1.left"),sQuery(id+"F3.wireOp",EDGE,"E1.right")])],"capPos":1.0});Q197=makeQuery(id+"F6.opPattern","COPY",EDGE,{"derivedFrom":makeQuery(id+"F5.boolean.opBoolean","MERGE",EDGE,{"derivedFrom":[subQ0,makeQuery(id+"F5.opPattern","COPY",EDGE,{"derivedFrom":subQ0,"instanceName":"1"})]}),"instanceName":"1"});}
            var Q198;
            Q198=makeQuery(id+"F8.opPattern","COPY",EDGE,{"derivedFrom":makeQuery(id+"F5.opPattern","COPY",EDGE,{"derivedFrom":makeQuery(id+"F4.opLoft","SWEPT_EDGE",EDGE,{"disambiguationData":[OSD([sQuery(id+"F0.wireOp",EDGE,"E0.top"),sQuery(id+"F0.wireOp",EDGE,"E0.left"),sQuery(id+"F3.wireOp",EDGE,"E1.top"),sQuery(id+"F3.wireOp",EDGE,"E1.right")])]}),"instanceName":"1"}),"instanceName":"1"});
            var Q199;
            {var subQ0=sQuery(id+"F3.wireOp",EDGE,"E1.right");var subQ1=sQuery(id+"F3.wireOp",EDGE,"E1.left");var subQ2=sQuery(id+"F3.wireOp",EDGE,"E1.top");var subQ3=makeQuery(id+"F4.opLoft","MID_CAP_EDGE",EDGE,{"disambiguationData":[OSD([subQ2,subQ1,subQ0])],"capPos":1.0});Q199=makeQuery(id+"F9.opShell","OFFSET_EDGE",EDGE,{"disambiguationData":[OSD([subQ2,subQ1,subQ0]),TDD([makeQuery(id+"F8.opPattern","COPY",EDGE,{"derivedFrom":makeQuery(id+"F6.opPattern","COPY",EDGE,{"derivedFrom":makeQuery(id+"F5.boolean.opBoolean","MERGE",EDGE,{"derivedFrom":[subQ3,makeQuery(id+"F5.opPattern","COPY",EDGE,{"derivedFrom":subQ3,"instanceName":"1"})]}),"instanceName":"1"}),"instanceName":"1"})])]});}
            var Q200;
            {var subQ0=sQuery(id+"F3.wireOp",EDGE,"E1.right");var subQ1=sQuery(id+"F3.wireOp",EDGE,"E1.top");var subQ2=sQuery(id+"F3.wireOp",EDGE,"E1.bottom");var subQ3=makeQuery(id+"F4.opLoft","MID_CAP_EDGE",EDGE,{"disambiguationData":[OSD([subQ2,subQ1,subQ0])],"capPos":1.0});Q200=makeQuery(id+"F9.opShell","OFFSET_EDGE",EDGE,{"disambiguationData":[OSD([subQ2,subQ1,subQ0]),TDD([makeQuery(id+"F8.opPattern","COPY",EDGE,{"derivedFrom":makeQuery(id+"F6.opPattern","COPY",EDGE,{"derivedFrom":makeQuery(id+"F5.boolean.opBoolean","MERGE",EDGE,{"derivedFrom":[subQ3,makeQuery(id+"F5.opPattern","COPY",EDGE,{"derivedFrom":subQ3,"instanceName":"1"})]}),"instanceName":"1"}),"instanceName":"1"})])]});}
            var Q201;
            {var subQ0=sQuery(id+"F0.wireOp",EDGE,"E0.left");var subQ1=sQuery(id+"F0.wireOp",EDGE,"E0.top");var subQ2=sQuery(id+"F0.wireOp",EDGE,"E0.bottom");var subQ3=makeQuery(id+"F5.opPattern","COPY",EDGE,{"derivedFrom":makeQuery(id+"F4.opLoft","MID_CAP_EDGE",EDGE,{"disambiguationData":[OSD([subQ2,subQ1,subQ0])],"capPos":0.0}),"instanceName":"1"});Q201=makeQuery(id+"F9.opShell","OFFSET_EDGE",EDGE,{"disambiguationData":[OSD([subQ2,subQ1,subQ0]),TDD([makeQuery(id+"F8.opPattern","COPY",EDGE,{"derivedFrom":makeQuery(id+"F7.opPattern","COPY",EDGE,{"derivedFrom":makeQuery(id+"F6.boolean.opBoolean","MERGE",EDGE,{"derivedFrom":[subQ3,makeQuery(id+"F6.opPattern","COPY",EDGE,{"derivedFrom":subQ3,"instanceName":"1"})]}),"instanceName":"1"}),"instanceName":"1"})])]});}
            var Q202;
            {var subQ0=makeQuery(id+"F5.opPattern","COPY",EDGE,{"derivedFrom":makeQuery(id+"F4.opLoft","MID_CAP_EDGE",EDGE,{"disambiguationData":[OSD([sQuery(id+"F0.wireOp",EDGE,"E0.bottom"),sQuery(id+"F0.wireOp",EDGE,"E0.top"),sQuery(id+"F0.wireOp",EDGE,"E0.left")])],"capPos":0.0}),"instanceName":"1"});Q202=makeQuery(id+"F8.opPattern","COPY",EDGE,{"derivedFrom":makeQuery(id+"F6.boolean.opBoolean","MERGE",EDGE,{"derivedFrom":[subQ0,makeQuery(id+"F6.opPattern","COPY",EDGE,{"derivedFrom":subQ0,"instanceName":"1"})]}),"instanceName":"1"});}
            var Q203;
            {var subQ0=sQuery(id+"F3.wireOp",EDGE,"E1.right");var subQ1=sQuery(id+"F3.wireOp",EDGE,"E1.top");var subQ2=sQuery(id+"F0.wireOp",EDGE,"E0.left");var subQ3=sQuery(id+"F0.wireOp",EDGE,"E0.top");Q203=makeQuery(id+"F9.opShell","OFFSET_EDGE",EDGE,{"disambiguationData":[OSD([subQ3,subQ2,subQ1,subQ0]),TDD([makeQuery(id+"F8.opPattern","COPY",EDGE,{"derivedFrom":makeQuery(id+"F7.opPattern","COPY",EDGE,{"derivedFrom":makeQuery(id+"F5.opPattern","COPY",EDGE,{"derivedFrom":makeQuery(id+"F4.opLoft","SWEPT_EDGE",EDGE,{"disambiguationData":[OSD([subQ3,subQ2,subQ1,subQ0])]}),"instanceName":"1"}),"instanceName":"1"}),"instanceName":"1"})])]});}
            var Q204;
            {var subQ0=sQuery(id+"F3.wireOp",EDGE,"E1.right");var subQ1=sQuery(id+"F3.wireOp",EDGE,"E1.left");var subQ2=sQuery(id+"F3.wireOp",EDGE,"E1.top");var subQ3=makeQuery(id+"F4.opLoft","MID_CAP_EDGE",EDGE,{"disambiguationData":[OSD([subQ2,subQ1,subQ0])],"capPos":1.0});Q204=makeQuery(id+"F9.opShell","OFFSET_EDGE",EDGE,{"disambiguationData":[OSD([subQ2,subQ1,subQ0]),TDD([makeQuery(id+"F8.opPattern","COPY",EDGE,{"derivedFrom":makeQuery(id+"F7.opPattern","COPY",EDGE,{"derivedFrom":makeQuery(id+"F5.boolean.opBoolean","MERGE",EDGE,{"derivedFrom":[subQ3,makeQuery(id+"F5.opPattern","COPY",EDGE,{"derivedFrom":subQ3,"instanceName":"1"})]}),"instanceName":"1"}),"instanceName":"1"})])]});}
            var Q205;
            {var subQ0=makeQuery(id+"F4.opLoft","MID_CAP_EDGE",EDGE,{"disambiguationData":[OSD([sQuery(id+"F3.wireOp",EDGE,"E1.bottom"),sQuery(id+"F3.wireOp",EDGE,"E1.top"),sQuery(id+"F3.wireOp",EDGE,"E1.right")])],"capPos":1.0});Q205=makeQuery(id+"F8.opPattern","COPY",EDGE,{"derivedFrom":makeQuery(id+"F6.opPattern","COPY",EDGE,{"derivedFrom":makeQuery(id+"F5.boolean.opBoolean","MERGE",EDGE,{"derivedFrom":[subQ0,makeQuery(id+"F5.opPattern","COPY",EDGE,{"derivedFrom":subQ0,"instanceName":"1"})]}),"instanceName":"1"}),"instanceName":"1"});}
            var Q206;
            {var subQ0=sQuery(id+"F0.wireOp",EDGE,"E0.left");var subQ1=sQuery(id+"F0.wireOp",EDGE,"E0.top");var subQ2=sQuery(id+"F0.wireOp",EDGE,"E0.bottom");var subQ3=makeQuery(id+"F5.opPattern","COPY",EDGE,{"derivedFrom":makeQuery(id+"F4.opLoft","MID_CAP_EDGE",EDGE,{"disambiguationData":[OSD([subQ2,subQ1,subQ0])],"capPos":0.0}),"instanceName":"1"});Q206=makeQuery(id+"F9.opShell","OFFSET_EDGE",EDGE,{"disambiguationData":[OSD([subQ2,subQ1,subQ0]),TDD([makeQuery(id+"F7.opPattern","COPY",EDGE,{"derivedFrom":makeQuery(id+"F6.boolean.opBoolean","MERGE",EDGE,{"derivedFrom":[subQ3,makeQuery(id+"F6.opPattern","COPY",EDGE,{"derivedFrom":subQ3,"instanceName":"1"})]}),"instanceName":"1"})])]});}
            var Q207;
            {var subQ0=sQuery(id+"F3.wireOp",EDGE,"E1.right");var subQ1=sQuery(id+"F3.wireOp",EDGE,"E1.top");var subQ2=sQuery(id+"F0.wireOp",EDGE,"E0.left");var subQ3=sQuery(id+"F0.wireOp",EDGE,"E0.top");Q207=makeQuery(id+"F9.opShell","OFFSET_EDGE",EDGE,{"disambiguationData":[OSD([subQ3,subQ2,subQ1,subQ0]),TDD([makeQuery(id+"F8.opPattern","COPY",EDGE,{"derivedFrom":makeQuery(id+"F5.opPattern","COPY",EDGE,{"derivedFrom":makeQuery(id+"F4.opLoft","SWEPT_EDGE",EDGE,{"disambiguationData":[OSD([subQ3,subQ2,subQ1,subQ0])]}),"instanceName":"1"}),"instanceName":"1"})])]});}
            var Q208;
            {var subQ0=sQuery(id+"F0.wireOp",EDGE,"E0.right");var subQ1=sQuery(id+"F0.wireOp",EDGE,"E0.left");var subQ2=sQuery(id+"F0.wireOp",EDGE,"E0.top");var subQ3=makeQuery(id+"F5.opPattern","COPY",EDGE,{"derivedFrom":makeQuery(id+"F4.opLoft","MID_CAP_EDGE",EDGE,{"disambiguationData":[OSD([subQ2,subQ1,subQ0])],"capPos":0.0}),"instanceName":"1"});Q208=makeQuery(id+"F9.opShell","OFFSET_EDGE",EDGE,{"disambiguationData":[OSD([subQ2,subQ1,subQ0]),TDD([makeQuery(id+"F8.opPattern","COPY",EDGE,{"derivedFrom":makeQuery(id+"F7.opPattern","COPY",EDGE,{"derivedFrom":makeQuery(id+"F6.boolean.opBoolean","MERGE",EDGE,{"derivedFrom":[subQ3,makeQuery(id+"F6.opPattern","COPY",EDGE,{"derivedFrom":subQ3,"instanceName":"1"})]}),"instanceName":"1"}),"instanceName":"1"})])]});}
            var Q209;
            {var subQ0=sQuery(id+"F3.wireOp",EDGE,"E1.right");var subQ1=sQuery(id+"F3.wireOp",EDGE,"E1.top");var subQ2=sQuery(id+"F0.wireOp",EDGE,"E0.left");var subQ3=sQuery(id+"F0.wireOp",EDGE,"E0.top");Q209=makeQuery(id+"F9.opShell","OFFSET_EDGE",EDGE,{"disambiguationData":[OSD([subQ3,subQ2,subQ1,subQ0]),TDD([makeQuery(id+"F8.opPattern","COPY",EDGE,{"derivedFrom":makeQuery(id+"F6.opPattern","COPY",EDGE,{"derivedFrom":makeQuery(id+"F5.opPattern","COPY",EDGE,{"derivedFrom":makeQuery(id+"F4.opLoft","SWEPT_EDGE",EDGE,{"disambiguationData":[OSD([subQ3,subQ2,subQ1,subQ0])]}),"instanceName":"1"}),"instanceName":"1"}),"instanceName":"1"})])]});}
            var Q210;
            {var subQ0=sQuery(id+"F3.wireOp",EDGE,"E1.left");var subQ1=sQuery(id+"F3.wireOp",EDGE,"E1.bottom");var subQ2=sQuery(id+"F0.wireOp",EDGE,"E0.right");var subQ3=sQuery(id+"F0.wireOp",EDGE,"E0.bottom");Q210=makeQuery(id+"F9.opShell","OFFSET_EDGE",EDGE,{"disambiguationData":[OSD([subQ3,subQ2,subQ1,subQ0]),TDD([makeQuery(id+"F8.opPattern","COPY",EDGE,{"derivedFrom":makeQuery(id+"F6.opPattern","COPY",EDGE,{"derivedFrom":makeQuery(id+"F5.opPattern","COPY",EDGE,{"derivedFrom":makeQuery(id+"F4.opLoft","SWEPT_EDGE",EDGE,{"disambiguationData":[OSD([subQ3,subQ2,subQ1,subQ0])]}),"instanceName":"1"}),"instanceName":"1"}),"instanceName":"1"})])]});}
            var Q211;
            {var subQ0=sQuery(id+"F3.wireOp",EDGE,"E1.right");var subQ1=sQuery(id+"F3.wireOp",EDGE,"E1.bottom");var subQ2=sQuery(id+"F0.wireOp",EDGE,"E0.left");var subQ3=sQuery(id+"F0.wireOp",EDGE,"E0.bottom");Q211=makeQuery(id+"F9.opShell","OFFSET_EDGE",EDGE,{"disambiguationData":[OSD([subQ3,subQ2,subQ1,subQ0]),TDD([makeQuery(id+"F8.opPattern","COPY",EDGE,{"derivedFrom":makeQuery(id+"F7.opPattern","COPY",EDGE,{"derivedFrom":makeQuery(id+"F5.opPattern","COPY",EDGE,{"derivedFrom":makeQuery(id+"F4.opLoft","SWEPT_EDGE",EDGE,{"disambiguationData":[OSD([subQ3,subQ2,subQ1,subQ0])]}),"instanceName":"1"}),"instanceName":"1"}),"instanceName":"1"})])]});}
            var Q212;
            {var subQ0=sQuery(id+"F0.wireOp",EDGE,"E0.right");var subQ1=sQuery(id+"F0.wireOp",EDGE,"E0.left");var subQ2=sQuery(id+"F0.wireOp",EDGE,"E0.top");var subQ3=makeQuery(id+"F7.opPattern","COPY",EDGE,{"derivedFrom":makeQuery(id+"F6.opPattern","COPY",EDGE,{"derivedFrom":makeQuery(id+"F4.opLoft","MID_CAP_EDGE",EDGE,{"disambiguationData":[OSD([subQ2,subQ1,subQ0])],"capPos":0.0}),"instanceName":"1"}),"instanceName":"1"});Q212=makeQuery(id+"F9.opShell","OFFSET_EDGE",EDGE,{"disambiguationData":[OSD([subQ2,subQ1,subQ0]),TDD([makeQuery(id+"F8.boolean.opBoolean","MERGE",EDGE,{"derivedFrom":[subQ3,makeQuery(id+"F8.opPattern","COPY",EDGE,{"derivedFrom":subQ3,"instanceName":"1"})]})])]});}
            var Q213;
            {var subQ0=sQuery(id+"F3.wireOp",EDGE,"E1.right");var subQ1=sQuery(id+"F3.wireOp",EDGE,"E1.top");var subQ2=sQuery(id+"F0.wireOp",EDGE,"E0.left");var subQ3=sQuery(id+"F0.wireOp",EDGE,"E0.top");Q213=makeQuery(id+"F9.opShell","OFFSET_EDGE",EDGE,{"disambiguationData":[OSD([subQ3,subQ2,subQ1,subQ0]),TDD([makeQuery(id+"F8.opPattern","COPY",EDGE,{"derivedFrom":makeQuery(id+"F7.opPattern","COPY",EDGE,{"derivedFrom":makeQuery(id+"F6.opPattern","COPY",EDGE,{"derivedFrom":makeQuery(id+"F5.opPattern","COPY",EDGE,{"derivedFrom":makeQuery(id+"F4.opLoft","SWEPT_EDGE",EDGE,{"disambiguationData":[OSD([subQ3,subQ2,subQ1,subQ0])]}),"instanceName":"1"}),"instanceName":"1"}),"instanceName":"1"}),"instanceName":"1"})])]});}
            var Q214;
            {var subQ0=sQuery(id+"F3.wireOp",EDGE,"E1.left");var subQ1=sQuery(id+"F3.wireOp",EDGE,"E1.bottom");var subQ2=sQuery(id+"F0.wireOp",EDGE,"E0.right");var subQ3=sQuery(id+"F0.wireOp",EDGE,"E0.bottom");Q214=makeQuery(id+"F9.opShell","OFFSET_EDGE",EDGE,{"disambiguationData":[OSD([subQ3,subQ2,subQ1,subQ0]),TDD([makeQuery(id+"F8.opPattern","COPY",EDGE,{"derivedFrom":makeQuery(id+"F6.opPattern","COPY",EDGE,{"derivedFrom":makeQuery(id+"F4.opLoft","SWEPT_EDGE",EDGE,{"disambiguationData":[OSD([subQ3,subQ2,subQ1,subQ0])]}),"instanceName":"1"}),"instanceName":"1"})])]});}
            var Q215;
            {var subQ0=sQuery(id+"F0.wireOp",EDGE,"E0.right");var subQ1=sQuery(id+"F0.wireOp",EDGE,"E0.left");var subQ2=sQuery(id+"F0.wireOp",EDGE,"E0.top");var subQ3=makeQuery(id+"F5.opPattern","COPY",EDGE,{"derivedFrom":makeQuery(id+"F4.opLoft","MID_CAP_EDGE",EDGE,{"disambiguationData":[OSD([subQ2,subQ1,subQ0])],"capPos":0.0}),"instanceName":"1"});Q215=makeQuery(id+"F9.opShell","OFFSET_EDGE",EDGE,{"disambiguationData":[OSD([subQ2,subQ1,subQ0]),TDD([makeQuery(id+"F8.opPattern","COPY",EDGE,{"derivedFrom":makeQuery(id+"F6.boolean.opBoolean","MERGE",EDGE,{"derivedFrom":[subQ3,makeQuery(id+"F6.opPattern","COPY",EDGE,{"derivedFrom":subQ3,"instanceName":"1"})]}),"instanceName":"1"})])]});}
            var Q216;
            {var subQ0=sQuery(id+"F3.wireOp",EDGE,"E1.right");var subQ1=sQuery(id+"F3.wireOp",EDGE,"E1.top");var subQ2=sQuery(id+"F0.wireOp",EDGE,"E0.left");var subQ3=sQuery(id+"F0.wireOp",EDGE,"E0.top");Q216=makeQuery(id+"F9.opShell","OFFSET_EDGE",EDGE,{"disambiguationData":[OSD([subQ3,subQ2,subQ1,subQ0]),TDD([makeQuery(id+"F8.opPattern","COPY",EDGE,{"derivedFrom":makeQuery(id+"F7.opPattern","COPY",EDGE,{"derivedFrom":makeQuery(id+"F6.opPattern","COPY",EDGE,{"derivedFrom":makeQuery(id+"F4.opLoft","SWEPT_EDGE",EDGE,{"disambiguationData":[OSD([subQ3,subQ2,subQ1,subQ0])]}),"instanceName":"1"}),"instanceName":"1"}),"instanceName":"1"})])]});}
            var Q217;
            {var subQ0=sQuery(id+"F0.wireOp",EDGE,"E0.left");var subQ1=sQuery(id+"F0.wireOp",EDGE,"E0.top");var subQ2=sQuery(id+"F0.wireOp",EDGE,"E0.bottom");var subQ3=makeQuery(id+"F7.opPattern","COPY",EDGE,{"derivedFrom":makeQuery(id+"F6.opPattern","COPY",EDGE,{"derivedFrom":makeQuery(id+"F4.opLoft","MID_CAP_EDGE",EDGE,{"disambiguationData":[OSD([subQ2,subQ1,subQ0])],"capPos":0.0}),"instanceName":"1"}),"instanceName":"1"});Q217=makeQuery(id+"F9.opShell","OFFSET_EDGE",EDGE,{"disambiguationData":[OSD([subQ2,subQ1,subQ0]),TDD([makeQuery(id+"F8.boolean.opBoolean","MERGE",EDGE,{"derivedFrom":[subQ3,makeQuery(id+"F8.opPattern","COPY",EDGE,{"derivedFrom":subQ3,"instanceName":"1"})]})])]});}
            var Q218;
            {var subQ0=makeQuery(id+"F4.opLoft","MID_CAP_EDGE",EDGE,{"disambiguationData":[OSD([sQuery(id+"F0.wireOp",EDGE,"E0.bottom"),sQuery(id+"F0.wireOp",EDGE,"E0.top"),sQuery(id+"F0.wireOp",EDGE,"E0.left")])],"capPos":0.0});Q218=makeQuery(id+"F8.opPattern","COPY",EDGE,{"derivedFrom":makeQuery(id+"F7.boolean.opBoolean","MERGE",EDGE,{"derivedFrom":[subQ0,makeQuery(id+"F7.opPattern","COPY",EDGE,{"derivedFrom":subQ0,"instanceName":"1"})]}),"instanceName":"1"});}
            var Q219;
            Q219=makeQuery(id+"F8.opPattern","COPY",EDGE,{"derivedFrom":makeQuery(id+"F7.opPattern","COPY",EDGE,{"derivedFrom":makeQuery(id+"F4.opLoft","SWEPT_EDGE",EDGE,{"disambiguationData":[OSD([sQuery(id+"F0.wireOp",EDGE,"E0.top"),sQuery(id+"F0.wireOp",EDGE,"E0.left"),sQuery(id+"F3.wireOp",EDGE,"E1.top"),sQuery(id+"F3.wireOp",EDGE,"E1.right")])]}),"instanceName":"1"}),"instanceName":"1"});
            var Q220;
            {var subQ0=sQuery(id+"F0.wireOp",EDGE,"E0.right");var subQ1=sQuery(id+"F0.wireOp",EDGE,"E0.left");var subQ2=sQuery(id+"F0.wireOp",EDGE,"E0.top");var subQ3=makeQuery(id+"F5.opPattern","COPY",EDGE,{"derivedFrom":makeQuery(id+"F4.opLoft","MID_CAP_EDGE",EDGE,{"disambiguationData":[OSD([subQ2,subQ1,subQ0])],"capPos":0.0}),"instanceName":"1"});Q220=makeQuery(id+"F9.opShell","OFFSET_EDGE",EDGE,{"disambiguationData":[OSD([subQ2,subQ1,subQ0]),TDD([makeQuery(id+"F6.boolean.opBoolean","MERGE",EDGE,{"derivedFrom":[subQ3,makeQuery(id+"F6.opPattern","COPY",EDGE,{"derivedFrom":subQ3,"instanceName":"1"})]})])]});}
            var Q221;
            Q221=makeQuery(id+"F8.opPattern","COPY",EDGE,{"derivedFrom":makeQuery(id+"F7.opPattern","COPY",EDGE,{"derivedFrom":makeQuery(id+"F6.opPattern","COPY",EDGE,{"derivedFrom":makeQuery(id+"F4.opLoft","SWEPT_EDGE",EDGE,{"disambiguationData":[OSD([sQuery(id+"F0.wireOp",EDGE,"E0.top"),sQuery(id+"F0.wireOp",EDGE,"E0.left"),sQuery(id+"F3.wireOp",EDGE,"E1.top"),sQuery(id+"F3.wireOp",EDGE,"E1.right")])]}),"instanceName":"1"}),"instanceName":"1"}),"instanceName":"1"});
            var Q222;
            Q222=makeQuery(id+"F8.opPattern","COPY",EDGE,{"derivedFrom":makeQuery(id+"F6.opPattern","COPY",EDGE,{"derivedFrom":makeQuery(id+"F4.opLoft","SWEPT_EDGE",EDGE,{"disambiguationData":[OSD([sQuery(id+"F0.wireOp",EDGE,"E0.top"),sQuery(id+"F0.wireOp",EDGE,"E0.left"),sQuery(id+"F3.wireOp",EDGE,"E1.top"),sQuery(id+"F3.wireOp",EDGE,"E1.right")])]}),"instanceName":"1"}),"instanceName":"1"});
            var Q223;
            {var subQ0=sQuery(id+"F0.wireOp",EDGE,"E0.right");var subQ1=sQuery(id+"F0.wireOp",EDGE,"E0.left");var subQ2=sQuery(id+"F0.wireOp",EDGE,"E0.top");var subQ3=makeQuery(id+"F5.opPattern","COPY",EDGE,{"derivedFrom":makeQuery(id+"F4.opLoft","MID_CAP_EDGE",EDGE,{"disambiguationData":[OSD([subQ2,subQ1,subQ0])],"capPos":0.0}),"instanceName":"1"});Q223=makeQuery(id+"F9.opShell","OFFSET_EDGE",EDGE,{"disambiguationData":[OSD([subQ2,subQ1,subQ0]),TDD([makeQuery(id+"F7.opPattern","COPY",EDGE,{"derivedFrom":makeQuery(id+"F6.boolean.opBoolean","MERGE",EDGE,{"derivedFrom":[subQ3,makeQuery(id+"F6.opPattern","COPY",EDGE,{"derivedFrom":subQ3,"instanceName":"1"})]}),"instanceName":"1"})])]});}
            var Q224;
            {var subQ0=sQuery(id+"F0.wireOp",EDGE,"E0.right");var subQ1=sQuery(id+"F0.wireOp",EDGE,"E0.left");var subQ2=sQuery(id+"F0.wireOp",EDGE,"E0.top");var subQ3=makeQuery(id+"F4.opLoft","MID_CAP_EDGE",EDGE,{"disambiguationData":[OSD([subQ2,subQ1,subQ0])],"capPos":0.0});Q224=makeQuery(id+"F9.opShell","OFFSET_EDGE",EDGE,{"disambiguationData":[OSD([subQ2,subQ1,subQ0]),TDD([makeQuery(id+"F8.opPattern","COPY",EDGE,{"derivedFrom":makeQuery(id+"F7.boolean.opBoolean","MERGE",EDGE,{"derivedFrom":[subQ3,makeQuery(id+"F7.opPattern","COPY",EDGE,{"derivedFrom":subQ3,"instanceName":"1"})]}),"instanceName":"1"})])]});}
            var Q225;
            {var subQ0=sQuery(id+"F0.wireOp",EDGE,"E0.left");var subQ1=sQuery(id+"F0.wireOp",EDGE,"E0.top");var subQ2=sQuery(id+"F0.wireOp",EDGE,"E0.bottom");var subQ3=makeQuery(id+"F5.opPattern","COPY",EDGE,{"derivedFrom":makeQuery(id+"F4.opLoft","MID_CAP_EDGE",EDGE,{"disambiguationData":[OSD([subQ2,subQ1,subQ0])],"capPos":0.0}),"instanceName":"1"});Q225=makeQuery(id+"F9.opShell","OFFSET_EDGE",EDGE,{"disambiguationData":[OSD([subQ2,subQ1,subQ0]),TDD([makeQuery(id+"F8.opPattern","COPY",EDGE,{"derivedFrom":makeQuery(id+"F6.boolean.opBoolean","MERGE",EDGE,{"derivedFrom":[subQ3,makeQuery(id+"F6.opPattern","COPY",EDGE,{"derivedFrom":subQ3,"instanceName":"1"})]}),"instanceName":"1"})])]});}
            var Q226;
            {var subQ0=makeQuery(id+"F4.opLoft","MID_CAP_EDGE",EDGE,{"disambiguationData":[OSD([sQuery(id+"F3.wireOp",EDGE,"E1.top"),sQuery(id+"F3.wireOp",EDGE,"E1.left"),sQuery(id+"F3.wireOp",EDGE,"E1.right")])],"capPos":1.0});Q226=makeQuery(id+"F8.opPattern","COPY",EDGE,{"derivedFrom":makeQuery(id+"F6.opPattern","COPY",EDGE,{"derivedFrom":makeQuery(id+"F5.boolean.opBoolean","MERGE",EDGE,{"derivedFrom":[subQ0,makeQuery(id+"F5.opPattern","COPY",EDGE,{"derivedFrom":subQ0,"instanceName":"1"})]}),"instanceName":"1"}),"instanceName":"1"});}
            var Q227;
            {var subQ0=makeQuery(id+"F4.opLoft","MID_CAP_EDGE",EDGE,{"disambiguationData":[OSD([sQuery(id+"F3.wireOp",EDGE,"E1.bottom"),sQuery(id+"F3.wireOp",EDGE,"E1.top"),sQuery(id+"F3.wireOp",EDGE,"E1.right")])],"capPos":1.0});Q227=makeQuery(id+"F8.opPattern","COPY",EDGE,{"derivedFrom":makeQuery(id+"F7.opPattern","COPY",EDGE,{"derivedFrom":makeQuery(id+"F5.boolean.opBoolean","MERGE",EDGE,{"derivedFrom":[subQ0,makeQuery(id+"F5.opPattern","COPY",EDGE,{"derivedFrom":subQ0,"instanceName":"1"})]}),"instanceName":"1"}),"instanceName":"1"});}
            var Q228;
            Q228=makeQuery(id+"F8.opPattern","COPY",EDGE,{"derivedFrom":makeQuery(id+"F6.opPattern","COPY",EDGE,{"derivedFrom":makeQuery(id+"F5.opPattern","COPY",EDGE,{"derivedFrom":makeQuery(id+"F4.opLoft","SWEPT_EDGE",EDGE,{"disambiguationData":[OSD([sQuery(id+"F0.wireOp",EDGE,"E0.top"),sQuery(id+"F0.wireOp",EDGE,"E0.left"),sQuery(id+"F3.wireOp",EDGE,"E1.top"),sQuery(id+"F3.wireOp",EDGE,"E1.right")])]}),"instanceName":"1"}),"instanceName":"1"}),"instanceName":"1"});
            var Q229;
            Q229=makeQuery(id+"F8.opPattern","COPY",EDGE,{"derivedFrom":makeQuery(id+"F7.opPattern","COPY",EDGE,{"derivedFrom":makeQuery(id+"F6.opPattern","COPY",EDGE,{"derivedFrom":makeQuery(id+"F5.opPattern","COPY",EDGE,{"derivedFrom":makeQuery(id+"F4.opLoft","SWEPT_EDGE",EDGE,{"disambiguationData":[OSD([sQuery(id+"F0.wireOp",EDGE,"E0.top"),sQuery(id+"F0.wireOp",EDGE,"E0.left"),sQuery(id+"F3.wireOp",EDGE,"E1.top"),sQuery(id+"F3.wireOp",EDGE,"E1.right")])]}),"instanceName":"1"}),"instanceName":"1"}),"instanceName":"1"}),"instanceName":"1"});
            var Q230;
            {var subQ0=sQuery(id+"F3.wireOp",EDGE,"E1.right");var subQ1=sQuery(id+"F3.wireOp",EDGE,"E1.left");var subQ2=sQuery(id+"F3.wireOp",EDGE,"E1.top");var subQ3=makeQuery(id+"F4.opLoft","MID_CAP_EDGE",EDGE,{"disambiguationData":[OSD([subQ2,subQ1,subQ0])],"capPos":1.0});Q230=makeQuery(id+"F9.opShell","OFFSET_EDGE",EDGE,{"disambiguationData":[OSD([subQ2,subQ1,subQ0]),TDD([makeQuery(id+"F6.opPattern","COPY",EDGE,{"derivedFrom":makeQuery(id+"F5.boolean.opBoolean","MERGE",EDGE,{"derivedFrom":[subQ3,makeQuery(id+"F5.opPattern","COPY",EDGE,{"derivedFrom":subQ3,"instanceName":"1"})]}),"instanceName":"1"})])]});}
            var Q231;
            {var subQ0=makeQuery(id+"F7.opPattern","COPY",EDGE,{"derivedFrom":makeQuery(id+"F6.opPattern","COPY",EDGE,{"derivedFrom":makeQuery(id+"F4.opLoft","MID_CAP_EDGE",EDGE,{"disambiguationData":[OSD([sQuery(id+"F0.wireOp",EDGE,"E0.bottom"),sQuery(id+"F0.wireOp",EDGE,"E0.top"),sQuery(id+"F0.wireOp",EDGE,"E0.left")])],"capPos":0.0}),"instanceName":"1"}),"instanceName":"1"});Q231=makeQuery(id+"F8.boolean.opBoolean","MERGE",EDGE,{"derivedFrom":[subQ0,makeQuery(id+"F8.opPattern","COPY",EDGE,{"derivedFrom":subQ0,"instanceName":"1"})]});}
            var Q232;
            {var subQ0=makeQuery(id+"F4.opLoft","MID_CAP_EDGE",EDGE,{"disambiguationData":[OSD([sQuery(id+"F3.wireOp",EDGE,"E1.bottom"),sQuery(id+"F3.wireOp",EDGE,"E1.top"),sQuery(id+"F3.wireOp",EDGE,"E1.right")])],"capPos":1.0});Q232=makeQuery(id+"F8.opPattern","COPY",EDGE,{"derivedFrom":makeQuery(id+"F5.boolean.opBoolean","MERGE",EDGE,{"derivedFrom":[subQ0,makeQuery(id+"F5.opPattern","COPY",EDGE,{"derivedFrom":subQ0,"instanceName":"1"})]}),"instanceName":"1"});}
            var Q233;
            {var subQ0=makeQuery(id+"F5.opPattern","COPY",EDGE,{"derivedFrom":makeQuery(id+"F4.opLoft","MID_CAP_EDGE",EDGE,{"disambiguationData":[OSD([sQuery(id+"F0.wireOp",EDGE,"E0.top"),sQuery(id+"F0.wireOp",EDGE,"E0.left"),sQuery(id+"F0.wireOp",EDGE,"E0.right")])],"capPos":0.0}),"instanceName":"1"});Q233=makeQuery(id+"F7.opPattern","COPY",EDGE,{"derivedFrom":makeQuery(id+"F6.boolean.opBoolean","MERGE",EDGE,{"derivedFrom":[subQ0,makeQuery(id+"F6.opPattern","COPY",EDGE,{"derivedFrom":subQ0,"instanceName":"1"})]}),"instanceName":"1"});}
            var Q234;
            Q234=makeQuery(id+"F7.opPattern","COPY",EDGE,{"derivedFrom":makeQuery(id+"F6.opPattern","COPY",EDGE,{"derivedFrom":makeQuery(id+"F4.opLoft","SWEPT_EDGE",EDGE,{"disambiguationData":[OSD([sQuery(id+"F0.wireOp",EDGE,"E0.top"),sQuery(id+"F0.wireOp",EDGE,"E0.right"),sQuery(id+"F3.wireOp",EDGE,"E1.top"),sQuery(id+"F3.wireOp",EDGE,"E1.left")])]}),"instanceName":"1"}),"instanceName":"1"});
            var Q235;
            {var subQ0=makeQuery(id+"F5.opPattern","COPY",EDGE,{"derivedFrom":makeQuery(id+"F4.opLoft","MID_CAP_EDGE",EDGE,{"disambiguationData":[OSD([sQuery(id+"F0.wireOp",EDGE,"E0.bottom"),sQuery(id+"F0.wireOp",EDGE,"E0.top"),sQuery(id+"F0.wireOp",EDGE,"E0.left")])],"capPos":0.0}),"instanceName":"1"});Q235=makeQuery(id+"F7.opPattern","COPY",EDGE,{"derivedFrom":makeQuery(id+"F6.boolean.opBoolean","MERGE",EDGE,{"derivedFrom":[subQ0,makeQuery(id+"F6.opPattern","COPY",EDGE,{"derivedFrom":subQ0,"instanceName":"1"})]}),"instanceName":"1"});}
            var Q236;
            Q236=makeQuery(id+"F7.opPattern","COPY",EDGE,{"derivedFrom":makeQuery(id+"F5.opPattern","COPY",EDGE,{"derivedFrom":makeQuery(id+"F4.opLoft","SWEPT_EDGE",EDGE,{"disambiguationData":[OSD([sQuery(id+"F0.wireOp",EDGE,"E0.top"),sQuery(id+"F0.wireOp",EDGE,"E0.right"),sQuery(id+"F3.wireOp",EDGE,"E1.top"),sQuery(id+"F3.wireOp",EDGE,"E1.left")])]}),"instanceName":"1"}),"instanceName":"1"});
            var Q237;
            Q237=makeQuery(id+"F8.opPattern","COPY",EDGE,{"derivedFrom":makeQuery(id+"F4.opLoft","SWEPT_EDGE",EDGE,{"disambiguationData":[OSD([sQuery(id+"F0.wireOp",EDGE,"E0.top"),sQuery(id+"F0.wireOp",EDGE,"E0.left"),sQuery(id+"F3.wireOp",EDGE,"E1.top"),sQuery(id+"F3.wireOp",EDGE,"E1.right")])]}),"instanceName":"1"});
            var Q238;
            {var subQ0=sQuery(id+"F3.wireOp",EDGE,"E1.right");var subQ1=sQuery(id+"F3.wireOp",EDGE,"E1.left");var subQ2=sQuery(id+"F3.wireOp",EDGE,"E1.top");var subQ3=makeQuery(id+"F4.opLoft","MID_CAP_EDGE",EDGE,{"disambiguationData":[OSD([subQ2,subQ1,subQ0])],"capPos":1.0});Q238=makeQuery(id+"F9.opShell","OFFSET_EDGE",EDGE,{"disambiguationData":[OSD([subQ2,subQ1,subQ0]),TDD([makeQuery(id+"F8.opPattern","COPY",EDGE,{"derivedFrom":makeQuery(id+"F5.boolean.opBoolean","MERGE",EDGE,{"derivedFrom":[subQ3,makeQuery(id+"F5.opPattern","COPY",EDGE,{"derivedFrom":subQ3,"instanceName":"1"})]}),"instanceName":"1"})])]});}
            var Q239;
            {var subQ0=sQuery(id+"F0.wireOp",EDGE,"E0.left");var subQ1=sQuery(id+"F0.wireOp",EDGE,"E0.top");var subQ2=sQuery(id+"F0.wireOp",EDGE,"E0.bottom");var subQ3=makeQuery(id+"F4.opLoft","MID_CAP_EDGE",EDGE,{"disambiguationData":[OSD([subQ2,subQ1,subQ0])],"capPos":0.0});Q239=makeQuery(id+"F9.opShell","OFFSET_EDGE",EDGE,{"disambiguationData":[OSD([subQ2,subQ1,subQ0]),TDD([makeQuery(id+"F8.opPattern","COPY",EDGE,{"derivedFrom":makeQuery(id+"F7.boolean.opBoolean","MERGE",EDGE,{"derivedFrom":[subQ3,makeQuery(id+"F7.opPattern","COPY",EDGE,{"derivedFrom":subQ3,"instanceName":"1"})]}),"instanceName":"1"})])]});}
            var Q240;
            {var subQ0=sQuery(id+"F3.wireOp",EDGE,"E1.left");var subQ1=sQuery(id+"F3.wireOp",EDGE,"E1.top");var subQ2=sQuery(id+"F3.wireOp",EDGE,"E1.bottom");var subQ3=makeQuery(id+"F4.opLoft","MID_CAP_EDGE",EDGE,{"disambiguationData":[OSD([subQ2,subQ1,subQ0])],"capPos":1.0});Q240=makeQuery(id+"F9.opShell","OFFSET_EDGE",EDGE,{"disambiguationData":[OSD([subQ2,subQ1,subQ0]),TDD([makeQuery(id+"F6.opPattern","COPY",EDGE,{"derivedFrom":makeQuery(id+"F5.boolean.opBoolean","MERGE",EDGE,{"derivedFrom":[subQ3,makeQuery(id+"F5.opPattern","COPY",EDGE,{"derivedFrom":subQ3,"instanceName":"1"})]}),"instanceName":"1"})])]});}
            var Q241;
            {var subQ0=sQuery(id+"F3.wireOp",EDGE,"E1.right");var subQ1=sQuery(id+"F3.wireOp",EDGE,"E1.bottom");var subQ2=sQuery(id+"F0.wireOp",EDGE,"E0.left");var subQ3=sQuery(id+"F0.wireOp",EDGE,"E0.bottom");Q241=makeQuery(id+"F9.opShell","OFFSET_EDGE",EDGE,{"disambiguationData":[OSD([subQ3,subQ2,subQ1,subQ0]),TDD([makeQuery(id+"F7.opPattern","COPY",EDGE,{"derivedFrom":makeQuery(id+"F6.opPattern","COPY",EDGE,{"derivedFrom":makeQuery(id+"F5.opPattern","COPY",EDGE,{"derivedFrom":makeQuery(id+"F4.opLoft","SWEPT_EDGE",EDGE,{"disambiguationData":[OSD([subQ3,subQ2,subQ1,subQ0])]}),"instanceName":"1"}),"instanceName":"1"}),"instanceName":"1"})])]});}
            var Q242;
            {var subQ0=makeQuery(id+"F5.opPattern","COPY",EDGE,{"derivedFrom":makeQuery(id+"F4.opLoft","MID_CAP_EDGE",EDGE,{"disambiguationData":[OSD([sQuery(id+"F0.wireOp",EDGE,"E0.top"),sQuery(id+"F0.wireOp",EDGE,"E0.left"),sQuery(id+"F0.wireOp",EDGE,"E0.right")])],"capPos":0.0}),"instanceName":"1"});Q242=makeQuery(id+"F8.opPattern","COPY",EDGE,{"derivedFrom":makeQuery(id+"F7.opPattern","COPY",EDGE,{"derivedFrom":makeQuery(id+"F6.boolean.opBoolean","MERGE",EDGE,{"derivedFrom":[subQ0,makeQuery(id+"F6.opPattern","COPY",EDGE,{"derivedFrom":subQ0,"instanceName":"1"})]}),"instanceName":"1"}),"instanceName":"1"});}
            var Q243;
            {var subQ0=makeQuery(id+"F5.opPattern","COPY",EDGE,{"derivedFrom":makeQuery(id+"F4.opLoft","MID_CAP_EDGE",EDGE,{"disambiguationData":[OSD([sQuery(id+"F0.wireOp",EDGE,"E0.bottom"),sQuery(id+"F0.wireOp",EDGE,"E0.top"),sQuery(id+"F0.wireOp",EDGE,"E0.left")])],"capPos":0.0}),"instanceName":"1"});Q243=makeQuery(id+"F8.opPattern","COPY",EDGE,{"derivedFrom":makeQuery(id+"F7.opPattern","COPY",EDGE,{"derivedFrom":makeQuery(id+"F6.boolean.opBoolean","MERGE",EDGE,{"derivedFrom":[subQ0,makeQuery(id+"F6.opPattern","COPY",EDGE,{"derivedFrom":subQ0,"instanceName":"1"})]}),"instanceName":"1"}),"instanceName":"1"});}
            var Q244;
            {var subQ0=makeQuery(id+"F4.opLoft","MID_CAP_EDGE",EDGE,{"disambiguationData":[OSD([sQuery(id+"F0.wireOp",EDGE,"E0.bottom"),sQuery(id+"F0.wireOp",EDGE,"E0.top"),sQuery(id+"F0.wireOp",EDGE,"E0.left")])],"capPos":0.0});Q244=makeQuery(id+"F7.boolean.opBoolean","MERGE",EDGE,{"derivedFrom":[subQ0,makeQuery(id+"F7.opPattern","COPY",EDGE,{"derivedFrom":subQ0,"instanceName":"1"})]});}
            var Q245;
            {var subQ0=makeQuery(id+"F4.opLoft","MID_CAP_EDGE",EDGE,{"disambiguationData":[OSD([sQuery(id+"F3.wireOp",EDGE,"E1.bottom"),sQuery(id+"F3.wireOp",EDGE,"E1.top"),sQuery(id+"F3.wireOp",EDGE,"E1.right")])],"capPos":1.0});Q245=makeQuery(id+"F8.opPattern","COPY",EDGE,{"derivedFrom":makeQuery(id+"F7.opPattern","COPY",EDGE,{"derivedFrom":makeQuery(id+"F6.opPattern","COPY",EDGE,{"derivedFrom":makeQuery(id+"F5.boolean.opBoolean","MERGE",EDGE,{"derivedFrom":[subQ0,makeQuery(id+"F5.opPattern","COPY",EDGE,{"derivedFrom":subQ0,"instanceName":"1"})]}),"instanceName":"1"}),"instanceName":"1"}),"instanceName":"1"});}
            var Q246;
            Q246=makeQuery(id+"F8.opPattern","COPY",EDGE,{"derivedFrom":makeQuery(id+"F7.opPattern","COPY",EDGE,{"derivedFrom":makeQuery(id+"F5.opPattern","COPY",EDGE,{"derivedFrom":makeQuery(id+"F4.opLoft","SWEPT_EDGE",EDGE,{"disambiguationData":[OSD([sQuery(id+"F0.wireOp",EDGE,"E0.top"),sQuery(id+"F0.wireOp",EDGE,"E0.left"),sQuery(id+"F3.wireOp",EDGE,"E1.top"),sQuery(id+"F3.wireOp",EDGE,"E1.right")])]}),"instanceName":"1"}),"instanceName":"1"}),"instanceName":"1"});
            var Q247;
            {var subQ0=sQuery(id+"F0.wireOp",EDGE,"E0.right");var subQ1=sQuery(id+"F0.wireOp",EDGE,"E0.left");var subQ2=sQuery(id+"F0.wireOp",EDGE,"E0.top");Q247=makeQuery(id+"F9.opShell","OFFSET_EDGE",EDGE,{"disambiguationData":[OSD([subQ2,subQ1,subQ0]),TDD([makeQuery(id+"F6.opPattern","COPY",EDGE,{"derivedFrom":makeQuery(id+"F4.opLoft","MID_CAP_EDGE",EDGE,{"disambiguationData":[OSD([subQ2,subQ1,subQ0])],"capPos":0.0}),"instanceName":"1"})])]});}
            var Q248;
            {var subQ0=sQuery(id+"F3.wireOp",EDGE,"E1.left");var subQ1=sQuery(id+"F3.wireOp",EDGE,"E1.bottom");var subQ2=sQuery(id+"F0.wireOp",EDGE,"E0.right");var subQ3=sQuery(id+"F0.wireOp",EDGE,"E0.bottom");Q248=makeQuery(id+"F9.opShell","OFFSET_EDGE",EDGE,{"disambiguationData":[OSD([subQ3,subQ2,subQ1,subQ0]),TDD([makeQuery(id+"F4.opLoft","SWEPT_EDGE",EDGE,{"disambiguationData":[OSD([subQ3,subQ2,subQ1,subQ0])]})])]});}
            var Q249;
            {var subQ0=sQuery(id+"F0.wireOp",EDGE,"E0.right");var subQ1=sQuery(id+"F0.wireOp",EDGE,"E0.left");var subQ2=sQuery(id+"F0.wireOp",EDGE,"E0.top");var subQ3=makeQuery(id+"F4.opLoft","MID_CAP_EDGE",EDGE,{"disambiguationData":[OSD([subQ2,subQ1,subQ0])],"capPos":0.0});Q249=makeQuery(id+"F9.opShell","OFFSET_EDGE",EDGE,{"disambiguationData":[OSD([subQ2,subQ1,subQ0]),TDD([makeQuery(id+"F7.boolean.opBoolean","MERGE",EDGE,{"derivedFrom":[subQ3,makeQuery(id+"F7.opPattern","COPY",EDGE,{"derivedFrom":subQ3,"instanceName":"1"})]})])]});}
            var Q250;
            {var subQ0=sQuery(id+"F3.wireOp",EDGE,"E1.right");var subQ1=sQuery(id+"F3.wireOp",EDGE,"E1.bottom");var subQ2=sQuery(id+"F0.wireOp",EDGE,"E0.left");var subQ3=sQuery(id+"F0.wireOp",EDGE,"E0.bottom");Q250=makeQuery(id+"F9.opShell","OFFSET_EDGE",EDGE,{"disambiguationData":[OSD([subQ3,subQ2,subQ1,subQ0]),TDD([makeQuery(id+"F8.opPattern","COPY",EDGE,{"derivedFrom":makeQuery(id+"F4.opLoft","SWEPT_EDGE",EDGE,{"disambiguationData":[OSD([subQ3,subQ2,subQ1,subQ0])]}),"instanceName":"1"})])]});}
            var Q251;
            {var subQ0=makeQuery(id+"F4.opLoft","MID_CAP_EDGE",EDGE,{"disambiguationData":[OSD([sQuery(id+"F3.wireOp",EDGE,"E1.top"),sQuery(id+"F3.wireOp",EDGE,"E1.left"),sQuery(id+"F3.wireOp",EDGE,"E1.right")])],"capPos":1.0});Q251=makeQuery(id+"F5.boolean.opBoolean","MERGE",EDGE,{"derivedFrom":[subQ0,makeQuery(id+"F5.opPattern","COPY",EDGE,{"derivedFrom":subQ0,"instanceName":"1"})]});}
            var Q252;
            {var subQ0=makeQuery(id+"F4.opLoft","MID_CAP_EDGE",EDGE,{"disambiguationData":[OSD([sQuery(id+"F3.wireOp",EDGE,"E1.top"),sQuery(id+"F3.wireOp",EDGE,"E1.left"),sQuery(id+"F3.wireOp",EDGE,"E1.right")])],"capPos":1.0});Q252=makeQuery(id+"F8.opPattern","COPY",EDGE,{"derivedFrom":makeQuery(id+"F5.boolean.opBoolean","MERGE",EDGE,{"derivedFrom":[subQ0,makeQuery(id+"F5.opPattern","COPY",EDGE,{"derivedFrom":subQ0,"instanceName":"1"})]}),"instanceName":"1"});}
            var Q253;
            {var subQ0=sQuery(id+"F3.wireOp",EDGE,"E1.right");var subQ1=sQuery(id+"F3.wireOp",EDGE,"E1.top");var subQ2=sQuery(id+"F0.wireOp",EDGE,"E0.left");var subQ3=sQuery(id+"F0.wireOp",EDGE,"E0.top");Q253=makeQuery(id+"F9.opShell","OFFSET_EDGE",EDGE,{"disambiguationData":[OSD([subQ3,subQ2,subQ1,subQ0]),TDD([makeQuery(id+"F8.opPattern","COPY",EDGE,{"derivedFrom":makeQuery(id+"F7.opPattern","COPY",EDGE,{"derivedFrom":makeQuery(id+"F4.opLoft","SWEPT_EDGE",EDGE,{"disambiguationData":[OSD([subQ3,subQ2,subQ1,subQ0])]}),"instanceName":"1"}),"instanceName":"1"})])]});}
            var Q254;
            {var subQ0=sQuery(id+"F3.wireOp",EDGE,"E1.right");var subQ1=sQuery(id+"F3.wireOp",EDGE,"E1.top");var subQ2=sQuery(id+"F3.wireOp",EDGE,"E1.bottom");var subQ3=makeQuery(id+"F4.opLoft","MID_CAP_EDGE",EDGE,{"disambiguationData":[OSD([subQ2,subQ1,subQ0])],"capPos":1.0});Q254=makeQuery(id+"F9.opShell","OFFSET_EDGE",EDGE,{"disambiguationData":[OSD([subQ2,subQ1,subQ0]),TDD([makeQuery(id+"F8.opPattern","COPY",EDGE,{"derivedFrom":makeQuery(id+"F5.boolean.opBoolean","MERGE",EDGE,{"derivedFrom":[subQ3,makeQuery(id+"F5.opPattern","COPY",EDGE,{"derivedFrom":subQ3,"instanceName":"1"})]}),"instanceName":"1"})])]});}
            var Q255;
            {var subQ0=sQuery(id+"F3.wireOp",EDGE,"E1.right");var subQ1=sQuery(id+"F3.wireOp",EDGE,"E1.top");var subQ2=sQuery(id+"F3.wireOp",EDGE,"E1.bottom");var subQ3=makeQuery(id+"F4.opLoft","MID_CAP_EDGE",EDGE,{"disambiguationData":[OSD([subQ2,subQ1,subQ0])],"capPos":1.0});Q255=makeQuery(id+"F9.opShell","OFFSET_EDGE",EDGE,{"disambiguationData":[OSD([subQ2,subQ1,subQ0]),TDD([makeQuery(id+"F8.opPattern","COPY",EDGE,{"derivedFrom":makeQuery(id+"F7.opPattern","COPY",EDGE,{"derivedFrom":makeQuery(id+"F5.boolean.opBoolean","MERGE",EDGE,{"derivedFrom":[subQ3,makeQuery(id+"F5.opPattern","COPY",EDGE,{"derivedFrom":subQ3,"instanceName":"1"})]}),"instanceName":"1"}),"instanceName":"1"})])]});}
            var Q256;
            {var subQ0=sQuery(id+"F3.wireOp",EDGE,"E1.left");var subQ1=sQuery(id+"F3.wireOp",EDGE,"E1.top");var subQ2=sQuery(id+"F0.wireOp",EDGE,"E0.right");var subQ3=sQuery(id+"F0.wireOp",EDGE,"E0.top");Q256=makeQuery(id+"F9.opShell","OFFSET_EDGE",EDGE,{"disambiguationData":[OSD([subQ3,subQ2,subQ1,subQ0]),TDD([makeQuery(id+"F7.opPattern","COPY",EDGE,{"derivedFrom":makeQuery(id+"F5.opPattern","COPY",EDGE,{"derivedFrom":makeQuery(id+"F4.opLoft","SWEPT_EDGE",EDGE,{"disambiguationData":[OSD([subQ3,subQ2,subQ1,subQ0])]}),"instanceName":"1"}),"instanceName":"1"})])]});}
            var Q257;
            {var subQ0=sQuery(id+"F3.wireOp",EDGE,"E1.left");var subQ1=sQuery(id+"F3.wireOp",EDGE,"E1.top");var subQ2=sQuery(id+"F0.wireOp",EDGE,"E0.right");var subQ3=sQuery(id+"F0.wireOp",EDGE,"E0.top");Q257=makeQuery(id+"F9.opShell","OFFSET_EDGE",EDGE,{"disambiguationData":[OSD([subQ3,subQ2,subQ1,subQ0]),TDD([makeQuery(id+"F4.opLoft","SWEPT_EDGE",EDGE,{"disambiguationData":[OSD([subQ3,subQ2,subQ1,subQ0])]})])]});}
            var Q258;
            {var subQ0=sQuery(id+"F3.wireOp",EDGE,"E1.right");var subQ1=sQuery(id+"F3.wireOp",EDGE,"E1.top");var subQ2=sQuery(id+"F0.wireOp",EDGE,"E0.left");var subQ3=sQuery(id+"F0.wireOp",EDGE,"E0.top");Q258=makeQuery(id+"F9.opShell","OFFSET_EDGE",EDGE,{"disambiguationData":[OSD([subQ3,subQ2,subQ1,subQ0]),TDD([makeQuery(id+"F7.opPattern","COPY",EDGE,{"derivedFrom":makeQuery(id+"F6.opPattern","COPY",EDGE,{"derivedFrom":makeQuery(id+"F4.opLoft","SWEPT_EDGE",EDGE,{"disambiguationData":[OSD([subQ3,subQ2,subQ1,subQ0])]}),"instanceName":"1"}),"instanceName":"1"})])]});}
            var Q259;
            {var subQ0=sQuery(id+"F3.wireOp",EDGE,"E1.left");var subQ1=sQuery(id+"F3.wireOp",EDGE,"E1.top");var subQ2=sQuery(id+"F3.wireOp",EDGE,"E1.bottom");var subQ3=makeQuery(id+"F4.opLoft","MID_CAP_EDGE",EDGE,{"disambiguationData":[OSD([subQ2,subQ1,subQ0])],"capPos":1.0});Q259=makeQuery(id+"F9.opShell","OFFSET_EDGE",EDGE,{"disambiguationData":[OSD([subQ2,subQ1,subQ0]),TDD([makeQuery(id+"F8.opPattern","COPY",EDGE,{"derivedFrom":makeQuery(id+"F6.opPattern","COPY",EDGE,{"derivedFrom":makeQuery(id+"F5.boolean.opBoolean","MERGE",EDGE,{"derivedFrom":[subQ3,makeQuery(id+"F5.opPattern","COPY",EDGE,{"derivedFrom":subQ3,"instanceName":"1"})]}),"instanceName":"1"}),"instanceName":"1"})])]});}
            var Q260;
            {var subQ0=makeQuery(id+"F4.opLoft","MID_CAP_EDGE",EDGE,{"disambiguationData":[OSD([sQuery(id+"F3.wireOp",EDGE,"E1.top"),sQuery(id+"F3.wireOp",EDGE,"E1.left"),sQuery(id+"F3.wireOp",EDGE,"E1.right")])],"capPos":1.0});Q260=makeQuery(id+"F8.opPattern","COPY",EDGE,{"derivedFrom":makeQuery(id+"F7.opPattern","COPY",EDGE,{"derivedFrom":makeQuery(id+"F5.boolean.opBoolean","MERGE",EDGE,{"derivedFrom":[subQ0,makeQuery(id+"F5.opPattern","COPY",EDGE,{"derivedFrom":subQ0,"instanceName":"1"})]}),"instanceName":"1"}),"instanceName":"1"});}
            var Q261;
            {var subQ0=makeQuery(id+"F4.opLoft","MID_CAP_EDGE",EDGE,{"disambiguationData":[OSD([sQuery(id+"F0.wireOp",EDGE,"E0.top"),sQuery(id+"F0.wireOp",EDGE,"E0.left"),sQuery(id+"F0.wireOp",EDGE,"E0.right")])],"capPos":0.0});Q261=makeQuery(id+"F8.opPattern","COPY",EDGE,{"derivedFrom":makeQuery(id+"F7.boolean.opBoolean","MERGE",EDGE,{"derivedFrom":[subQ0,makeQuery(id+"F7.opPattern","COPY",EDGE,{"derivedFrom":subQ0,"instanceName":"1"})]}),"instanceName":"1"});}
            var Q262;
            Q262=makeQuery(id+"F7.opPattern","COPY",EDGE,{"derivedFrom":makeQuery(id+"F6.opPattern","COPY",EDGE,{"derivedFrom":makeQuery(id+"F4.opLoft","SWEPT_EDGE",EDGE,{"disambiguationData":[OSD([sQuery(id+"F0.wireOp",EDGE,"E0.top"),sQuery(id+"F0.wireOp",EDGE,"E0.left"),sQuery(id+"F3.wireOp",EDGE,"E1.top"),sQuery(id+"F3.wireOp",EDGE,"E1.right")])]}),"instanceName":"1"}),"instanceName":"1"});
            var Q263;
            {var subQ0=sQuery(id+"F3.wireOp",EDGE,"E1.right");var subQ1=sQuery(id+"F3.wireOp",EDGE,"E1.top");var subQ2=sQuery(id+"F0.wireOp",EDGE,"E0.left");var subQ3=sQuery(id+"F0.wireOp",EDGE,"E0.top");Q263=makeQuery(id+"F9.opShell","OFFSET_EDGE",EDGE,{"disambiguationData":[OSD([subQ3,subQ2,subQ1,subQ0]),TDD([makeQuery(id+"F8.opPattern","COPY",EDGE,{"derivedFrom":makeQuery(id+"F4.opLoft","SWEPT_EDGE",EDGE,{"disambiguationData":[OSD([subQ3,subQ2,subQ1,subQ0])]}),"instanceName":"1"})])]});}
            fillet(context, id + "F11", {"entities" : qUnion([Q0, Q1, Q2, Q3, Q4, Q5, Q6, Q7, Q8, Q9, Q10, Q11, Q12, Q13, Q14, Q15, Q16, Q17, Q18, Q19, Q20, Q21, Q22, Q23, Q24, Q25, Q26, Q27, Q28, Q29, Q30, Q31, Q32, Q33, Q34, Q35, Q36, Q37, Q38, Q39, Q40, Q41, Q42, Q43, Q44, Q45, Q46, Q47, Q48, Q49, Q50, Q51, Q52, Q53, Q54, Q55, Q56, Q57, Q58, Q59, Q60, Q61, Q62, Q63, Q64, Q65, Q66, Q67, Q68, Q69, Q70, Q71, Q72, Q73, Q74, Q75, Q76, Q77, Q78, Q79, Q80, Q81, Q82, Q83, Q84, Q85, Q86, Q87, Q88, Q89, Q90, Q91, Q92, Q93, Q94, Q95, Q96, Q97, Q98, Q99, Q100, Q101, Q102, Q103, Q104, Q105, Q106, Q107, Q108, Q109, Q110, Q111, Q112, Q113, Q114, Q115, Q116, Q117, Q118, Q119, Q120, Q121, Q122, Q123, Q124, Q125, Q126, Q127, Q128, Q129, Q130, Q131, Q132, Q133, Q134, Q135, Q136, Q137, Q138, Q139, Q140, Q141, Q142, Q143, Q144, Q145, Q146, Q147, Q148, Q149, Q150, Q151, Q152, Q153, Q154, Q155, Q156, Q157, Q158, Q159, Q160, Q161, Q162, Q163, Q164, Q165, Q166, Q167, Q168, Q169, Q170, Q171, Q172, Q173, Q174, Q175, Q176, Q177, Q178, Q179, Q180, Q181, Q182, Q183, Q184, Q185, Q186, Q187, Q188, Q189, Q190, Q191, Q192, Q193, Q194, Q195, Q196, Q197, Q198, Q199, Q200, Q201, Q202, Q203, Q204, Q205, Q206, Q207, Q208, Q209, Q210, Q211, Q212, Q213, Q214, Q215, Q216, Q217, Q218, Q219, Q220, Q221, Q222, Q223, Q224, Q225, Q226, Q227, Q228, Q229, Q230, Q231, Q232, Q233, Q234, Q235, Q236, Q237, Q238, Q239, Q240, Q241, Q242, Q243, Q244, Q245, Q246, Q247, Q248, Q249, Q250, Q251, Q252, Q253, Q254, Q255, Q256, Q257, Q258, Q259, Q260, Q261, Q262, Q263]), "radius" : 2 * mm, "tangentPropagation" : true, "allowEdgeOverflow" : false});
        }
    });
